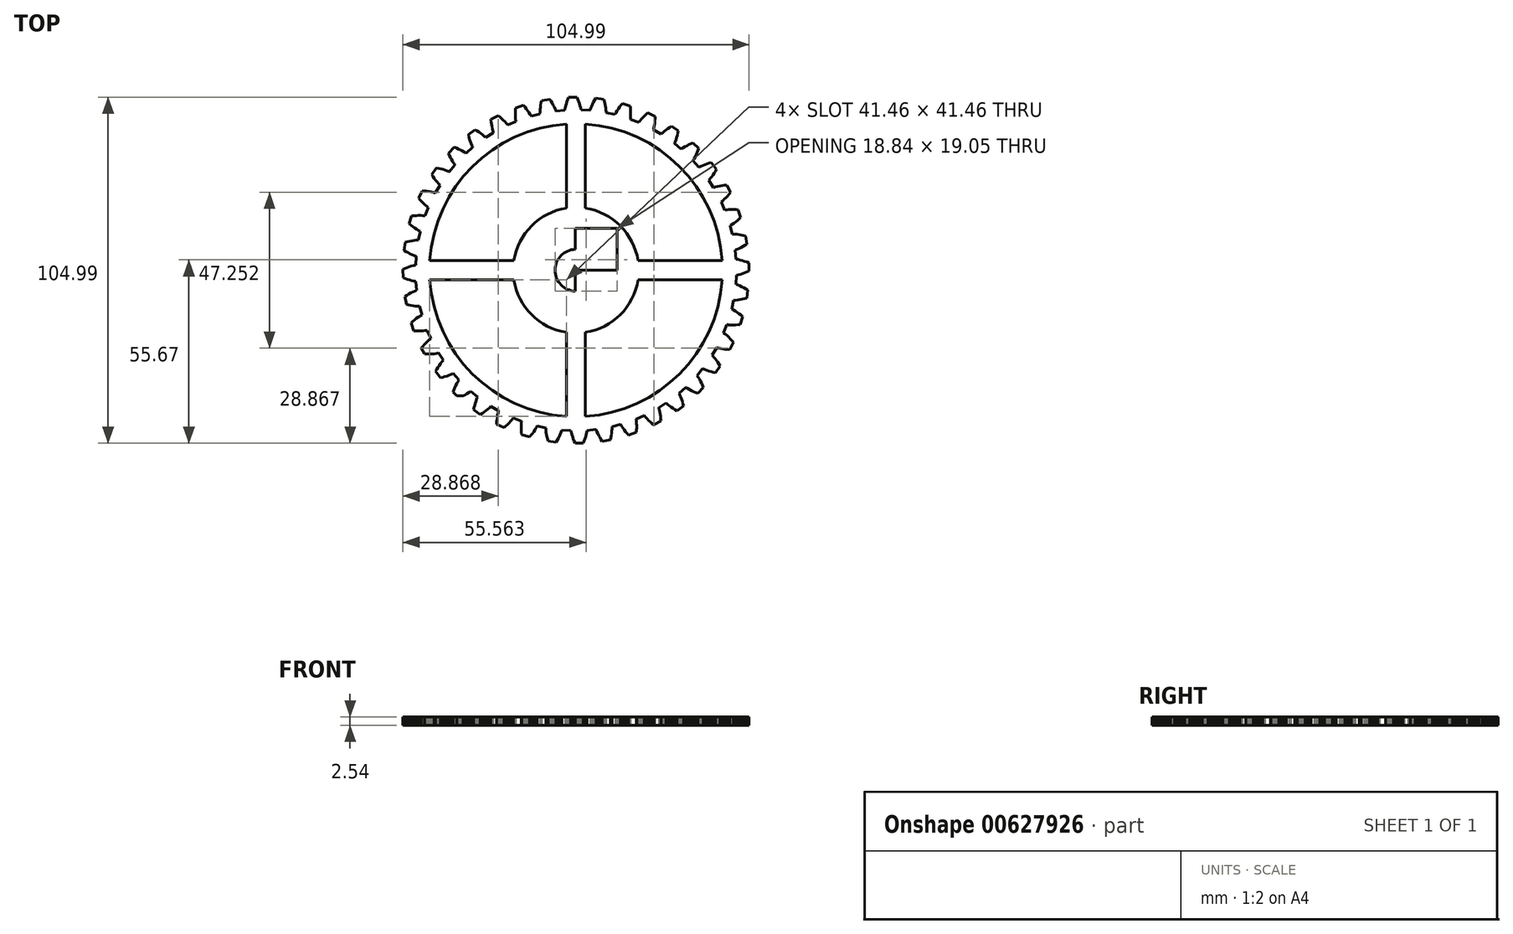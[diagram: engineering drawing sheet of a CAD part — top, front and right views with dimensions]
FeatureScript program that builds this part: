
annotation { "Feature Type Name" : "Feature", "Feature Type Description" : "" }
export const myFeature = defineFeature(function(context is Context, id is Id, definition is map)
    precondition{}
    {
        {
            var Q0;
            Q0=qCreatedBy(makeId("Top.planeOp"),FACE);
            var sketch = newSketch(context, id + "F0", { "sketchPlane" : qUnion([Q0])});
            skLineSegment(sketch, "E0", {"start": v(-71.15, -49.53) * mm, "end": v(-71.15, 55.46) * mm});
            skLineSegment(sketch, "E1", {"start": v(-58.45, -49.53) * mm, "end": v(-58.45, 55.46) * mm});
            skLineSegment(sketch, "E2", {"start": v(-45.75, -49.53) * mm, "end": v(-45.75, 55.46) * mm});
            skLineSegment(sketch, "E3", {"start": v(-33.05, -49.53) * mm, "end": v(-33.05, 55.46) * mm});
            skLineSegment(sketch, "E4", {"start": v(-20.35, -49.53) * mm, "end": v(-20.35, 55.46) * mm});
            skLineSegment(sketch, "E5", {"start": v(-7.65, -49.53) * mm, "end": v(-7.65, 55.46) * mm});
            skLineSegment(sketch, "E6", {"start": v(5.05, -49.53) * mm, "end": v(5.05, 55.46) * mm});
            skLineSegment(sketch, "E7", {"start": v(17.75, -49.53) * mm, "end": v(17.75, 55.46) * mm});
            skLineSegment(sketch, "E8", {"start": v(30.45, -49.53) * mm, "end": v(30.45, 55.46) * mm});
            skLineSegment(sketch, "E9", {"start": v(43.15, -49.53) * mm, "end": v(43.15, 55.46) * mm});
            skLineSegment(sketch, "E10", {"start": v(55.85, -49.53) * mm, "end": v(55.85, 55.46) * mm});
            skLineSegment(sketch, "E11", {"start": v(-72.63, -47.84) * mm, "end": v(62.71, -47.84) * mm});
            skLineSegment(sketch, "E12", {"start": v(-72.63, -35.14) * mm, "end": v(62.71, -35.14) * mm});
            skLineSegment(sketch, "E13", {"start": v(-72.63, -22.44) * mm, "end": v(62.71, -22.44) * mm});
            skLineSegment(sketch, "E14", {"start": v(-72.63, -9.74) * mm, "end": v(62.71, -9.74) * mm});
            skLineSegment(sketch, "E15", {"start": v(-72.63, 2.96) * mm, "end": v(62.71, 2.96) * mm});
            skLineSegment(sketch, "E16", {"start": v(-72.63, 15.66) * mm, "end": v(62.71, 15.66) * mm});
            skLineSegment(sketch, "E17", {"start": v(-72.63, 28.36) * mm, "end": v(62.71, 28.36) * mm});
            skLineSegment(sketch, "E18", {"start": v(-72.63, 41.06) * mm, "end": v(62.71, 41.06) * mm});
            skLineSegment(sketch, "E19", {"start": v(-72.63, 53.76) * mm, "end": v(62.71, 53.76) * mm});
            skLineSegment(sketch, "E20", {"start": v(28.36, -1.3) * mm, "end": v(28.51, -1.34) * mm});
            skLineSegment(sketch, "E21", {"start": v(28.51, -1.34) * mm, "end": v(28.67, -1.4) * mm});
            skLineSegment(sketch, "E22", {"start": v(28.67, -1.4) * mm, "end": v(28.98, -1.5) * mm});
            skLineSegment(sketch, "E23", {"start": v(28.98, -1.5) * mm, "end": v(29.6, -1.76) * mm});
            skLineSegment(sketch, "E24", {"start": v(29.6, -1.76) * mm, "end": v(30.2, -2.03) * mm});
            skLineSegment(sketch, "E25", {"start": v(30.2, -2.03) * mm, "end": v(30.81, -2.34) * mm});
            skLineSegment(sketch, "E26", {"start": v(30.81, -2.34) * mm, "end": v(31.42, -2.67) * mm});
            skLineSegment(sketch, "E27", {"start": v(31.42, -2.67) * mm, "end": v(32.02, -3.03) * mm});
            skLineSegment(sketch, "E28", {"start": v(32.02, -3.03) * mm, "end": v(31.67, -5.5) * mm});
            skLineSegment(sketch, "E29", {"start": v(31.67, -5.5) * mm, "end": v(31, -5.69) * mm});
            skLineSegment(sketch, "E30", {"start": v(31, -5.69) * mm, "end": v(30.33, -5.84) * mm});
            skLineSegment(sketch, "E31", {"start": v(30.33, -5.84) * mm, "end": v(29.66, -5.97) * mm});
            skLineSegment(sketch, "E32", {"start": v(29.66, -5.97) * mm, "end": v(29, -6.07) * mm});
            skLineSegment(sketch, "E33", {"start": v(29, -6.07) * mm, "end": v(28.33, -6.14) * mm});
            skLineSegment(sketch, "E34", {"start": v(28.33, -6.14) * mm, "end": v(28, -6.16) * mm});
            skLineSegment(sketch, "E35", {"start": v(28, -6.16) * mm, "end": v(27.84, -6.17) * mm});
            skLineSegment(sketch, "E36", {"start": v(27.84, -6.17) * mm, "end": v(27.68, -6.18) * mm});
            skLineSegment(sketch, "E37", {"start": v(27.68, -6.18) * mm, "end": v(27.1, -8.83) * mm});
            skLineSegment(sketch, "E38", {"start": v(27.1, -8.83) * mm, "end": v(27.24, -8.9) * mm});
            skLineSegment(sketch, "E39", {"start": v(27.24, -8.9) * mm, "end": v(27.39, -8.98) * mm});
            skLineSegment(sketch, "E40", {"start": v(27.39, -8.98) * mm, "end": v(27.67, -9.14) * mm});
            skLineSegment(sketch, "E41", {"start": v(27.67, -9.14) * mm, "end": v(28.24, -9.48) * mm});
            skLineSegment(sketch, "E42", {"start": v(28.24, -9.48) * mm, "end": v(28.8, -9.85) * mm});
            skLineSegment(sketch, "E43", {"start": v(28.8, -9.85) * mm, "end": v(29.36, -10.25) * mm});
            skLineSegment(sketch, "E44", {"start": v(29.36, -10.25) * mm, "end": v(29.9, -10.67) * mm});
            skLineSegment(sketch, "E45", {"start": v(29.9, -10.67) * mm, "end": v(30.44, -11.11) * mm});
            skLineSegment(sketch, "E46", {"start": v(30.44, -11.11) * mm, "end": v(29.7, -13.5) * mm});
            skLineSegment(sketch, "E47", {"start": v(29.7, -13.5) * mm, "end": v(29.01, -13.58) * mm});
            skLineSegment(sketch, "E48", {"start": v(29.01, -13.58) * mm, "end": v(28.33, -13.63) * mm});
            skLineSegment(sketch, "E49", {"start": v(28.33, -13.63) * mm, "end": v(27.65, -13.65) * mm});
            skLineSegment(sketch, "E50", {"start": v(27.65, -13.65) * mm, "end": v(26.98, -13.64) * mm});
            skLineSegment(sketch, "E51", {"start": v(26.98, -13.64) * mm, "end": v(26.31, -13.61) * mm});
            skLineSegment(sketch, "E52", {"start": v(26.31, -13.61) * mm, "end": v(25.99, -13.58) * mm});
            skLineSegment(sketch, "E53", {"start": v(25.99, -13.58) * mm, "end": v(25.82, -13.57) * mm});
            skLineSegment(sketch, "E54", {"start": v(25.82, -13.57) * mm, "end": v(25.66, -13.55) * mm});
            skLineSegment(sketch, "E55", {"start": v(25.66, -13.55) * mm, "end": v(24.67, -16.07) * mm});
            skLineSegment(sketch, "E56", {"start": v(24.67, -16.07) * mm, "end": v(24.8, -16.17) * mm});
            skLineSegment(sketch, "E57", {"start": v(24.8, -16.17) * mm, "end": v(24.93, -16.26) * mm});
            skLineSegment(sketch, "E58", {"start": v(24.93, -16.26) * mm, "end": v(25.2, -16.47) * mm});
            skLineSegment(sketch, "E59", {"start": v(25.2, -16.47) * mm, "end": v(25.7, -16.9) * mm});
            skLineSegment(sketch, "E60", {"start": v(25.7, -16.9) * mm, "end": v(26.2, -17.35) * mm});
            skLineSegment(sketch, "E61", {"start": v(26.2, -17.35) * mm, "end": v(26.68, -17.83) * mm});
            skLineSegment(sketch, "E62", {"start": v(26.68, -17.83) * mm, "end": v(27.15, -18.33) * mm});
            skLineSegment(sketch, "E63", {"start": v(27.15, -18.33) * mm, "end": v(27.61, -18.85) * mm});
            skLineSegment(sketch, "E64", {"start": v(27.61, -18.85) * mm, "end": v(26.52, -21.1) * mm});
            skLineSegment(sketch, "E65", {"start": v(26.52, -21.1) * mm, "end": v(25.82, -21.06) * mm});
            skLineSegment(sketch, "E66", {"start": v(25.82, -21.06) * mm, "end": v(25.14, -21) * mm});
            skLineSegment(sketch, "E67", {"start": v(25.14, -21) * mm, "end": v(24.46, -20.92) * mm});
            skLineSegment(sketch, "E68", {"start": v(24.46, -20.92) * mm, "end": v(23.8, -20.81) * mm});
            skLineSegment(sketch, "E69", {"start": v(23.8, -20.81) * mm, "end": v(23.15, -20.67) * mm});
            skLineSegment(sketch, "E70", {"start": v(23.15, -20.67) * mm, "end": v(22.83, -20.6) * mm});
            skLineSegment(sketch, "E71", {"start": v(22.83, -20.6) * mm, "end": v(22.67, -20.55) * mm});
            skLineSegment(sketch, "E72", {"start": v(22.67, -20.55) * mm, "end": v(22.51, -20.5) * mm});
            skLineSegment(sketch, "E73", {"start": v(22.51, -20.5) * mm, "end": v(21.14, -22.85) * mm});
            skLineSegment(sketch, "E74", {"start": v(21.14, -22.85) * mm, "end": v(21.26, -22.96) * mm});
            skLineSegment(sketch, "E75", {"start": v(21.26, -22.96) * mm, "end": v(21.37, -23.08) * mm});
            skLineSegment(sketch, "E76", {"start": v(21.37, -23.08) * mm, "end": v(21.6, -23.32) * mm});
            skLineSegment(sketch, "E77", {"start": v(21.6, -23.32) * mm, "end": v(22.03, -23.82) * mm});
            skLineSegment(sketch, "E78", {"start": v(22.03, -23.82) * mm, "end": v(22.45, -24.34) * mm});
            skLineSegment(sketch, "E79", {"start": v(22.45, -24.34) * mm, "end": v(22.85, -24.9) * mm});
            skLineSegment(sketch, "E80", {"start": v(22.85, -24.9) * mm, "end": v(23.24, -25.46) * mm});
            skLineSegment(sketch, "E81", {"start": v(23.24, -25.46) * mm, "end": v(23.61, -26.05) * mm});
            skLineSegment(sketch, "E82", {"start": v(23.61, -26.05) * mm, "end": v(22.18, -28.1) * mm});
            skLineSegment(sketch, "E83", {"start": v(22.18, -28.1) * mm, "end": v(21.5, -27.96) * mm});
            skLineSegment(sketch, "E84", {"start": v(21.5, -27.96) * mm, "end": v(20.83, -27.8) * mm});
            skLineSegment(sketch, "E85", {"start": v(20.83, -27.8) * mm, "end": v(20.18, -27.6) * mm});
            skLineSegment(sketch, "E86", {"start": v(20.18, -27.6) * mm, "end": v(19.54, -27.4) * mm});
            skLineSegment(sketch, "E87", {"start": v(19.54, -27.4) * mm, "end": v(18.92, -27.15) * mm});
            skLineSegment(sketch, "E88", {"start": v(18.92, -27.15) * mm, "end": v(18.61, -27.03) * mm});
            skLineSegment(sketch, "E89", {"start": v(18.61, -27.03) * mm, "end": v(18.47, -26.96) * mm});
            skLineSegment(sketch, "E90", {"start": v(18.47, -26.96) * mm, "end": v(18.32, -26.9) * mm});
            skLineSegment(sketch, "E91", {"start": v(18.32, -26.9) * mm, "end": v(16.6, -28.99) * mm});
            skLineSegment(sketch, "E92", {"start": v(16.6, -28.99) * mm, "end": v(16.7, -29.12) * mm});
            skLineSegment(sketch, "E93", {"start": v(16.7, -29.12) * mm, "end": v(16.79, -29.25) * mm});
            skLineSegment(sketch, "E94", {"start": v(16.79, -29.25) * mm, "end": v(16.97, -29.52) * mm});
            skLineSegment(sketch, "E95", {"start": v(16.97, -29.52) * mm, "end": v(17.32, -30.09) * mm});
            skLineSegment(sketch, "E96", {"start": v(17.32, -30.09) * mm, "end": v(17.65, -30.67) * mm});
            skLineSegment(sketch, "E97", {"start": v(17.65, -30.67) * mm, "end": v(17.96, -31.28) * mm});
            skLineSegment(sketch, "E98", {"start": v(17.96, -31.28) * mm, "end": v(18.26, -31.9) * mm});
            skLineSegment(sketch, "E99", {"start": v(18.26, -31.9) * mm, "end": v(18.53, -32.54) * mm});
            skLineSegment(sketch, "E100", {"start": v(18.53, -32.54) * mm, "end": v(16.8, -34.34) * mm});
            skLineSegment(sketch, "E101", {"start": v(16.8, -34.34) * mm, "end": v(16.15, -34.09) * mm});
            skLineSegment(sketch, "E102", {"start": v(16.15, -34.09) * mm, "end": v(15.51, -33.82) * mm});
            skLineSegment(sketch, "E103", {"start": v(15.51, -33.82) * mm, "end": v(14.9, -33.53) * mm});
            skLineSegment(sketch, "E104", {"start": v(14.9, -33.53) * mm, "end": v(14.3, -33.22) * mm});
            skLineSegment(sketch, "E105", {"start": v(14.3, -33.22) * mm, "end": v(13.73, -32.9) * mm});
            skLineSegment(sketch, "E106", {"start": v(13.73, -32.9) * mm, "end": v(13.45, -32.72) * mm});
            skLineSegment(sketch, "E107", {"start": v(13.45, -32.72) * mm, "end": v(13.3, -32.63) * mm});
            skLineSegment(sketch, "E108", {"start": v(13.3, -32.63) * mm, "end": v(13.17, -32.54) * mm});
            skLineSegment(sketch, "E109", {"start": v(13.17, -32.54) * mm, "end": v(11.15, -34.34) * mm});
            skLineSegment(sketch, "E110", {"start": v(11.15, -34.34) * mm, "end": v(11.22, -34.48) * mm});
            skLineSegment(sketch, "E111", {"start": v(11.22, -34.48) * mm, "end": v(11.3, -34.63) * mm});
            skLineSegment(sketch, "E112", {"start": v(11.3, -34.63) * mm, "end": v(11.43, -34.93) * mm});
            skLineSegment(sketch, "E113", {"start": v(11.43, -34.93) * mm, "end": v(11.7, -35.54) * mm});
            skLineSegment(sketch, "E114", {"start": v(11.7, -35.54) * mm, "end": v(11.93, -36.17) * mm});
            skLineSegment(sketch, "E115", {"start": v(11.93, -36.17) * mm, "end": v(12.14, -36.81) * mm});
            skLineSegment(sketch, "E116", {"start": v(12.14, -36.81) * mm, "end": v(12.33, -37.48) * mm});
            skLineSegment(sketch, "E117", {"start": v(12.33, -37.48) * mm, "end": v(12.5, -38.15) * mm});
            skLineSegment(sketch, "E118", {"start": v(12.5, -38.15) * mm, "end": v(10.5, -39.66) * mm});
            skLineSegment(sketch, "E119", {"start": v(10.5, -39.66) * mm, "end": v(9.9, -39.3) * mm});
            skLineSegment(sketch, "E120", {"start": v(9.9, -39.3) * mm, "end": v(9.32, -38.94) * mm});
            skLineSegment(sketch, "E121", {"start": v(9.32, -38.94) * mm, "end": v(8.76, -38.56) * mm});
            skLineSegment(sketch, "E122", {"start": v(8.76, -38.56) * mm, "end": v(8.22, -38.16) * mm});
            skLineSegment(sketch, "E123", {"start": v(8.22, -38.16) * mm, "end": v(7.7, -37.75) * mm});
            skLineSegment(sketch, "E124", {"start": v(7.7, -37.75) * mm, "end": v(7.45, -37.53) * mm});
            skLineSegment(sketch, "E125", {"start": v(7.45, -37.53) * mm, "end": v(7.33, -37.42) * mm});
            skLineSegment(sketch, "E126", {"start": v(7.33, -37.42) * mm, "end": v(7.21, -37.31) * mm});
            skLineSegment(sketch, "E127", {"start": v(7.21, -37.31) * mm, "end": v(4.93, -38.77) * mm});
            skLineSegment(sketch, "E128", {"start": v(4.93, -38.77) * mm, "end": v(4.98, -38.93) * mm});
            skLineSegment(sketch, "E129", {"start": v(4.98, -38.93) * mm, "end": v(5.02, -39.08) * mm});
            skLineSegment(sketch, "E130", {"start": v(5.02, -39.08) * mm, "end": v(5.12, -39.4) * mm});
            skLineSegment(sketch, "E131", {"start": v(5.12, -39.4) * mm, "end": v(5.28, -40.04) * mm});
            skLineSegment(sketch, "E132", {"start": v(5.28, -40.04) * mm, "end": v(5.41, -40.7) * mm});
            skLineSegment(sketch, "E133", {"start": v(5.41, -40.7) * mm, "end": v(5.52, -41.37) * mm});
            skLineSegment(sketch, "E134", {"start": v(5.52, -41.37) * mm, "end": v(5.6, -42.06) * mm});
            skLineSegment(sketch, "E135", {"start": v(5.6, -42.06) * mm, "end": v(5.67, -42.75) * mm});
            skLineSegment(sketch, "E136", {"start": v(5.67, -42.75) * mm, "end": v(3.46, -43.93) * mm});
            skLineSegment(sketch, "E137", {"start": v(3.46, -43.93) * mm, "end": v(2.92, -43.49) * mm});
            skLineSegment(sketch, "E138", {"start": v(2.92, -43.49) * mm, "end": v(2.4, -43.04) * mm});
            skLineSegment(sketch, "E139", {"start": v(2.4, -43.04) * mm, "end": v(1.9, -42.57) * mm});
            skLineSegment(sketch, "E140", {"start": v(1.9, -42.57) * mm, "end": v(1.43, -42.1) * mm});
            skLineSegment(sketch, "E141", {"start": v(1.43, -42.1) * mm, "end": v(0.99, -41.6) * mm});
            skLineSegment(sketch, "E142", {"start": v(0.99, -41.6) * mm, "end": v(0.78, -41.35) * mm});
            skLineSegment(sketch, "E143", {"start": v(0.78, -41.35) * mm, "end": v(0.67, -41.22) * mm});
            skLineSegment(sketch, "E144", {"start": v(0.67, -41.22) * mm, "end": v(0.57, -41.1) * mm});
            skLineSegment(sketch, "E145", {"start": v(0.57, -41.1) * mm, "end": v(-1.91, -42.18) * mm});
            skLineSegment(sketch, "E146", {"start": v(-1.91, -42.18) * mm, "end": v(-1.89, -42.34) * mm});
            skLineSegment(sketch, "E147", {"start": v(-1.89, -42.34) * mm, "end": v(-1.86, -42.5) * mm});
            skLineSegment(sketch, "E148", {"start": v(-1.86, -42.5) * mm, "end": v(-1.82, -42.83) * mm});
            skLineSegment(sketch, "E149", {"start": v(-1.82, -42.83) * mm, "end": v(-1.76, -43.49) * mm});
            skLineSegment(sketch, "E150", {"start": v(-1.76, -43.49) * mm, "end": v(-1.74, -44.16) * mm});
            skLineSegment(sketch, "E151", {"start": v(-1.74, -44.16) * mm, "end": v(-1.73, -44.84) * mm});
            skLineSegment(sketch, "E152", {"start": v(-1.73, -44.84) * mm, "end": v(-1.75, -45.53) * mm});
            skLineSegment(sketch, "E153", {"start": v(-1.75, -45.53) * mm, "end": v(-1.8, -46.23) * mm});
            skLineSegment(sketch, "E154", {"start": v(-1.8, -46.23) * mm, "end": v(-4.16, -47.04) * mm});
            skLineSegment(sketch, "E155", {"start": v(-4.16, -47.04) * mm, "end": v(-4.63, -46.52) * mm});
            skLineSegment(sketch, "E156", {"start": v(-4.63, -46.52) * mm, "end": v(-5.07, -46) * mm});
            skLineSegment(sketch, "E157", {"start": v(-5.07, -46) * mm, "end": v(-5.49, -45.46) * mm});
            skLineSegment(sketch, "E158", {"start": v(-5.49, -45.46) * mm, "end": v(-5.88, -44.91) * mm});
            skLineSegment(sketch, "E159", {"start": v(-5.88, -44.91) * mm, "end": v(-6.24, -44.36) * mm});
            skLineSegment(sketch, "E160", {"start": v(-6.24, -44.36) * mm, "end": v(-6.41, -44.08) * mm});
            skLineSegment(sketch, "E161", {"start": v(-6.41, -44.08) * mm, "end": v(-6.5, -43.93) * mm});
            skLineSegment(sketch, "E162", {"start": v(-6.5, -43.93) * mm, "end": v(-6.57, -43.8) * mm});
            skLineSegment(sketch, "E163", {"start": v(-6.57, -43.8) * mm, "end": v(-9.2, -44.47) * mm});
            skLineSegment(sketch, "E164", {"start": v(-9.2, -44.47) * mm, "end": v(-9.2, -44.64) * mm});
            skLineSegment(sketch, "E165", {"start": v(-9.2, -44.64) * mm, "end": v(-9.2, -44.8) * mm});
            skLineSegment(sketch, "E166", {"start": v(-9.2, -44.8) * mm, "end": v(-9.21, -45.13) * mm});
            skLineSegment(sketch, "E167", {"start": v(-9.21, -45.13) * mm, "end": v(-9.26, -45.8) * mm});
            skLineSegment(sketch, "E168", {"start": v(-9.26, -45.8) * mm, "end": v(-9.33, -46.46) * mm});
            skLineSegment(sketch, "E169", {"start": v(-9.33, -46.46) * mm, "end": v(-9.44, -47.13) * mm});
            skLineSegment(sketch, "E170", {"start": v(-9.44, -47.13) * mm, "end": v(-9.57, -47.8) * mm});
            skLineSegment(sketch, "E171", {"start": v(-9.57, -47.8) * mm, "end": v(-9.72, -48.49) * mm});
            skLineSegment(sketch, "E172", {"start": v(-9.72, -48.49) * mm, "end": v(-12.18, -48.93) * mm});
            skLineSegment(sketch, "E173", {"start": v(-12.18, -48.93) * mm, "end": v(-12.56, -48.34) * mm});
            skLineSegment(sketch, "E174", {"start": v(-12.56, -48.34) * mm, "end": v(-12.92, -47.75) * mm});
            skLineSegment(sketch, "E175", {"start": v(-12.92, -47.75) * mm, "end": v(-13.24, -47.15) * mm});
            skLineSegment(sketch, "E176", {"start": v(-13.24, -47.15) * mm, "end": v(-13.55, -46.55) * mm});
            skLineSegment(sketch, "E177", {"start": v(-13.55, -46.55) * mm, "end": v(-13.82, -45.95) * mm});
            skLineSegment(sketch, "E178", {"start": v(-13.82, -45.95) * mm, "end": v(-13.94, -45.64) * mm});
            skLineSegment(sketch, "E179", {"start": v(-13.94, -45.64) * mm, "end": v(-14, -45.5) * mm});
            skLineSegment(sketch, "E180", {"start": v(-14, -45.5) * mm, "end": v(-14.06, -45.34) * mm});
            skLineSegment(sketch, "E181", {"start": v(-14.06, -45.34) * mm, "end": v(-16.75, -45.6) * mm});
            skLineSegment(sketch, "E182", {"start": v(-16.75, -45.6) * mm, "end": v(-16.78, -45.76) * mm});
            skLineSegment(sketch, "E183", {"start": v(-16.78, -45.76) * mm, "end": v(-16.8, -45.92) * mm});
            skLineSegment(sketch, "E184", {"start": v(-16.8, -45.92) * mm, "end": v(-16.87, -46.25) * mm});
            skLineSegment(sketch, "E185", {"start": v(-16.87, -46.25) * mm, "end": v(-17.02, -46.9) * mm});
            skLineSegment(sketch, "E186", {"start": v(-17.02, -46.9) * mm, "end": v(-17.2, -47.54) * mm});
            skLineSegment(sketch, "E187", {"start": v(-17.2, -47.54) * mm, "end": v(-17.4, -48.19) * mm});
            skLineSegment(sketch, "E188", {"start": v(-17.4, -48.19) * mm, "end": v(-17.64, -48.84) * mm});
            skLineSegment(sketch, "E189", {"start": v(-17.64, -48.84) * mm, "end": v(-17.9, -49.48) * mm});
            skLineSegment(sketch, "E190", {"start": v(-17.9, -49.48) * mm, "end": v(-20.4, -49.53) * mm});
            skLineSegment(sketch, "E191", {"start": v(-20.4, -49.53) * mm, "end": v(-20.68, -48.9) * mm});
            skLineSegment(sketch, "E192", {"start": v(-20.68, -48.9) * mm, "end": v(-20.94, -48.25) * mm});
            skLineSegment(sketch, "E193", {"start": v(-20.94, -48.25) * mm, "end": v(-21.17, -47.62) * mm});
            skLineSegment(sketch, "E194", {"start": v(-21.17, -47.62) * mm, "end": v(-21.37, -46.97) * mm});
            skLineSegment(sketch, "E195", {"start": v(-21.37, -46.97) * mm, "end": v(-21.55, -46.33) * mm});
            skLineSegment(sketch, "E196", {"start": v(-21.55, -46.33) * mm, "end": v(-21.62, -46.01) * mm});
            skLineSegment(sketch, "E197", {"start": v(-21.62, -46.01) * mm, "end": v(-21.65, -45.85) * mm});
            skLineSegment(sketch, "E198", {"start": v(-21.65, -45.85) * mm, "end": v(-21.69, -45.7) * mm});
            skLineSegment(sketch, "E199", {"start": v(-21.69, -45.7) * mm, "end": v(-24.4, -45.53) * mm});
            skLineSegment(sketch, "E200", {"start": v(-24.4, -45.53) * mm, "end": v(-24.44, -45.69) * mm});
            skLineSegment(sketch, "E201", {"start": v(-24.44, -45.69) * mm, "end": v(-24.5, -45.84) * mm});
            skLineSegment(sketch, "E202", {"start": v(-24.5, -45.84) * mm, "end": v(-24.6, -46.15) * mm});
            skLineSegment(sketch, "E203", {"start": v(-24.6, -46.15) * mm, "end": v(-24.86, -46.77) * mm});
            skLineSegment(sketch, "E204", {"start": v(-24.86, -46.77) * mm, "end": v(-25.13, -47.38) * mm});
            skLineSegment(sketch, "E205", {"start": v(-25.13, -47.38) * mm, "end": v(-25.44, -47.99) * mm});
            skLineSegment(sketch, "E206", {"start": v(-25.44, -47.99) * mm, "end": v(-25.77, -48.59) * mm});
            skLineSegment(sketch, "E207", {"start": v(-25.77, -48.59) * mm, "end": v(-26.13, -49.19) * mm});
            skLineSegment(sketch, "E208", {"start": v(-26.13, -49.19) * mm, "end": v(-28.6, -48.84) * mm});
            skLineSegment(sketch, "E209", {"start": v(-28.6, -48.84) * mm, "end": v(-28.79, -48.17) * mm});
            skLineSegment(sketch, "E210", {"start": v(-28.79, -48.17) * mm, "end": v(-28.94, -47.5) * mm});
            skLineSegment(sketch, "E211", {"start": v(-28.94, -47.5) * mm, "end": v(-29.07, -46.83) * mm});
            skLineSegment(sketch, "E212", {"start": v(-29.07, -46.83) * mm, "end": v(-29.17, -46.17) * mm});
            skLineSegment(sketch, "E213", {"start": v(-29.17, -46.17) * mm, "end": v(-29.24, -45.5) * mm});
            skLineSegment(sketch, "E214", {"start": v(-29.24, -45.5) * mm, "end": v(-29.26, -45.18) * mm});
            skLineSegment(sketch, "E215", {"start": v(-29.26, -45.18) * mm, "end": v(-29.27, -45.02) * mm});
            skLineSegment(sketch, "E216", {"start": v(-29.27, -45.02) * mm, "end": v(-29.28, -44.85) * mm});
            skLineSegment(sketch, "E217", {"start": v(-29.28, -44.85) * mm, "end": v(-31.93, -44.27) * mm});
            skLineSegment(sketch, "E218", {"start": v(-31.93, -44.27) * mm, "end": v(-32, -44.42) * mm});
            skLineSegment(sketch, "E219", {"start": v(-32, -44.42) * mm, "end": v(-32.08, -44.56) * mm});
            skLineSegment(sketch, "E220", {"start": v(-32.08, -44.56) * mm, "end": v(-32.24, -44.85) * mm});
            skLineSegment(sketch, "E221", {"start": v(-32.24, -44.85) * mm, "end": v(-32.58, -45.42) * mm});
            skLineSegment(sketch, "E222", {"start": v(-32.58, -45.42) * mm, "end": v(-32.95, -45.98) * mm});
            skLineSegment(sketch, "E223", {"start": v(-32.95, -45.98) * mm, "end": v(-33.35, -46.53) * mm});
            skLineSegment(sketch, "E224", {"start": v(-33.35, -46.53) * mm, "end": v(-33.77, -47.07) * mm});
            skLineSegment(sketch, "E225", {"start": v(-33.77, -47.07) * mm, "end": v(-34.21, -47.6) * mm});
            skLineSegment(sketch, "E226", {"start": v(-34.21, -47.6) * mm, "end": v(-36.6, -46.88) * mm});
            skLineSegment(sketch, "E227", {"start": v(-36.6, -46.88) * mm, "end": v(-36.68, -46.19) * mm});
            skLineSegment(sketch, "E228", {"start": v(-36.68, -46.19) * mm, "end": v(-36.73, -45.5) * mm});
            skLineSegment(sketch, "E229", {"start": v(-36.73, -45.5) * mm, "end": v(-36.75, -44.82) * mm});
            skLineSegment(sketch, "E230", {"start": v(-36.75, -44.82) * mm, "end": v(-36.74, -44.15) * mm});
            skLineSegment(sketch, "E231", {"start": v(-36.74, -44.15) * mm, "end": v(-36.71, -43.49) * mm});
            skLineSegment(sketch, "E232", {"start": v(-36.71, -43.49) * mm, "end": v(-36.68, -43.16) * mm});
            skLineSegment(sketch, "E233", {"start": v(-36.68, -43.16) * mm, "end": v(-36.67, -43) * mm});
            skLineSegment(sketch, "E234", {"start": v(-36.67, -43) * mm, "end": v(-36.65, -42.83) * mm});
            skLineSegment(sketch, "E235", {"start": v(-36.65, -42.83) * mm, "end": v(-39.17, -41.84) * mm});
            skLineSegment(sketch, "E236", {"start": v(-39.17, -41.84) * mm, "end": v(-39.27, -41.98) * mm});
            skLineSegment(sketch, "E237", {"start": v(-39.27, -41.98) * mm, "end": v(-39.36, -42.1) * mm});
            skLineSegment(sketch, "E238", {"start": v(-39.36, -42.1) * mm, "end": v(-39.57, -42.37) * mm});
            skLineSegment(sketch, "E239", {"start": v(-39.57, -42.37) * mm, "end": v(-40, -42.87) * mm});
            skLineSegment(sketch, "E240", {"start": v(-40, -42.87) * mm, "end": v(-40.45, -43.37) * mm});
            skLineSegment(sketch, "E241", {"start": v(-40.45, -43.37) * mm, "end": v(-40.93, -43.85) * mm});
            skLineSegment(sketch, "E242", {"start": v(-40.93, -43.85) * mm, "end": v(-41.43, -44.32) * mm});
            skLineSegment(sketch, "E243", {"start": v(-41.43, -44.32) * mm, "end": v(-41.95, -44.78) * mm});
            skLineSegment(sketch, "E244", {"start": v(-41.95, -44.78) * mm, "end": v(-44.2, -43.7) * mm});
            skLineSegment(sketch, "E245", {"start": v(-44.2, -43.7) * mm, "end": v(-44.16, -43) * mm});
            skLineSegment(sketch, "E246", {"start": v(-44.16, -43) * mm, "end": v(-44.1, -42.3) * mm});
            skLineSegment(sketch, "E247", {"start": v(-44.1, -42.3) * mm, "end": v(-44.02, -41.63) * mm});
            skLineSegment(sketch, "E248", {"start": v(-44.02, -41.63) * mm, "end": v(-43.91, -40.97) * mm});
            skLineSegment(sketch, "E249", {"start": v(-43.91, -40.97) * mm, "end": v(-43.77, -40.32) * mm});
            skLineSegment(sketch, "E250", {"start": v(-43.77, -40.32) * mm, "end": v(-43.7, -40) * mm});
            skLineSegment(sketch, "E251", {"start": v(-43.7, -40) * mm, "end": v(-43.65, -39.84) * mm});
            skLineSegment(sketch, "E252", {"start": v(-43.65, -39.84) * mm, "end": v(-43.6, -39.69) * mm});
            skLineSegment(sketch, "E253", {"start": v(-43.6, -39.69) * mm, "end": v(-45.95, -38.31) * mm});
            skLineSegment(sketch, "E254", {"start": v(-45.95, -38.31) * mm, "end": v(-46.06, -38.43) * mm});
            skLineSegment(sketch, "E255", {"start": v(-46.06, -38.43) * mm, "end": v(-46.18, -38.54) * mm});
            skLineSegment(sketch, "E256", {"start": v(-46.18, -38.54) * mm, "end": v(-46.42, -38.77) * mm});
            skLineSegment(sketch, "E257", {"start": v(-46.42, -38.77) * mm, "end": v(-46.92, -39.2) * mm});
            skLineSegment(sketch, "E258", {"start": v(-46.92, -39.2) * mm, "end": v(-47.44, -39.62) * mm});
            skLineSegment(sketch, "E259", {"start": v(-47.44, -39.62) * mm, "end": v(-48, -40.02) * mm});
            skLineSegment(sketch, "E260", {"start": v(-48, -40.02) * mm, "end": v(-48.56, -40.41) * mm});
            skLineSegment(sketch, "E261", {"start": v(-48.56, -40.41) * mm, "end": v(-49.15, -40.78) * mm});
            skLineSegment(sketch, "E262", {"start": v(-49.15, -40.78) * mm, "end": v(-51.2, -39.35) * mm});
            skLineSegment(sketch, "E263", {"start": v(-51.2, -39.35) * mm, "end": v(-51.06, -38.67) * mm});
            skLineSegment(sketch, "E264", {"start": v(-51.06, -38.67) * mm, "end": v(-50.9, -38) * mm});
            skLineSegment(sketch, "E265", {"start": v(-50.9, -38) * mm, "end": v(-50.7, -37.35) * mm});
            skLineSegment(sketch, "E266", {"start": v(-50.7, -37.35) * mm, "end": v(-50.5, -36.71) * mm});
            skLineSegment(sketch, "E267", {"start": v(-50.5, -36.71) * mm, "end": v(-50.25, -36.1) * mm});
            skLineSegment(sketch, "E268", {"start": v(-50.25, -36.1) * mm, "end": v(-50.13, -35.79) * mm});
            skLineSegment(sketch, "E269", {"start": v(-50.13, -35.79) * mm, "end": v(-50.06, -35.64) * mm});
            skLineSegment(sketch, "E270", {"start": v(-50.06, -35.64) * mm, "end": v(-50, -35.5) * mm});
            skLineSegment(sketch, "E271", {"start": v(-50, -35.5) * mm, "end": v(-52.09, -33.77) * mm});
            skLineSegment(sketch, "E272", {"start": v(-52.09, -33.77) * mm, "end": v(-52.22, -33.87) * mm});
            skLineSegment(sketch, "E273", {"start": v(-52.22, -33.87) * mm, "end": v(-52.35, -33.96) * mm});
            skLineSegment(sketch, "E274", {"start": v(-52.35, -33.96) * mm, "end": v(-52.62, -34.14) * mm});
            skLineSegment(sketch, "E275", {"start": v(-52.62, -34.14) * mm, "end": v(-53.19, -34.5) * mm});
            skLineSegment(sketch, "E276", {"start": v(-53.19, -34.5) * mm, "end": v(-53.77, -34.83) * mm});
            skLineSegment(sketch, "E277", {"start": v(-53.77, -34.83) * mm, "end": v(-54.38, -35.14) * mm});
            skLineSegment(sketch, "E278", {"start": v(-54.38, -35.14) * mm, "end": v(-55, -35.43) * mm});
            skLineSegment(sketch, "E279", {"start": v(-55, -35.43) * mm, "end": v(-55.64, -35.7) * mm});
            skLineSegment(sketch, "E280", {"start": v(-55.64, -35.7) * mm, "end": v(-57.44, -33.97) * mm});
            skLineSegment(sketch, "E281", {"start": v(-57.44, -33.97) * mm, "end": v(-57.19, -33.32) * mm});
            skLineSegment(sketch, "E282", {"start": v(-57.19, -33.32) * mm, "end": v(-56.92, -32.69) * mm});
            skLineSegment(sketch, "E283", {"start": v(-56.92, -32.69) * mm, "end": v(-56.63, -32.07) * mm});
            skLineSegment(sketch, "E284", {"start": v(-56.63, -32.07) * mm, "end": v(-56.32, -31.47) * mm});
            skLineSegment(sketch, "E285", {"start": v(-56.32, -31.47) * mm, "end": v(-56, -30.9) * mm});
            skLineSegment(sketch, "E286", {"start": v(-56, -30.9) * mm, "end": v(-55.82, -30.62) * mm});
            skLineSegment(sketch, "E287", {"start": v(-55.82, -30.62) * mm, "end": v(-55.73, -30.48) * mm});
            skLineSegment(sketch, "E288", {"start": v(-55.73, -30.48) * mm, "end": v(-55.64, -30.35) * mm});
            skLineSegment(sketch, "E289", {"start": v(-55.64, -30.35) * mm, "end": v(-57.44, -28.32) * mm});
            skLineSegment(sketch, "E290", {"start": v(-57.44, -28.32) * mm, "end": v(-57.58, -28.4) * mm});
            skLineSegment(sketch, "E291", {"start": v(-57.58, -28.4) * mm, "end": v(-57.73, -28.47) * mm});
            skLineSegment(sketch, "E292", {"start": v(-57.73, -28.47) * mm, "end": v(-58.03, -28.6) * mm});
            skLineSegment(sketch, "E293", {"start": v(-58.03, -28.6) * mm, "end": v(-58.64, -28.86) * mm});
            skLineSegment(sketch, "E294", {"start": v(-58.64, -28.86) * mm, "end": v(-59.27, -29.1) * mm});
            skLineSegment(sketch, "E295", {"start": v(-59.27, -29.1) * mm, "end": v(-59.91, -29.31) * mm});
            skLineSegment(sketch, "E296", {"start": v(-59.91, -29.31) * mm, "end": v(-60.58, -29.5) * mm});
            skLineSegment(sketch, "E297", {"start": v(-60.58, -29.5) * mm, "end": v(-61.25, -29.68) * mm});
            skLineSegment(sketch, "E298", {"start": v(-61.25, -29.68) * mm, "end": v(-62.76, -27.68) * mm});
            skLineSegment(sketch, "E299", {"start": v(-62.76, -27.68) * mm, "end": v(-62.4, -27.08) * mm});
            skLineSegment(sketch, "E300", {"start": v(-62.4, -27.08) * mm, "end": v(-62.04, -26.5) * mm});
            skLineSegment(sketch, "E301", {"start": v(-62.04, -26.5) * mm, "end": v(-61.66, -25.93) * mm});
            skLineSegment(sketch, "E302", {"start": v(-61.66, -25.93) * mm, "end": v(-61.26, -25.39) * mm});
            skLineSegment(sketch, "E303", {"start": v(-61.26, -25.39) * mm, "end": v(-60.85, -24.87) * mm});
            skLineSegment(sketch, "E304", {"start": v(-60.85, -24.87) * mm, "end": v(-60.63, -24.62) * mm});
            skLineSegment(sketch, "E305", {"start": v(-60.63, -24.62) * mm, "end": v(-60.52, -24.5) * mm});
            skLineSegment(sketch, "E306", {"start": v(-60.52, -24.5) * mm, "end": v(-60.41, -24.38) * mm});
            skLineSegment(sketch, "E307", {"start": v(-60.41, -24.38) * mm, "end": v(-61.87, -22.1) * mm});
            skLineSegment(sketch, "E308", {"start": v(-61.87, -22.1) * mm, "end": v(-62.03, -22.15) * mm});
            skLineSegment(sketch, "E309", {"start": v(-62.03, -22.15) * mm, "end": v(-62.18, -22.2) * mm});
            skLineSegment(sketch, "E310", {"start": v(-62.18, -22.2) * mm, "end": v(-62.5, -22.29) * mm});
            skLineSegment(sketch, "E311", {"start": v(-62.5, -22.29) * mm, "end": v(-63.14, -22.45) * mm});
            skLineSegment(sketch, "E312", {"start": v(-63.14, -22.45) * mm, "end": v(-63.8, -22.58) * mm});
            skLineSegment(sketch, "E313", {"start": v(-63.8, -22.58) * mm, "end": v(-64.47, -22.7) * mm});
            skLineSegment(sketch, "E314", {"start": v(-64.47, -22.7) * mm, "end": v(-65.16, -22.78) * mm});
            skLineSegment(sketch, "E315", {"start": v(-65.16, -22.78) * mm, "end": v(-65.85, -22.84) * mm});
            skLineSegment(sketch, "E316", {"start": v(-65.85, -22.84) * mm, "end": v(-67.03, -20.64) * mm});
            skLineSegment(sketch, "E317", {"start": v(-67.03, -20.64) * mm, "end": v(-66.59, -20.1) * mm});
            skLineSegment(sketch, "E318", {"start": v(-66.59, -20.1) * mm, "end": v(-66.14, -19.58) * mm});
            skLineSegment(sketch, "E319", {"start": v(-66.14, -19.58) * mm, "end": v(-65.67, -19.08) * mm});
            skLineSegment(sketch, "E320", {"start": v(-65.67, -19.08) * mm, "end": v(-65.2, -18.6) * mm});
            skLineSegment(sketch, "E321", {"start": v(-65.2, -18.6) * mm, "end": v(-64.7, -18.16) * mm});
            skLineSegment(sketch, "E322", {"start": v(-64.7, -18.16) * mm, "end": v(-64.45, -17.95) * mm});
            skLineSegment(sketch, "E323", {"start": v(-64.45, -17.95) * mm, "end": v(-64.32, -17.85) * mm});
            skLineSegment(sketch, "E324", {"start": v(-64.32, -17.85) * mm, "end": v(-64.2, -17.75) * mm});
            skLineSegment(sketch, "E325", {"start": v(-64.2, -17.75) * mm, "end": v(-65.28, -15.26) * mm});
            skLineSegment(sketch, "E326", {"start": v(-65.28, -15.26) * mm, "end": v(-65.44, -15.29) * mm});
            skLineSegment(sketch, "E327", {"start": v(-65.44, -15.29) * mm, "end": v(-65.6, -15.31) * mm});
            skLineSegment(sketch, "E328", {"start": v(-65.6, -15.31) * mm, "end": v(-65.93, -15.35) * mm});
            skLineSegment(sketch, "E329", {"start": v(-65.93, -15.35) * mm, "end": v(-66.59, -15.4) * mm});
            skLineSegment(sketch, "E330", {"start": v(-66.59, -15.4) * mm, "end": v(-67.26, -15.44) * mm});
            skLineSegment(sketch, "E331", {"start": v(-67.26, -15.44) * mm, "end": v(-67.94, -15.44) * mm});
            skLineSegment(sketch, "E332", {"start": v(-67.94, -15.44) * mm, "end": v(-68.63, -15.42) * mm});
            skLineSegment(sketch, "E333", {"start": v(-68.63, -15.42) * mm, "end": v(-69.33, -15.37) * mm});
            skLineSegment(sketch, "E334", {"start": v(-69.33, -15.37) * mm, "end": v(-70.14, -13.01) * mm});
            skLineSegment(sketch, "E335", {"start": v(-70.14, -13.01) * mm, "end": v(-69.62, -12.54) * mm});
            skLineSegment(sketch, "E336", {"start": v(-69.62, -12.54) * mm, "end": v(-69.1, -12.1) * mm});
            skLineSegment(sketch, "E337", {"start": v(-69.1, -12.1) * mm, "end": v(-68.56, -11.68) * mm});
            skLineSegment(sketch, "E338", {"start": v(-68.56, -11.68) * mm, "end": v(-68.01, -11.3) * mm});
            skLineSegment(sketch, "E339", {"start": v(-68.01, -11.3) * mm, "end": v(-67.46, -10.93) * mm});
            skLineSegment(sketch, "E340", {"start": v(-67.46, -10.93) * mm, "end": v(-67.18, -10.76) * mm});
            skLineSegment(sketch, "E341", {"start": v(-67.18, -10.76) * mm, "end": v(-67.03, -10.68) * mm});
            skLineSegment(sketch, "E342", {"start": v(-67.03, -10.68) * mm, "end": v(-66.9, -10.6) * mm});
            skLineSegment(sketch, "E343", {"start": v(-66.9, -10.6) * mm, "end": v(-67.57, -7.97) * mm});
            skLineSegment(sketch, "E344", {"start": v(-67.57, -7.97) * mm, "end": v(-67.74, -7.98) * mm});
            skLineSegment(sketch, "E345", {"start": v(-67.74, -7.98) * mm, "end": v(-67.9, -7.97) * mm});
            skLineSegment(sketch, "E346", {"start": v(-67.9, -7.97) * mm, "end": v(-68.23, -7.96) * mm});
            skLineSegment(sketch, "E347", {"start": v(-68.23, -7.96) * mm, "end": v(-68.9, -7.92) * mm});
            skLineSegment(sketch, "E348", {"start": v(-68.9, -7.92) * mm, "end": v(-69.56, -7.84) * mm});
            skLineSegment(sketch, "E349", {"start": v(-69.56, -7.84) * mm, "end": v(-70.23, -7.74) * mm});
            skLineSegment(sketch, "E350", {"start": v(-70.23, -7.74) * mm, "end": v(-70.9, -7.6) * mm});
            skLineSegment(sketch, "E351", {"start": v(-70.9, -7.6) * mm, "end": v(-71.59, -7.45) * mm});
            skLineSegment(sketch, "E352", {"start": v(-71.59, -7.45) * mm, "end": v(-72.03, -5) * mm});
            skLineSegment(sketch, "E353", {"start": v(-72.03, -5) * mm, "end": v(-71.44, -4.61) * mm});
            skLineSegment(sketch, "E354", {"start": v(-71.44, -4.61) * mm, "end": v(-70.85, -4.26) * mm});
            skLineSegment(sketch, "E355", {"start": v(-70.85, -4.26) * mm, "end": v(-70.25, -3.93) * mm});
            skLineSegment(sketch, "E356", {"start": v(-70.25, -3.93) * mm, "end": v(-69.65, -3.63) * mm});
            skLineSegment(sketch, "E357", {"start": v(-69.65, -3.63) * mm, "end": v(-69.05, -3.36) * mm});
            skLineSegment(sketch, "E358", {"start": v(-69.05, -3.36) * mm, "end": v(-68.74, -3.23) * mm});
            skLineSegment(sketch, "E359", {"start": v(-68.74, -3.23) * mm, "end": v(-68.6, -3.17) * mm});
            skLineSegment(sketch, "E360", {"start": v(-68.6, -3.17) * mm, "end": v(-68.44, -3.12) * mm});
            skLineSegment(sketch, "E361", {"start": v(-68.44, -3.12) * mm, "end": v(-68.7, -0.42) * mm});
            skLineSegment(sketch, "E362", {"start": v(-68.7, -0.42) * mm, "end": v(-68.86, -0.4) * mm});
            skLineSegment(sketch, "E363", {"start": v(-68.86, -0.4) * mm, "end": v(-69.02, -0.37) * mm});
            skLineSegment(sketch, "E364", {"start": v(-69.02, -0.37) * mm, "end": v(-69.35, -0.3) * mm});
            skLineSegment(sketch, "E365", {"start": v(-69.35, -0.3) * mm, "end": v(-70, -0.16) * mm});
            skLineSegment(sketch, "E366", {"start": v(-70, -0.16) * mm, "end": v(-70.64, 0.02) * mm});
            skLineSegment(sketch, "E367", {"start": v(-70.64, 0.02) * mm, "end": v(-71.29, 0.23) * mm});
            skLineSegment(sketch, "E368", {"start": v(-71.29, 0.23) * mm, "end": v(-71.94, 0.47) * mm});
            skLineSegment(sketch, "E369", {"start": v(-71.94, 0.47) * mm, "end": v(-72.58, 0.72) * mm});
            skLineSegment(sketch, "E370", {"start": v(-72.58, 0.72) * mm, "end": v(-72.63, 3.22) * mm});
            skLineSegment(sketch, "E371", {"start": v(-72.63, 3.22) * mm, "end": v(-72, 3.5) * mm});
            skLineSegment(sketch, "E372", {"start": v(-72, 3.5) * mm, "end": v(-71.35, 3.76) * mm});
            skLineSegment(sketch, "E373", {"start": v(-71.35, 3.76) * mm, "end": v(-70.71, 4) * mm});
            skLineSegment(sketch, "E374", {"start": v(-70.71, 4) * mm, "end": v(-70.07, 4.2) * mm});
            skLineSegment(sketch, "E375", {"start": v(-70.07, 4.2) * mm, "end": v(-69.43, 4.37) * mm});
            skLineSegment(sketch, "E376", {"start": v(-69.43, 4.37) * mm, "end": v(-69.11, 4.45) * mm});
            skLineSegment(sketch, "E377", {"start": v(-69.11, 4.45) * mm, "end": v(-68.95, 4.48) * mm});
            skLineSegment(sketch, "E378", {"start": v(-68.95, 4.48) * mm, "end": v(-68.8, 4.51) * mm});
            skLineSegment(sketch, "E379", {"start": v(-68.8, 4.51) * mm, "end": v(-68.63, 7.22) * mm});
            skLineSegment(sketch, "E380", {"start": v(-68.63, 7.22) * mm, "end": v(-68.79, 7.27) * mm});
            skLineSegment(sketch, "E381", {"start": v(-68.79, 7.27) * mm, "end": v(-68.94, 7.32) * mm});
            skLineSegment(sketch, "E382", {"start": v(-68.94, 7.32) * mm, "end": v(-69.25, 7.43) * mm});
            skLineSegment(sketch, "E383", {"start": v(-69.25, 7.43) * mm, "end": v(-69.87, 7.68) * mm});
            skLineSegment(sketch, "E384", {"start": v(-69.87, 7.68) * mm, "end": v(-70.48, 7.96) * mm});
            skLineSegment(sketch, "E385", {"start": v(-70.48, 7.96) * mm, "end": v(-71.09, 8.27) * mm});
            skLineSegment(sketch, "E386", {"start": v(-71.09, 8.27) * mm, "end": v(-71.69, 8.6) * mm});
            skLineSegment(sketch, "E387", {"start": v(-71.69, 8.6) * mm, "end": v(-72.29, 8.96) * mm});
            skLineSegment(sketch, "E388", {"start": v(-72.29, 8.96) * mm, "end": v(-71.94, 11.43) * mm});
            skLineSegment(sketch, "E389", {"start": v(-71.94, 11.43) * mm, "end": v(-71.27, 11.61) * mm});
            skLineSegment(sketch, "E390", {"start": v(-71.27, 11.61) * mm, "end": v(-70.6, 11.77) * mm});
            skLineSegment(sketch, "E391", {"start": v(-70.6, 11.77) * mm, "end": v(-69.93, 11.9) * mm});
            skLineSegment(sketch, "E392", {"start": v(-69.93, 11.9) * mm, "end": v(-69.27, 12) * mm});
            skLineSegment(sketch, "E393", {"start": v(-69.27, 12) * mm, "end": v(-68.6, 12.07) * mm});
            skLineSegment(sketch, "E394", {"start": v(-68.6, 12.07) * mm, "end": v(-68.28, 12.1) * mm});
            skLineSegment(sketch, "E395", {"start": v(-68.28, 12.1) * mm, "end": v(-68.12, 12.1) * mm});
            skLineSegment(sketch, "E396", {"start": v(-68.12, 12.1) * mm, "end": v(-67.95, 12.1) * mm});
            skLineSegment(sketch, "E397", {"start": v(-67.95, 12.1) * mm, "end": v(-67.37, 14.75) * mm});
            skLineSegment(sketch, "E398", {"start": v(-67.37, 14.75) * mm, "end": v(-67.52, 14.83) * mm});
            skLineSegment(sketch, "E399", {"start": v(-67.52, 14.83) * mm, "end": v(-67.66, 14.9) * mm});
            skLineSegment(sketch, "E400", {"start": v(-67.66, 14.9) * mm, "end": v(-67.95, 15.06) * mm});
            skLineSegment(sketch, "E401", {"start": v(-67.95, 15.06) * mm, "end": v(-68.52, 15.4) * mm});
            skLineSegment(sketch, "E402", {"start": v(-68.52, 15.4) * mm, "end": v(-69.08, 15.78) * mm});
            skLineSegment(sketch, "E403", {"start": v(-69.08, 15.78) * mm, "end": v(-69.63, 16.17) * mm});
            skLineSegment(sketch, "E404", {"start": v(-69.63, 16.17) * mm, "end": v(-70.17, 16.6) * mm});
            skLineSegment(sketch, "E405", {"start": v(-70.17, 16.6) * mm, "end": v(-70.7, 17.04) * mm});
            skLineSegment(sketch, "E406", {"start": v(-70.7, 17.04) * mm, "end": v(-69.98, 19.43) * mm});
            skLineSegment(sketch, "E407", {"start": v(-69.98, 19.43) * mm, "end": v(-69.29, 19.5) * mm});
            skLineSegment(sketch, "E408", {"start": v(-69.29, 19.5) * mm, "end": v(-68.6, 19.55) * mm});
            skLineSegment(sketch, "E409", {"start": v(-68.6, 19.55) * mm, "end": v(-67.92, 19.58) * mm});
            skLineSegment(sketch, "E410", {"start": v(-67.92, 19.58) * mm, "end": v(-67.25, 19.57) * mm});
            skLineSegment(sketch, "E411", {"start": v(-67.25, 19.57) * mm, "end": v(-66.59, 19.54) * mm});
            skLineSegment(sketch, "E412", {"start": v(-66.59, 19.54) * mm, "end": v(-66.26, 19.51) * mm});
            skLineSegment(sketch, "E413", {"start": v(-66.26, 19.51) * mm, "end": v(-66.1, 19.5) * mm});
            skLineSegment(sketch, "E414", {"start": v(-66.1, 19.5) * mm, "end": v(-65.93, 19.47) * mm});
            skLineSegment(sketch, "E415", {"start": v(-65.93, 19.47) * mm, "end": v(-64.94, 22) * mm});
            skLineSegment(sketch, "E416", {"start": v(-64.94, 22) * mm, "end": v(-65.08, 22.1) * mm});
            skLineSegment(sketch, "E417", {"start": v(-65.08, 22.1) * mm, "end": v(-65.2, 22.2) * mm});
            skLineSegment(sketch, "E418", {"start": v(-65.2, 22.2) * mm, "end": v(-65.47, 22.4) * mm});
            skLineSegment(sketch, "E419", {"start": v(-65.47, 22.4) * mm, "end": v(-65.97, 22.82) * mm});
            skLineSegment(sketch, "E420", {"start": v(-65.97, 22.82) * mm, "end": v(-66.47, 23.27) * mm});
            skLineSegment(sketch, "E421", {"start": v(-66.47, 23.27) * mm, "end": v(-66.95, 23.75) * mm});
            skLineSegment(sketch, "E422", {"start": v(-66.95, 23.75) * mm, "end": v(-67.42, 24.25) * mm});
            skLineSegment(sketch, "E423", {"start": v(-67.42, 24.25) * mm, "end": v(-67.88, 24.78) * mm});
            skLineSegment(sketch, "E424", {"start": v(-67.88, 24.78) * mm, "end": v(-66.8, 27.03) * mm});
            skLineSegment(sketch, "E425", {"start": v(-66.8, 27.03) * mm, "end": v(-66.1, 27) * mm});
            skLineSegment(sketch, "E426", {"start": v(-66.1, 27) * mm, "end": v(-65.4, 26.93) * mm});
            skLineSegment(sketch, "E427", {"start": v(-65.4, 26.93) * mm, "end": v(-64.73, 26.85) * mm});
            skLineSegment(sketch, "E428", {"start": v(-64.73, 26.85) * mm, "end": v(-64.07, 26.74) * mm});
            skLineSegment(sketch, "E429", {"start": v(-64.07, 26.74) * mm, "end": v(-63.42, 26.6) * mm});
            skLineSegment(sketch, "E430", {"start": v(-63.42, 26.6) * mm, "end": v(-63.1, 26.52) * mm});
            skLineSegment(sketch, "E431", {"start": v(-63.1, 26.52) * mm, "end": v(-62.94, 26.48) * mm});
            skLineSegment(sketch, "E432", {"start": v(-62.94, 26.48) * mm, "end": v(-62.79, 26.43) * mm});
            skLineSegment(sketch, "E433", {"start": v(-62.79, 26.43) * mm, "end": v(-61.41, 28.77) * mm});
            skLineSegment(sketch, "E434", {"start": v(-61.41, 28.77) * mm, "end": v(-61.53, 28.89) * mm});
            skLineSegment(sketch, "E435", {"start": v(-61.53, 28.89) * mm, "end": v(-61.64, 29) * mm});
            skLineSegment(sketch, "E436", {"start": v(-61.64, 29) * mm, "end": v(-61.87, 29.24) * mm});
            skLineSegment(sketch, "E437", {"start": v(-61.87, 29.24) * mm, "end": v(-62.3, 29.75) * mm});
            skLineSegment(sketch, "E438", {"start": v(-62.3, 29.75) * mm, "end": v(-62.72, 30.27) * mm});
            skLineSegment(sketch, "E439", {"start": v(-62.72, 30.27) * mm, "end": v(-63.12, 30.82) * mm});
            skLineSegment(sketch, "E440", {"start": v(-63.12, 30.82) * mm, "end": v(-63.51, 31.4) * mm});
            skLineSegment(sketch, "E441", {"start": v(-63.51, 31.4) * mm, "end": v(-63.88, 31.98) * mm});
            skLineSegment(sketch, "E442", {"start": v(-63.88, 31.98) * mm, "end": v(-62.45, 34.03) * mm});
            skLineSegment(sketch, "E443", {"start": v(-62.45, 34.03) * mm, "end": v(-61.77, 33.88) * mm});
            skLineSegment(sketch, "E444", {"start": v(-61.77, 33.88) * mm, "end": v(-61.1, 33.72) * mm});
            skLineSegment(sketch, "E445", {"start": v(-61.1, 33.72) * mm, "end": v(-60.45, 33.53) * mm});
            skLineSegment(sketch, "E446", {"start": v(-60.45, 33.53) * mm, "end": v(-59.81, 33.32) * mm});
            skLineSegment(sketch, "E447", {"start": v(-59.81, 33.32) * mm, "end": v(-59.2, 33.08) * mm});
            skLineSegment(sketch, "E448", {"start": v(-59.2, 33.08) * mm, "end": v(-58.89, 32.95) * mm});
            skLineSegment(sketch, "E449", {"start": v(-58.89, 32.95) * mm, "end": v(-58.74, 32.89) * mm});
            skLineSegment(sketch, "E450", {"start": v(-58.74, 32.89) * mm, "end": v(-58.6, 32.82) * mm});
            skLineSegment(sketch, "E451", {"start": v(-58.6, 32.82) * mm, "end": v(-56.87, 34.91) * mm});
            skLineSegment(sketch, "E452", {"start": v(-56.87, 34.91) * mm, "end": v(-56.96, 35.04) * mm});
            skLineSegment(sketch, "E453", {"start": v(-56.96, 35.04) * mm, "end": v(-57.06, 35.18) * mm});
            skLineSegment(sketch, "E454", {"start": v(-57.06, 35.18) * mm, "end": v(-57.24, 35.45) * mm});
            skLineSegment(sketch, "E455", {"start": v(-57.24, 35.45) * mm, "end": v(-57.6, 36.01) * mm});
            skLineSegment(sketch, "E456", {"start": v(-57.6, 36.01) * mm, "end": v(-57.93, 36.6) * mm});
            skLineSegment(sketch, "E457", {"start": v(-57.93, 36.6) * mm, "end": v(-58.24, 37.2) * mm});
            skLineSegment(sketch, "E458", {"start": v(-58.24, 37.2) * mm, "end": v(-58.53, 37.83) * mm});
            skLineSegment(sketch, "E459", {"start": v(-58.53, 37.83) * mm, "end": v(-58.8, 38.47) * mm});
            skLineSegment(sketch, "E460", {"start": v(-58.8, 38.47) * mm, "end": v(-57.07, 40.27) * mm});
            skLineSegment(sketch, "E461", {"start": v(-57.07, 40.27) * mm, "end": v(-56.42, 40.02) * mm});
            skLineSegment(sketch, "E462", {"start": v(-56.42, 40.02) * mm, "end": v(-55.79, 39.75) * mm});
            skLineSegment(sketch, "E463", {"start": v(-55.79, 39.75) * mm, "end": v(-55.17, 39.46) * mm});
            skLineSegment(sketch, "E464", {"start": v(-55.17, 39.46) * mm, "end": v(-54.57, 39.15) * mm});
            skLineSegment(sketch, "E465", {"start": v(-54.57, 39.15) * mm, "end": v(-54, 38.82) * mm});
            skLineSegment(sketch, "E466", {"start": v(-54, 38.82) * mm, "end": v(-53.72, 38.65) * mm});
            skLineSegment(sketch, "E467", {"start": v(-53.72, 38.65) * mm, "end": v(-53.58, 38.56) * mm});
            skLineSegment(sketch, "E468", {"start": v(-53.58, 38.56) * mm, "end": v(-53.45, 38.47) * mm});
            skLineSegment(sketch, "E469", {"start": v(-53.45, 38.47) * mm, "end": v(-51.42, 40.27) * mm});
            skLineSegment(sketch, "E470", {"start": v(-51.42, 40.27) * mm, "end": v(-51.5, 40.41) * mm});
            skLineSegment(sketch, "E471", {"start": v(-51.5, 40.41) * mm, "end": v(-51.57, 40.56) * mm});
            skLineSegment(sketch, "E472", {"start": v(-51.57, 40.56) * mm, "end": v(-51.7, 40.85) * mm});
            skLineSegment(sketch, "E473", {"start": v(-51.7, 40.85) * mm, "end": v(-51.96, 41.47) * mm});
            skLineSegment(sketch, "E474", {"start": v(-51.96, 41.47) * mm, "end": v(-52.2, 42.1) * mm});
            skLineSegment(sketch, "E475", {"start": v(-52.2, 42.1) * mm, "end": v(-52.41, 42.74) * mm});
            skLineSegment(sketch, "E476", {"start": v(-52.41, 42.74) * mm, "end": v(-52.6, 43.4) * mm});
            skLineSegment(sketch, "E477", {"start": v(-52.6, 43.4) * mm, "end": v(-52.78, 44.08) * mm});
            skLineSegment(sketch, "E478", {"start": v(-52.78, 44.08) * mm, "end": v(-50.78, 45.59) * mm});
            skLineSegment(sketch, "E479", {"start": v(-50.78, 45.59) * mm, "end": v(-50.18, 45.24) * mm});
            skLineSegment(sketch, "E480", {"start": v(-50.18, 45.24) * mm, "end": v(-49.6, 44.87) * mm});
            skLineSegment(sketch, "E481", {"start": v(-49.6, 44.87) * mm, "end": v(-49.03, 44.49) * mm});
            skLineSegment(sketch, "E482", {"start": v(-49.03, 44.49) * mm, "end": v(-48.49, 44.1) * mm});
            skLineSegment(sketch, "E483", {"start": v(-48.49, 44.1) * mm, "end": v(-47.97, 43.68) * mm});
            skLineSegment(sketch, "E484", {"start": v(-47.97, 43.68) * mm, "end": v(-47.72, 43.46) * mm});
            skLineSegment(sketch, "E485", {"start": v(-47.72, 43.46) * mm, "end": v(-47.6, 43.35) * mm});
            skLineSegment(sketch, "E486", {"start": v(-47.6, 43.35) * mm, "end": v(-47.48, 43.24) * mm});
            skLineSegment(sketch, "E487", {"start": v(-47.48, 43.24) * mm, "end": v(-45.2, 44.7) * mm});
            skLineSegment(sketch, "E488", {"start": v(-45.2, 44.7) * mm, "end": v(-45.25, 44.85) * mm});
            skLineSegment(sketch, "E489", {"start": v(-45.25, 44.85) * mm, "end": v(-45.3, 45.01) * mm});
            skLineSegment(sketch, "E490", {"start": v(-45.3, 45.01) * mm, "end": v(-45.39, 45.33) * mm});
            skLineSegment(sketch, "E491", {"start": v(-45.39, 45.33) * mm, "end": v(-45.55, 45.97) * mm});
            skLineSegment(sketch, "E492", {"start": v(-45.55, 45.97) * mm, "end": v(-45.68, 46.63) * mm});
            skLineSegment(sketch, "E493", {"start": v(-45.68, 46.63) * mm, "end": v(-45.8, 47.3) * mm});
            skLineSegment(sketch, "E494", {"start": v(-45.8, 47.3) * mm, "end": v(-45.88, 47.98) * mm});
            skLineSegment(sketch, "E495", {"start": v(-45.88, 47.98) * mm, "end": v(-45.94, 48.68) * mm});
            skLineSegment(sketch, "E496", {"start": v(-45.94, 48.68) * mm, "end": v(-43.74, 49.86) * mm});
            skLineSegment(sketch, "E497", {"start": v(-43.74, 49.86) * mm, "end": v(-43.2, 49.42) * mm});
            skLineSegment(sketch, "E498", {"start": v(-43.2, 49.42) * mm, "end": v(-42.68, 48.96) * mm});
            skLineSegment(sketch, "E499", {"start": v(-42.68, 48.96) * mm, "end": v(-42.18, 48.5) * mm});
            skLineSegment(sketch, "E500", {"start": v(-42.18, 48.5) * mm, "end": v(-41.7, 48.02) * mm});
            skLineSegment(sketch, "E501", {"start": v(-41.7, 48.02) * mm, "end": v(-41.26, 47.53) * mm});
            skLineSegment(sketch, "E502", {"start": v(-41.26, 47.53) * mm, "end": v(-41.05, 47.28) * mm});
            skLineSegment(sketch, "E503", {"start": v(-41.05, 47.28) * mm, "end": v(-40.95, 47.15) * mm});
            skLineSegment(sketch, "E504", {"start": v(-40.95, 47.15) * mm, "end": v(-40.85, 47.02) * mm});
            skLineSegment(sketch, "E505", {"start": v(-40.85, 47.02) * mm, "end": v(-38.36, 48.1) * mm});
            skLineSegment(sketch, "E506", {"start": v(-38.36, 48.1) * mm, "end": v(-38.39, 48.27) * mm});
            skLineSegment(sketch, "E507", {"start": v(-38.39, 48.27) * mm, "end": v(-38.41, 48.43) * mm});
            skLineSegment(sketch, "E508", {"start": v(-38.41, 48.43) * mm, "end": v(-38.45, 48.75) * mm});
            skLineSegment(sketch, "E509", {"start": v(-38.45, 48.75) * mm, "end": v(-38.5, 49.42) * mm});
            skLineSegment(sketch, "E510", {"start": v(-38.5, 49.42) * mm, "end": v(-38.54, 50.09) * mm});
            skLineSegment(sketch, "E511", {"start": v(-38.54, 50.09) * mm, "end": v(-38.54, 50.77) * mm});
            skLineSegment(sketch, "E512", {"start": v(-38.54, 50.77) * mm, "end": v(-38.52, 51.46) * mm});
            skLineSegment(sketch, "E513", {"start": v(-38.52, 51.46) * mm, "end": v(-38.47, 52.15) * mm});
            skLineSegment(sketch, "E514", {"start": v(-38.47, 52.15) * mm, "end": v(-36.11, 52.97) * mm});
            skLineSegment(sketch, "E515", {"start": v(-36.11, 52.97) * mm, "end": v(-35.64, 52.45) * mm});
            skLineSegment(sketch, "E516", {"start": v(-35.64, 52.45) * mm, "end": v(-35.2, 51.92) * mm});
            skLineSegment(sketch, "E517", {"start": v(-35.2, 51.92) * mm, "end": v(-34.78, 51.39) * mm});
            skLineSegment(sketch, "E518", {"start": v(-34.78, 51.39) * mm, "end": v(-34.4, 50.84) * mm});
            skLineSegment(sketch, "E519", {"start": v(-34.4, 50.84) * mm, "end": v(-34.03, 50.28) * mm});
            skLineSegment(sketch, "E520", {"start": v(-34.03, 50.28) * mm, "end": v(-33.86, 50) * mm});
            skLineSegment(sketch, "E521", {"start": v(-33.86, 50) * mm, "end": v(-33.78, 49.86) * mm});
            skLineSegment(sketch, "E522", {"start": v(-33.78, 49.86) * mm, "end": v(-33.7, 49.72) * mm});
            skLineSegment(sketch, "E523", {"start": v(-33.7, 49.72) * mm, "end": v(-31.07, 50.4) * mm});
            skLineSegment(sketch, "E524", {"start": v(-31.07, 50.4) * mm, "end": v(-31.07, 50.56) * mm});
            skLineSegment(sketch, "E525", {"start": v(-31.07, 50.56) * mm, "end": v(-31.07, 50.73) * mm});
            skLineSegment(sketch, "E526", {"start": v(-31.07, 50.73) * mm, "end": v(-31.06, 51.06) * mm});
            skLineSegment(sketch, "E527", {"start": v(-31.06, 51.06) * mm, "end": v(-31.02, 51.72) * mm});
            skLineSegment(sketch, "E528", {"start": v(-31.02, 51.72) * mm, "end": v(-30.94, 52.39) * mm});
            skLineSegment(sketch, "E529", {"start": v(-30.94, 52.39) * mm, "end": v(-30.84, 53.06) * mm});
            skLineSegment(sketch, "E530", {"start": v(-30.84, 53.06) * mm, "end": v(-30.7, 53.73) * mm});
            skLineSegment(sketch, "E531", {"start": v(-30.7, 53.73) * mm, "end": v(-30.55, 54.42) * mm});
            skLineSegment(sketch, "E532", {"start": v(-30.55, 54.42) * mm, "end": v(-28.1, 54.85) * mm});
            skLineSegment(sketch, "E533", {"start": v(-28.1, 54.85) * mm, "end": v(-27.71, 54.27) * mm});
            skLineSegment(sketch, "E534", {"start": v(-27.71, 54.27) * mm, "end": v(-27.36, 53.68) * mm});
            skLineSegment(sketch, "E535", {"start": v(-27.36, 53.68) * mm, "end": v(-27.03, 53.08) * mm});
            skLineSegment(sketch, "E536", {"start": v(-27.03, 53.08) * mm, "end": v(-26.73, 52.48) * mm});
            skLineSegment(sketch, "E537", {"start": v(-26.73, 52.48) * mm, "end": v(-26.45, 51.88) * mm});
            skLineSegment(sketch, "E538", {"start": v(-26.45, 51.88) * mm, "end": v(-26.33, 51.57) * mm});
            skLineSegment(sketch, "E539", {"start": v(-26.33, 51.57) * mm, "end": v(-26.27, 51.42) * mm});
            skLineSegment(sketch, "E540", {"start": v(-26.27, 51.42) * mm, "end": v(-26.22, 51.26) * mm});
            skLineSegment(sketch, "E541", {"start": v(-26.22, 51.26) * mm, "end": v(-23.52, 51.53) * mm});
            skLineSegment(sketch, "E542", {"start": v(-23.52, 51.53) * mm, "end": v(-23.5, 51.69) * mm});
            skLineSegment(sketch, "E543", {"start": v(-23.5, 51.69) * mm, "end": v(-23.47, 51.85) * mm});
            skLineSegment(sketch, "E544", {"start": v(-23.47, 51.85) * mm, "end": v(-23.4, 52.17) * mm});
            skLineSegment(sketch, "E545", {"start": v(-23.4, 52.17) * mm, "end": v(-23.25, 52.82) * mm});
            skLineSegment(sketch, "E546", {"start": v(-23.25, 52.82) * mm, "end": v(-23.07, 53.47) * mm});
            skLineSegment(sketch, "E547", {"start": v(-23.07, 53.47) * mm, "end": v(-22.87, 54.12) * mm});
            skLineSegment(sketch, "E548", {"start": v(-22.87, 54.12) * mm, "end": v(-22.63, 54.76) * mm});
            skLineSegment(sketch, "E549", {"start": v(-22.63, 54.76) * mm, "end": v(-22.38, 55.41) * mm});
            skLineSegment(sketch, "E550", {"start": v(-22.38, 55.41) * mm, "end": v(-19.88, 55.46) * mm});
            skLineSegment(sketch, "E551", {"start": v(-19.88, 55.46) * mm, "end": v(-19.6, 54.82) * mm});
            skLineSegment(sketch, "E552", {"start": v(-19.6, 54.82) * mm, "end": v(-19.34, 54.18) * mm});
            skLineSegment(sketch, "E553", {"start": v(-19.34, 54.18) * mm, "end": v(-19.1, 53.54) * mm});
            skLineSegment(sketch, "E554", {"start": v(-19.1, 53.54) * mm, "end": v(-18.9, 52.9) * mm});
            skLineSegment(sketch, "E555", {"start": v(-18.9, 52.9) * mm, "end": v(-18.73, 52.26) * mm});
            skLineSegment(sketch, "E556", {"start": v(-18.73, 52.26) * mm, "end": v(-18.65, 51.94) * mm});
            skLineSegment(sketch, "E557", {"start": v(-18.65, 51.94) * mm, "end": v(-18.62, 51.78) * mm});
            skLineSegment(sketch, "E558", {"start": v(-18.62, 51.78) * mm, "end": v(-18.59, 51.62) * mm});
            skLineSegment(sketch, "E559", {"start": v(-18.59, 51.62) * mm, "end": v(-15.88, 51.46) * mm});
            skLineSegment(sketch, "E560", {"start": v(-15.88, 51.46) * mm, "end": v(-15.83, 51.61) * mm});
            skLineSegment(sketch, "E561", {"start": v(-15.83, 51.61) * mm, "end": v(-15.78, 51.77) * mm});
            skLineSegment(sketch, "E562", {"start": v(-15.78, 51.77) * mm, "end": v(-15.67, 52.08) * mm});
            skLineSegment(sketch, "E563", {"start": v(-15.67, 52.08) * mm, "end": v(-15.42, 52.7) * mm});
            skLineSegment(sketch, "E564", {"start": v(-15.42, 52.7) * mm, "end": v(-15.14, 53.3) * mm});
            skLineSegment(sketch, "E565", {"start": v(-15.14, 53.3) * mm, "end": v(-14.83, 53.91) * mm});
            skLineSegment(sketch, "E566", {"start": v(-14.83, 53.91) * mm, "end": v(-14.5, 54.52) * mm});
            skLineSegment(sketch, "E567", {"start": v(-14.5, 54.52) * mm, "end": v(-14.14, 55.12) * mm});
            skLineSegment(sketch, "E568", {"start": v(-14.14, 55.12) * mm, "end": v(-11.67, 54.77) * mm});
            skLineSegment(sketch, "E569", {"start": v(-11.67, 54.77) * mm, "end": v(-11.49, 54.1) * mm});
            skLineSegment(sketch, "E570", {"start": v(-11.49, 54.1) * mm, "end": v(-11.33, 53.43) * mm});
            skLineSegment(sketch, "E571", {"start": v(-11.33, 53.43) * mm, "end": v(-11.2, 52.76) * mm});
            skLineSegment(sketch, "E572", {"start": v(-11.2, 52.76) * mm, "end": v(-11.1, 52.1) * mm});
            skLineSegment(sketch, "E573", {"start": v(-11.1, 52.1) * mm, "end": v(-11.03, 51.43) * mm});
            skLineSegment(sketch, "E574", {"start": v(-11.03, 51.43) * mm, "end": v(-11, 51.1) * mm});
            skLineSegment(sketch, "E575", {"start": v(-11, 51.1) * mm, "end": v(-11, 50.94) * mm});
            skLineSegment(sketch, "E576", {"start": v(-11, 50.94) * mm, "end": v(-11, 50.78) * mm});
            skLineSegment(sketch, "E577", {"start": v(-11, 50.78) * mm, "end": v(-8.35, 50.2) * mm});
            skLineSegment(sketch, "E578", {"start": v(-8.35, 50.2) * mm, "end": v(-8.27, 50.34) * mm});
            skLineSegment(sketch, "E579", {"start": v(-8.27, 50.34) * mm, "end": v(-8.2, 50.49) * mm});
            skLineSegment(sketch, "E580", {"start": v(-8.2, 50.49) * mm, "end": v(-8.04, 50.77) * mm});
            skLineSegment(sketch, "E581", {"start": v(-8.04, 50.77) * mm, "end": v(-7.7, 51.34) * mm});
            skLineSegment(sketch, "E582", {"start": v(-7.7, 51.34) * mm, "end": v(-7.32, 51.9) * mm});
            skLineSegment(sketch, "E583", {"start": v(-7.32, 51.9) * mm, "end": v(-6.93, 52.46) * mm});
            skLineSegment(sketch, "E584", {"start": v(-6.93, 52.46) * mm, "end": v(-6.5, 53) * mm});
            skLineSegment(sketch, "E585", {"start": v(-6.5, 53) * mm, "end": v(-6.06, 53.54) * mm});
            skLineSegment(sketch, "E586", {"start": v(-6.06, 53.54) * mm, "end": v(-3.67, 52.8) * mm});
            skLineSegment(sketch, "E587", {"start": v(-3.67, 52.8) * mm, "end": v(-3.6, 52.11) * mm});
            skLineSegment(sketch, "E588", {"start": v(-3.6, 52.11) * mm, "end": v(-3.55, 51.43) * mm});
            skLineSegment(sketch, "E589", {"start": v(-3.55, 51.43) * mm, "end": v(-3.52, 50.75) * mm});
            skLineSegment(sketch, "E590", {"start": v(-3.52, 50.75) * mm, "end": v(-3.53, 50.08) * mm});
            skLineSegment(sketch, "E591", {"start": v(-3.53, 50.08) * mm, "end": v(-3.56, 49.41) * mm});
            skLineSegment(sketch, "E592", {"start": v(-3.56, 49.41) * mm, "end": v(-3.59, 49.09) * mm});
            skLineSegment(sketch, "E593", {"start": v(-3.59, 49.09) * mm, "end": v(-3.6, 48.92) * mm});
            skLineSegment(sketch, "E594", {"start": v(-3.6, 48.92) * mm, "end": v(-3.63, 48.76) * mm});
            skLineSegment(sketch, "E595", {"start": v(-3.63, 48.76) * mm, "end": v(-1.1, 47.77) * mm});
            skLineSegment(sketch, "E596", {"start": v(-1.1, 47.77) * mm, "end": v(-1, 47.9) * mm});
            skLineSegment(sketch, "E597", {"start": v(-1, 47.9) * mm, "end": v(-0.9, 48.03) * mm});
            skLineSegment(sketch, "E598", {"start": v(-0.9, 48.03) * mm, "end": v(-0.7, 48.3) * mm});
            skLineSegment(sketch, "E599", {"start": v(-0.7, 48.3) * mm, "end": v(-0.28, 48.8) * mm});
            skLineSegment(sketch, "E600", {"start": v(-0.28, 48.8) * mm, "end": v(0.17, 49.3) * mm});
            skLineSegment(sketch, "E601", {"start": v(0.17, 49.3) * mm, "end": v(0.65, 49.78) * mm});
            skLineSegment(sketch, "E602", {"start": v(0.65, 49.78) * mm, "end": v(1.16, 50.25) * mm});
            skLineSegment(sketch, "E603", {"start": v(1.16, 50.25) * mm, "end": v(1.68, 50.71) * mm});
            skLineSegment(sketch, "E604", {"start": v(1.68, 50.71) * mm, "end": v(3.93, 49.62) * mm});
            skLineSegment(sketch, "E605", {"start": v(3.93, 49.62) * mm, "end": v(3.9, 48.92) * mm});
            skLineSegment(sketch, "E606", {"start": v(3.9, 48.92) * mm, "end": v(3.83, 48.24) * mm});
            skLineSegment(sketch, "E607", {"start": v(3.83, 48.24) * mm, "end": v(3.75, 47.56) * mm});
            skLineSegment(sketch, "E608", {"start": v(3.75, 47.56) * mm, "end": v(3.64, 46.9) * mm});
            skLineSegment(sketch, "E609", {"start": v(3.64, 46.9) * mm, "end": v(3.5, 46.25) * mm});
            skLineSegment(sketch, "E610", {"start": v(3.5, 46.25) * mm, "end": v(3.42, 45.93) * mm});
            skLineSegment(sketch, "E611", {"start": v(3.42, 45.93) * mm, "end": v(3.38, 45.77) * mm});
            skLineSegment(sketch, "E612", {"start": v(3.38, 45.77) * mm, "end": v(3.33, 45.61) * mm});
            skLineSegment(sketch, "E613", {"start": v(3.33, 45.61) * mm, "end": v(5.67, 44.24) * mm});
            skLineSegment(sketch, "E614", {"start": v(5.67, 44.24) * mm, "end": v(5.79, 44.36) * mm});
            skLineSegment(sketch, "E615", {"start": v(5.79, 44.36) * mm, "end": v(5.9, 44.47) * mm});
            skLineSegment(sketch, "E616", {"start": v(5.9, 44.47) * mm, "end": v(6.14, 44.7) * mm});
            skLineSegment(sketch, "E617", {"start": v(6.14, 44.7) * mm, "end": v(6.65, 45.13) * mm});
            skLineSegment(sketch, "E618", {"start": v(6.65, 45.13) * mm, "end": v(7.17, 45.55) * mm});
            skLineSegment(sketch, "E619", {"start": v(7.17, 45.55) * mm, "end": v(7.72, 45.95) * mm});
            skLineSegment(sketch, "E620", {"start": v(7.72, 45.95) * mm, "end": v(8.3, 46.34) * mm});
            skLineSegment(sketch, "E621", {"start": v(8.3, 46.34) * mm, "end": v(8.88, 46.71) * mm});
            skLineSegment(sketch, "E622", {"start": v(8.88, 46.71) * mm, "end": v(10.93, 45.28) * mm});
            skLineSegment(sketch, "E623", {"start": v(10.93, 45.28) * mm, "end": v(10.78, 44.6) * mm});
            skLineSegment(sketch, "E624", {"start": v(10.78, 44.6) * mm, "end": v(10.62, 43.93) * mm});
            skLineSegment(sketch, "E625", {"start": v(10.62, 43.93) * mm, "end": v(10.43, 43.28) * mm});
            skLineSegment(sketch, "E626", {"start": v(10.43, 43.28) * mm, "end": v(10.22, 42.64) * mm});
            skLineSegment(sketch, "E627", {"start": v(10.22, 42.64) * mm, "end": v(9.98, 42.02) * mm});
            skLineSegment(sketch, "E628", {"start": v(9.98, 42.02) * mm, "end": v(9.85, 41.71) * mm});
            skLineSegment(sketch, "E629", {"start": v(9.85, 41.71) * mm, "end": v(9.79, 41.57) * mm});
            skLineSegment(sketch, "E630", {"start": v(9.79, 41.57) * mm, "end": v(9.72, 41.42) * mm});
            skLineSegment(sketch, "E631", {"start": v(9.72, 41.42) * mm, "end": v(11.81, 39.7) * mm});
            skLineSegment(sketch, "E632", {"start": v(11.81, 39.7) * mm, "end": v(11.94, 39.8) * mm});
            skLineSegment(sketch, "E633", {"start": v(11.94, 39.8) * mm, "end": v(12.08, 39.89) * mm});
            skLineSegment(sketch, "E634", {"start": v(12.08, 39.89) * mm, "end": v(12.35, 40.07) * mm});
            skLineSegment(sketch, "E635", {"start": v(12.35, 40.07) * mm, "end": v(12.91, 40.42) * mm});
            skLineSegment(sketch, "E636", {"start": v(12.91, 40.42) * mm, "end": v(13.5, 40.75) * mm});
            skLineSegment(sketch, "E637", {"start": v(13.5, 40.75) * mm, "end": v(14.1, 41.06) * mm});
            skLineSegment(sketch, "E638", {"start": v(14.1, 41.06) * mm, "end": v(14.73, 41.36) * mm});
            skLineSegment(sketch, "E639", {"start": v(14.73, 41.36) * mm, "end": v(15.37, 41.63) * mm});
            skLineSegment(sketch, "E640", {"start": v(15.37, 41.63) * mm, "end": v(17.17, 39.9) * mm});
            skLineSegment(sketch, "E641", {"start": v(17.17, 39.9) * mm, "end": v(16.92, 39.25) * mm});
            skLineSegment(sketch, "E642", {"start": v(16.92, 39.25) * mm, "end": v(16.65, 38.61) * mm});
            skLineSegment(sketch, "E643", {"start": v(16.65, 38.61) * mm, "end": v(16.36, 38) * mm});
            skLineSegment(sketch, "E644", {"start": v(16.36, 38) * mm, "end": v(16.05, 37.4) * mm});
            skLineSegment(sketch, "E645", {"start": v(16.05, 37.4) * mm, "end": v(15.72, 36.82) * mm});
            skLineSegment(sketch, "E646", {"start": v(15.72, 36.82) * mm, "end": v(15.55, 36.55) * mm});
            skLineSegment(sketch, "E647", {"start": v(15.55, 36.55) * mm, "end": v(15.46, 36.4) * mm});
            skLineSegment(sketch, "E648", {"start": v(15.46, 36.4) * mm, "end": v(15.37, 36.27) * mm});
            skLineSegment(sketch, "E649", {"start": v(15.37, 36.27) * mm, "end": v(17.17, 34.25) * mm});
            skLineSegment(sketch, "E650", {"start": v(17.17, 34.25) * mm, "end": v(17.31, 34.32) * mm});
            skLineSegment(sketch, "E651", {"start": v(17.31, 34.32) * mm, "end": v(17.46, 34.4) * mm});
            skLineSegment(sketch, "E652", {"start": v(17.46, 34.4) * mm, "end": v(17.75, 34.53) * mm});
            skLineSegment(sketch, "E653", {"start": v(17.75, 34.53) * mm, "end": v(18.37, 34.8) * mm});
            skLineSegment(sketch, "E654", {"start": v(18.37, 34.8) * mm, "end": v(19, 35.03) * mm});
            skLineSegment(sketch, "E655", {"start": v(19, 35.03) * mm, "end": v(19.64, 35.24) * mm});
            skLineSegment(sketch, "E656", {"start": v(19.64, 35.24) * mm, "end": v(20.3, 35.43) * mm});
            skLineSegment(sketch, "E657", {"start": v(20.3, 35.43) * mm, "end": v(20.98, 35.6) * mm});
            skLineSegment(sketch, "E658", {"start": v(20.98, 35.6) * mm, "end": v(22.49, 33.6) * mm});
            skLineSegment(sketch, "E659", {"start": v(22.49, 33.6) * mm, "end": v(22.14, 33) * mm});
            skLineSegment(sketch, "E660", {"start": v(22.14, 33) * mm, "end": v(21.77, 32.42) * mm});
            skLineSegment(sketch, "E661", {"start": v(21.77, 32.42) * mm, "end": v(21.39, 31.86) * mm});
            skLineSegment(sketch, "E662", {"start": v(21.39, 31.86) * mm, "end": v(21, 31.32) * mm});
            skLineSegment(sketch, "E663", {"start": v(21, 31.32) * mm, "end": v(20.58, 30.8) * mm});
            skLineSegment(sketch, "E664", {"start": v(20.58, 30.8) * mm, "end": v(20.36, 30.55) * mm});
            skLineSegment(sketch, "E665", {"start": v(20.36, 30.55) * mm, "end": v(20.25, 30.43) * mm});
            skLineSegment(sketch, "E666", {"start": v(20.25, 30.43) * mm, "end": v(20.14, 30.3) * mm});
            skLineSegment(sketch, "E667", {"start": v(20.14, 30.3) * mm, "end": v(21.6, 28.03) * mm});
            skLineSegment(sketch, "E668", {"start": v(21.6, 28.03) * mm, "end": v(21.75, 28.08) * mm});
            skLineSegment(sketch, "E669", {"start": v(21.75, 28.08) * mm, "end": v(21.91, 28.12) * mm});
            skLineSegment(sketch, "E670", {"start": v(21.91, 28.12) * mm, "end": v(22.23, 28.22) * mm});
            skLineSegment(sketch, "E671", {"start": v(22.23, 28.22) * mm, "end": v(22.87, 28.38) * mm});
            skLineSegment(sketch, "E672", {"start": v(22.87, 28.38) * mm, "end": v(23.53, 28.5) * mm});
            skLineSegment(sketch, "E673", {"start": v(23.53, 28.5) * mm, "end": v(24.2, 28.62) * mm});
            skLineSegment(sketch, "E674", {"start": v(24.2, 28.62) * mm, "end": v(24.88, 28.7) * mm});
            skLineSegment(sketch, "E675", {"start": v(24.88, 28.7) * mm, "end": v(25.58, 28.77) * mm});
            skLineSegment(sketch, "E676", {"start": v(25.58, 28.77) * mm, "end": v(26.76, 26.56) * mm});
            skLineSegment(sketch, "E677", {"start": v(26.76, 26.56) * mm, "end": v(26.32, 26.02) * mm});
            skLineSegment(sketch, "E678", {"start": v(26.32, 26.02) * mm, "end": v(25.86, 25.5) * mm});
            skLineSegment(sketch, "E679", {"start": v(25.86, 25.5) * mm, "end": v(25.4, 25) * mm});
            skLineSegment(sketch, "E680", {"start": v(25.4, 25) * mm, "end": v(24.92, 24.53) * mm});
            skLineSegment(sketch, "E681", {"start": v(24.92, 24.53) * mm, "end": v(24.43, 24.09) * mm});
            skLineSegment(sketch, "E682", {"start": v(24.43, 24.09) * mm, "end": v(24.18, 23.88) * mm});
            skLineSegment(sketch, "E683", {"start": v(24.18, 23.88) * mm, "end": v(24.05, 23.77) * mm});
            skLineSegment(sketch, "E684", {"start": v(24.05, 23.77) * mm, "end": v(23.92, 23.67) * mm});
            skLineSegment(sketch, "E685", {"start": v(23.92, 23.67) * mm, "end": v(25, 21.19) * mm});
            skLineSegment(sketch, "E686", {"start": v(25, 21.19) * mm, "end": v(25.17, 21.21) * mm});
            skLineSegment(sketch, "E687", {"start": v(25.17, 21.21) * mm, "end": v(25.33, 21.24) * mm});
            skLineSegment(sketch, "E688", {"start": v(25.33, 21.24) * mm, "end": v(25.66, 21.28) * mm});
            skLineSegment(sketch, "E689", {"start": v(25.66, 21.28) * mm, "end": v(26.32, 21.34) * mm});
            skLineSegment(sketch, "E690", {"start": v(26.32, 21.34) * mm, "end": v(26.99, 21.36) * mm});
            skLineSegment(sketch, "E691", {"start": v(26.99, 21.36) * mm, "end": v(27.67, 21.37) * mm});
            skLineSegment(sketch, "E692", {"start": v(27.67, 21.37) * mm, "end": v(28.36, 21.35) * mm});
            skLineSegment(sketch, "E693", {"start": v(28.36, 21.35) * mm, "end": v(29.05, 21.3) * mm});
            skLineSegment(sketch, "E694", {"start": v(29.05, 21.3) * mm, "end": v(29.87, 18.94) * mm});
            skLineSegment(sketch, "E695", {"start": v(29.87, 18.94) * mm, "end": v(29.35, 18.47) * mm});
            skLineSegment(sketch, "E696", {"start": v(29.35, 18.47) * mm, "end": v(28.82, 18.03) * mm});
            skLineSegment(sketch, "E697", {"start": v(28.82, 18.03) * mm, "end": v(28.29, 17.61) * mm});
            skLineSegment(sketch, "E698", {"start": v(28.29, 17.61) * mm, "end": v(27.74, 17.22) * mm});
            skLineSegment(sketch, "E699", {"start": v(27.74, 17.22) * mm, "end": v(27.18, 16.86) * mm});
            skLineSegment(sketch, "E700", {"start": v(27.18, 16.86) * mm, "end": v(26.9, 16.69) * mm});
            skLineSegment(sketch, "E701", {"start": v(26.9, 16.69) * mm, "end": v(26.76, 16.6) * mm});
            skLineSegment(sketch, "E702", {"start": v(26.76, 16.6) * mm, "end": v(26.62, 16.53) * mm});
            skLineSegment(sketch, "E703", {"start": v(26.62, 16.53) * mm, "end": v(27.3, 13.9) * mm});
            skLineSegment(sketch, "E704", {"start": v(27.3, 13.9) * mm, "end": v(27.46, 13.9) * mm});
            skLineSegment(sketch, "E705", {"start": v(27.46, 13.9) * mm, "end": v(27.63, 13.9) * mm});
            skLineSegment(sketch, "E706", {"start": v(27.63, 13.9) * mm, "end": v(27.96, 13.89) * mm});
            skLineSegment(sketch, "E707", {"start": v(27.96, 13.89) * mm, "end": v(28.62, 13.84) * mm});
            skLineSegment(sketch, "E708", {"start": v(28.62, 13.84) * mm, "end": v(29.29, 13.77) * mm});
            skLineSegment(sketch, "E709", {"start": v(29.29, 13.77) * mm, "end": v(29.96, 13.66) * mm});
            skLineSegment(sketch, "E710", {"start": v(29.96, 13.66) * mm, "end": v(30.64, 13.53) * mm});
            skLineSegment(sketch, "E711", {"start": v(30.64, 13.53) * mm, "end": v(31.32, 13.38) * mm});
            skLineSegment(sketch, "E712", {"start": v(31.32, 13.38) * mm, "end": v(31.75, 10.92) * mm});
            skLineSegment(sketch, "E713", {"start": v(31.75, 10.92) * mm, "end": v(31.17, 10.54) * mm});
            skLineSegment(sketch, "E714", {"start": v(31.17, 10.54) * mm, "end": v(30.58, 10.18) * mm});
            skLineSegment(sketch, "E715", {"start": v(30.58, 10.18) * mm, "end": v(29.98, 9.86) * mm});
            skLineSegment(sketch, "E716", {"start": v(29.98, 9.86) * mm, "end": v(29.38, 9.55) * mm});
            skLineSegment(sketch, "E717", {"start": v(29.38, 9.55) * mm, "end": v(28.78, 9.28) * mm});
            skLineSegment(sketch, "E718", {"start": v(28.78, 9.28) * mm, "end": v(28.47, 9.16) * mm});
            skLineSegment(sketch, "E719", {"start": v(28.47, 9.16) * mm, "end": v(28.32, 9.1) * mm});
            skLineSegment(sketch, "E720", {"start": v(28.32, 9.1) * mm, "end": v(28.16, 9.04) * mm});
            skLineSegment(sketch, "E721", {"start": v(28.16, 9.04) * mm, "end": v(28.43, 6.35) * mm});
            skLineSegment(sketch, "E722", {"start": v(28.43, 6.35) * mm, "end": v(28.59, 6.32) * mm});
            skLineSegment(sketch, "E723", {"start": v(28.59, 6.32) * mm, "end": v(28.75, 6.3) * mm});
            skLineSegment(sketch, "E724", {"start": v(28.75, 6.3) * mm, "end": v(29.07, 6.23) * mm});
            skLineSegment(sketch, "E725", {"start": v(29.07, 6.23) * mm, "end": v(29.72, 6.08) * mm});
            skLineSegment(sketch, "E726", {"start": v(29.72, 6.08) * mm, "end": v(30.37, 5.9) * mm});
            skLineSegment(sketch, "E727", {"start": v(30.37, 5.9) * mm, "end": v(31.02, 5.7) * mm});
            skLineSegment(sketch, "E728", {"start": v(31.02, 5.7) * mm, "end": v(31.66, 5.46) * mm});
            skLineSegment(sketch, "E729", {"start": v(31.66, 5.46) * mm, "end": v(32.31, 5.2) * mm});
            skLineSegment(sketch, "E730", {"start": v(32.31, 5.2) * mm, "end": v(32.36, 2.7) * mm});
            skLineSegment(sketch, "E731", {"start": v(32.36, 2.7) * mm, "end": v(31.72, 2.42) * mm});
            skLineSegment(sketch, "E732", {"start": v(31.72, 2.42) * mm, "end": v(31.08, 2.16) * mm});
            skLineSegment(sketch, "E733", {"start": v(31.08, 2.16) * mm, "end": v(30.44, 1.93) * mm});
            skLineSegment(sketch, "E734", {"start": v(30.44, 1.93) * mm, "end": v(29.8, 1.73) * mm});
            skLineSegment(sketch, "E735", {"start": v(29.8, 1.73) * mm, "end": v(29.16, 1.55) * mm});
            skLineSegment(sketch, "E736", {"start": v(29.16, 1.55) * mm, "end": v(28.84, 1.48) * mm});
            skLineSegment(sketch, "E737", {"start": v(28.84, 1.48) * mm, "end": v(28.68, 1.44) * mm});
            skLineSegment(sketch, "E738", {"start": v(28.68, 1.44) * mm, "end": v(28.52, 1.41) * mm});
            skLineSegment(sketch, "E739", {"start": v(28.52, 1.41) * mm, "end": v(28.36, -1.3) * mm});
            skCircle(sketch, "E740", {"center": v(-20.14, 2.96) * mm, "radius": 6.35 * mm});
            skLineSegment(sketch, "E741", {"start": v(33.31, -1.98) * mm, "end": v(33.19, -1.83) * mm});
            skLineSegment(sketch, "E742", {"start": v(33.19, -1.83) * mm, "end": v(33.1, -1.8) * mm});
            skLineSegment(sketch, "E743", {"start": v(33.1, -1.8) * mm, "end": v(33.03, -1.77) * mm});
            skLineSegment(sketch, "E744", {"start": v(33.03, -1.77) * mm, "end": v(32.95, -1.75) * mm});
            skLineSegment(sketch, "E745", {"start": v(32.95, -1.75) * mm, "end": v(32.88, -1.75) * mm});
            skLineSegment(sketch, "E746", {"start": v(32.88, -1.75) * mm, "end": v(32.75, -1.74) * mm});
            skLineSegment(sketch, "E747", {"start": v(32.75, -1.74) * mm, "end": v(32.62, -1.76) * mm});
            skLineSegment(sketch, "E748", {"start": v(32.62, -1.76) * mm, "end": v(32.49, -1.78) * mm});
            skLineSegment(sketch, "E749", {"start": v(32.49, -1.78) * mm, "end": v(32.37, -1.8) * mm});
            skLineSegment(sketch, "E750", {"start": v(32.37, -1.8) * mm, "end": v(32.12, -1.88) * mm});
            skLineSegment(sketch, "E751", {"start": v(32.12, -1.88) * mm, "end": v(31.87, -1.92) * mm});
            skLineSegment(sketch, "E752", {"start": v(31.87, -1.92) * mm, "end": v(31.6, -1.95) * mm});
            skLineSegment(sketch, "E753", {"start": v(31.6, -1.95) * mm, "end": v(31.34, -1.95) * mm});
            skLineSegment(sketch, "E754", {"start": v(31.34, -1.95) * mm, "end": v(31.07, -1.94) * mm});
            skLineSegment(sketch, "E755", {"start": v(31.07, -1.94) * mm, "end": v(30.8, -1.92) * mm});
            skLineSegment(sketch, "E756", {"start": v(30.8, -1.92) * mm, "end": v(30.51, -1.89) * mm});
            skLineSegment(sketch, "E757", {"start": v(30.51, -1.89) * mm, "end": v(30.23, -1.84) * mm});
            skLineSegment(sketch, "E758", {"start": v(30.23, -1.84) * mm, "end": v(29.95, -1.78) * mm});
            skLineSegment(sketch, "E759", {"start": v(29.95, -1.78) * mm, "end": v(29.66, -1.71) * mm});
            skLineSegment(sketch, "E760", {"start": v(29.66, -1.71) * mm, "end": v(29.37, -1.63) * mm});
            skLineSegment(sketch, "E761", {"start": v(29.37, -1.63) * mm, "end": v(29.16, -1.57) * mm});
            skLineSegment(sketch, "E762", {"start": v(29.16, -1.57) * mm, "end": v(28.69, 0.76) * mm});
            skLineSegment(sketch, "E763", {"start": v(28.69, 0.76) * mm, "end": v(28.86, 0.9) * mm});
            skLineSegment(sketch, "E764", {"start": v(28.86, 0.9) * mm, "end": v(29.1, 1.09) * mm});
            skLineSegment(sketch, "E765", {"start": v(29.1, 1.09) * mm, "end": v(29.33, 1.26) * mm});
            skLineSegment(sketch, "E766", {"start": v(29.33, 1.26) * mm, "end": v(29.57, 1.43) * mm});
            skLineSegment(sketch, "E767", {"start": v(29.57, 1.43) * mm, "end": v(29.81, 1.58) * mm});
            skLineSegment(sketch, "E768", {"start": v(29.81, 1.58) * mm, "end": v(30.06, 1.72) * mm});
            skLineSegment(sketch, "E769", {"start": v(30.06, 1.72) * mm, "end": v(30.3, 1.84) * mm});
            skLineSegment(sketch, "E770", {"start": v(30.3, 1.84) * mm, "end": v(30.55, 1.96) * mm});
            skLineSegment(sketch, "E771", {"start": v(30.55, 1.96) * mm, "end": v(30.8, 2.06) * mm});
            skLineSegment(sketch, "E772", {"start": v(30.8, 2.06) * mm, "end": v(31.05, 2.14) * mm});
            skLineSegment(sketch, "E773", {"start": v(31.05, 2.14) * mm, "end": v(31.3, 2.2) * mm});
            skLineSegment(sketch, "E774", {"start": v(31.3, 2.2) * mm, "end": v(31.55, 2.22) * mm});
            skLineSegment(sketch, "E775", {"start": v(31.55, 2.22) * mm, "end": v(31.68, 2.24) * mm});
            skLineSegment(sketch, "E776", {"start": v(31.68, 2.24) * mm, "end": v(31.8, 2.27) * mm});
            skLineSegment(sketch, "E777", {"start": v(31.8, 2.27) * mm, "end": v(31.93, 2.31) * mm});
            skLineSegment(sketch, "E778", {"start": v(31.93, 2.31) * mm, "end": v(32.05, 2.37) * mm});
            skLineSegment(sketch, "E779", {"start": v(32.05, 2.37) * mm, "end": v(32.12, 2.4) * mm});
            skLineSegment(sketch, "E780", {"start": v(32.12, 2.4) * mm, "end": v(32.18, 2.44) * mm});
            skLineSegment(sketch, "E781", {"start": v(32.18, 2.44) * mm, "end": v(32.24, 2.5) * mm});
            skLineSegment(sketch, "E782", {"start": v(32.24, 2.5) * mm, "end": v(32.3, 2.56) * mm});
            skLineSegment(sketch, "E783", {"start": v(32.3, 2.56) * mm, "end": v(32.36, 2.74) * mm});
            skLineSegment(sketch, "E784", {"start": v(32.36, 2.74) * mm, "end": v(32.39, 3.8) * mm});
            skLineSegment(sketch, "E785", {"start": v(32.39, 3.8) * mm, "end": v(32.5, 4.84) * mm});
            skLineSegment(sketch, "E786", {"start": v(32.5, 4.84) * mm, "end": v(32.46, 5.03) * mm});
            skLineSegment(sketch, "E787", {"start": v(32.46, 5.03) * mm, "end": v(32.4, 5.1) * mm});
            skLineSegment(sketch, "E788", {"start": v(32.4, 5.1) * mm, "end": v(32.35, 5.17) * mm});
            skLineSegment(sketch, "E789", {"start": v(32.35, 5.17) * mm, "end": v(32.3, 5.22) * mm});
            skLineSegment(sketch, "E790", {"start": v(32.3, 5.22) * mm, "end": v(32.24, 5.26) * mm});
            skLineSegment(sketch, "E791", {"start": v(32.24, 5.26) * mm, "end": v(32.12, 5.33) * mm});
            skLineSegment(sketch, "E792", {"start": v(32.12, 5.33) * mm, "end": v(32, 5.38) * mm});
            skLineSegment(sketch, "E793", {"start": v(32, 5.38) * mm, "end": v(31.88, 5.43) * mm});
            skLineSegment(sketch, "E794", {"start": v(31.88, 5.43) * mm, "end": v(31.76, 5.46) * mm});
            skLineSegment(sketch, "E795", {"start": v(31.76, 5.46) * mm, "end": v(31.5, 5.52) * mm});
            skLineSegment(sketch, "E796", {"start": v(31.5, 5.52) * mm, "end": v(31.27, 5.61) * mm});
            skLineSegment(sketch, "E797", {"start": v(31.27, 5.61) * mm, "end": v(31.03, 5.72) * mm});
            skLineSegment(sketch, "E798", {"start": v(31.03, 5.72) * mm, "end": v(30.8, 5.85) * mm});
            skLineSegment(sketch, "E799", {"start": v(30.8, 5.85) * mm, "end": v(30.56, 6) * mm});
            skLineSegment(sketch, "E800", {"start": v(30.56, 6) * mm, "end": v(30.34, 6.15) * mm});
            skLineSegment(sketch, "E801", {"start": v(30.34, 6.15) * mm, "end": v(30.11, 6.32) * mm});
            skLineSegment(sketch, "E802", {"start": v(30.11, 6.32) * mm, "end": v(29.9, 6.5) * mm});
            skLineSegment(sketch, "E803", {"start": v(29.9, 6.5) * mm, "end": v(29.68, 6.7) * mm});
            skLineSegment(sketch, "E804", {"start": v(29.68, 6.7) * mm, "end": v(29.46, 6.9) * mm});
            skLineSegment(sketch, "E805", {"start": v(29.46, 6.9) * mm, "end": v(29.25, 7.11) * mm});
            skLineSegment(sketch, "E806", {"start": v(29.25, 7.11) * mm, "end": v(29.1, 7.28) * mm});
            skLineSegment(sketch, "E807", {"start": v(29.1, 7.28) * mm, "end": v(29.86, 9.52) * mm});
            skLineSegment(sketch, "E808", {"start": v(29.86, 9.52) * mm, "end": v(30.08, 9.56) * mm});
            skLineSegment(sketch, "E809", {"start": v(30.08, 9.56) * mm, "end": v(30.37, 9.6) * mm});
            skLineSegment(sketch, "E810", {"start": v(30.37, 9.6) * mm, "end": v(30.67, 9.64) * mm});
            skLineSegment(sketch, "E811", {"start": v(30.67, 9.64) * mm, "end": v(30.96, 9.66) * mm});
            skLineSegment(sketch, "E812", {"start": v(30.96, 9.66) * mm, "end": v(31.24, 9.67) * mm});
            skLineSegment(sketch, "E813", {"start": v(31.24, 9.67) * mm, "end": v(31.52, 9.67) * mm});
            skLineSegment(sketch, "E814", {"start": v(31.52, 9.67) * mm, "end": v(31.8, 9.66) * mm});
            skLineSegment(sketch, "E815", {"start": v(31.8, 9.66) * mm, "end": v(32.07, 9.63) * mm});
            skLineSegment(sketch, "E816", {"start": v(32.07, 9.63) * mm, "end": v(32.33, 9.6) * mm});
            skLineSegment(sketch, "E817", {"start": v(32.33, 9.6) * mm, "end": v(32.59, 9.54) * mm});
            skLineSegment(sketch, "E818", {"start": v(32.59, 9.54) * mm, "end": v(32.83, 9.46) * mm});
            skLineSegment(sketch, "E819", {"start": v(32.83, 9.46) * mm, "end": v(33.07, 9.36) * mm});
            skLineSegment(sketch, "E820", {"start": v(33.07, 9.36) * mm, "end": v(33.19, 9.31) * mm});
            skLineSegment(sketch, "E821", {"start": v(33.19, 9.31) * mm, "end": v(33.31, 9.28) * mm});
            skLineSegment(sketch, "E822", {"start": v(33.31, 9.28) * mm, "end": v(33.44, 9.25) * mm});
            skLineSegment(sketch, "E823", {"start": v(33.44, 9.25) * mm, "end": v(33.57, 9.23) * mm});
            skLineSegment(sketch, "E824", {"start": v(33.57, 9.23) * mm, "end": v(33.64, 9.23) * mm});
            skLineSegment(sketch, "E825", {"start": v(33.64, 9.23) * mm, "end": v(33.72, 9.24) * mm});
            skLineSegment(sketch, "E826", {"start": v(33.72, 9.24) * mm, "end": v(33.8, 9.25) * mm});
            skLineSegment(sketch, "E827", {"start": v(33.8, 9.25) * mm, "end": v(33.89, 9.28) * mm});
            skLineSegment(sketch, "E828", {"start": v(33.89, 9.28) * mm, "end": v(34.03, 9.4) * mm});
            skLineSegment(sketch, "E829", {"start": v(34.03, 9.4) * mm, "end": v(34.58, 10.3) * mm});
            skLineSegment(sketch, "E830", {"start": v(34.58, 10.3) * mm, "end": v(35.2, 11.16) * mm});
            skLineSegment(sketch, "E831", {"start": v(35.2, 11.16) * mm, "end": v(35.26, 11.34) * mm});
            skLineSegment(sketch, "E832", {"start": v(35.26, 11.34) * mm, "end": v(35.25, 11.43) * mm});
            skLineSegment(sketch, "E833", {"start": v(35.25, 11.43) * mm, "end": v(35.23, 11.51) * mm});
            skLineSegment(sketch, "E834", {"start": v(35.23, 11.51) * mm, "end": v(35.2, 11.58) * mm});
            skLineSegment(sketch, "E835", {"start": v(35.2, 11.58) * mm, "end": v(35.18, 11.65) * mm});
            skLineSegment(sketch, "E836", {"start": v(35.18, 11.65) * mm, "end": v(35.11, 11.77) * mm});
            skLineSegment(sketch, "E837", {"start": v(35.11, 11.77) * mm, "end": v(35.04, 11.87) * mm});
            skLineSegment(sketch, "E838", {"start": v(35.04, 11.87) * mm, "end": v(34.95, 11.97) * mm});
            skLineSegment(sketch, "E839", {"start": v(34.95, 11.97) * mm, "end": v(34.86, 12.06) * mm});
            skLineSegment(sketch, "E840", {"start": v(34.86, 12.06) * mm, "end": v(34.68, 12.24) * mm});
            skLineSegment(sketch, "E841", {"start": v(34.68, 12.24) * mm, "end": v(34.51, 12.44) * mm});
            skLineSegment(sketch, "E842", {"start": v(34.51, 12.44) * mm, "end": v(34.36, 12.65) * mm});
            skLineSegment(sketch, "E843", {"start": v(34.36, 12.65) * mm, "end": v(34.23, 12.88) * mm});
            skLineSegment(sketch, "E844", {"start": v(34.23, 12.88) * mm, "end": v(34.1, 13.12) * mm});
            skLineSegment(sketch, "E845", {"start": v(34.1, 13.12) * mm, "end": v(33.98, 13.37) * mm});
            skLineSegment(sketch, "E846", {"start": v(33.98, 13.37) * mm, "end": v(33.87, 13.63) * mm});
            skLineSegment(sketch, "E847", {"start": v(33.87, 13.63) * mm, "end": v(33.77, 13.9) * mm});
            skLineSegment(sketch, "E848", {"start": v(33.77, 13.9) * mm, "end": v(33.68, 14.17) * mm});
            skLineSegment(sketch, "E849", {"start": v(33.68, 14.17) * mm, "end": v(33.6, 14.45) * mm});
            skLineSegment(sketch, "E850", {"start": v(33.6, 14.45) * mm, "end": v(33.52, 14.74) * mm});
            skLineSegment(sketch, "E851", {"start": v(33.52, 14.74) * mm, "end": v(33.47, 14.96) * mm});
            skLineSegment(sketch, "E852", {"start": v(33.47, 14.96) * mm, "end": v(35.25, 16.53) * mm});
            skLineSegment(sketch, "E853", {"start": v(35.25, 16.53) * mm, "end": v(35.46, 16.45) * mm});
            skLineSegment(sketch, "E854", {"start": v(35.46, 16.45) * mm, "end": v(35.74, 16.34) * mm});
            skLineSegment(sketch, "E855", {"start": v(35.74, 16.34) * mm, "end": v(36, 16.23) * mm});
            skLineSegment(sketch, "E856", {"start": v(36, 16.23) * mm, "end": v(36.27, 16.1) * mm});
            skLineSegment(sketch, "E857", {"start": v(36.27, 16.1) * mm, "end": v(36.52, 15.97) * mm});
            skLineSegment(sketch, "E858", {"start": v(36.52, 15.97) * mm, "end": v(36.76, 15.83) * mm});
            skLineSegment(sketch, "E859", {"start": v(36.76, 15.83) * mm, "end": v(37, 15.68) * mm});
            skLineSegment(sketch, "E860", {"start": v(37, 15.68) * mm, "end": v(37.22, 15.52) * mm});
            skLineSegment(sketch, "E861", {"start": v(37.22, 15.52) * mm, "end": v(37.43, 15.35) * mm});
            skLineSegment(sketch, "E862", {"start": v(37.43, 15.35) * mm, "end": v(37.62, 15.18) * mm});
            skLineSegment(sketch, "E863", {"start": v(37.62, 15.18) * mm, "end": v(37.8, 14.99) * mm});
            skLineSegment(sketch, "E864", {"start": v(37.8, 14.99) * mm, "end": v(37.95, 14.78) * mm});
            skLineSegment(sketch, "E865", {"start": v(37.95, 14.78) * mm, "end": v(38.03, 14.68) * mm});
            skLineSegment(sketch, "E866", {"start": v(38.03, 14.68) * mm, "end": v(38.12, 14.6) * mm});
            skLineSegment(sketch, "E867", {"start": v(38.12, 14.6) * mm, "end": v(38.22, 14.5) * mm});
            skLineSegment(sketch, "E868", {"start": v(38.22, 14.5) * mm, "end": v(38.32, 14.42) * mm});
            skLineSegment(sketch, "E869", {"start": v(38.32, 14.42) * mm, "end": v(38.38, 14.38) * mm});
            skLineSegment(sketch, "E870", {"start": v(38.38, 14.38) * mm, "end": v(38.45, 14.35) * mm});
            skLineSegment(sketch, "E871", {"start": v(38.45, 14.35) * mm, "end": v(38.53, 14.32) * mm});
            skLineSegment(sketch, "E872", {"start": v(38.53, 14.32) * mm, "end": v(38.62, 14.3) * mm});
            skLineSegment(sketch, "E873", {"start": v(38.62, 14.3) * mm, "end": v(38.8, 14.34) * mm});
            skLineSegment(sketch, "E874", {"start": v(38.8, 14.34) * mm, "end": v(39.73, 14.85) * mm});
            skLineSegment(sketch, "E875", {"start": v(39.73, 14.85) * mm, "end": v(40.7, 15.28) * mm});
            skLineSegment(sketch, "E876", {"start": v(40.7, 15.28) * mm, "end": v(40.83, 15.4) * mm});
            skLineSegment(sketch, "E877", {"start": v(40.83, 15.4) * mm, "end": v(40.88, 15.49) * mm});
            skLineSegment(sketch, "E878", {"start": v(40.88, 15.49) * mm, "end": v(40.9, 15.57) * mm});
            skLineSegment(sketch, "E879", {"start": v(40.9, 15.57) * mm, "end": v(40.91, 15.64) * mm});
            skLineSegment(sketch, "E880", {"start": v(40.91, 15.64) * mm, "end": v(40.92, 15.7) * mm});
            skLineSegment(sketch, "E881", {"start": v(40.92, 15.7) * mm, "end": v(40.92, 15.85) * mm});
            skLineSegment(sketch, "E882", {"start": v(40.92, 15.85) * mm, "end": v(40.9, 15.98) * mm});
            skLineSegment(sketch, "E883", {"start": v(40.9, 15.98) * mm, "end": v(40.89, 16.1) * mm});
            skLineSegment(sketch, "E884", {"start": v(40.89, 16.1) * mm, "end": v(40.86, 16.23) * mm});
            skLineSegment(sketch, "E885", {"start": v(40.86, 16.23) * mm, "end": v(40.79, 16.47) * mm});
            skLineSegment(sketch, "E886", {"start": v(40.79, 16.47) * mm, "end": v(40.74, 16.73) * mm});
            skLineSegment(sketch, "E887", {"start": v(40.74, 16.73) * mm, "end": v(40.72, 16.99) * mm});
            skLineSegment(sketch, "E888", {"start": v(40.72, 16.99) * mm, "end": v(40.71, 17.25) * mm});
            skLineSegment(sketch, "E889", {"start": v(40.71, 17.25) * mm, "end": v(40.72, 17.53) * mm});
            skLineSegment(sketch, "E890", {"start": v(40.72, 17.53) * mm, "end": v(40.74, 17.8) * mm});
            skLineSegment(sketch, "E891", {"start": v(40.74, 17.8) * mm, "end": v(40.78, 18.08) * mm});
            skLineSegment(sketch, "E892", {"start": v(40.78, 18.08) * mm, "end": v(40.82, 18.36) * mm});
            skLineSegment(sketch, "E893", {"start": v(40.82, 18.36) * mm, "end": v(40.88, 18.64) * mm});
            skLineSegment(sketch, "E894", {"start": v(40.88, 18.64) * mm, "end": v(40.95, 18.93) * mm});
            skLineSegment(sketch, "E895", {"start": v(40.95, 18.93) * mm, "end": v(41.03, 19.22) * mm});
            skLineSegment(sketch, "E896", {"start": v(41.03, 19.22) * mm, "end": v(41.1, 19.44) * mm});
            skLineSegment(sketch, "E897", {"start": v(41.1, 19.44) * mm, "end": v(43.42, 19.9) * mm});
            skLineSegment(sketch, "E898", {"start": v(43.42, 19.9) * mm, "end": v(43.57, 19.73) * mm});
            skLineSegment(sketch, "E899", {"start": v(43.57, 19.73) * mm, "end": v(43.75, 19.5) * mm});
            skLineSegment(sketch, "E900", {"start": v(43.75, 19.5) * mm, "end": v(43.93, 19.26) * mm});
            skLineSegment(sketch, "E901", {"start": v(43.93, 19.26) * mm, "end": v(44.1, 19.02) * mm});
            skLineSegment(sketch, "E902", {"start": v(44.1, 19.02) * mm, "end": v(44.24, 18.78) * mm});
            skLineSegment(sketch, "E903", {"start": v(44.24, 18.78) * mm, "end": v(44.38, 18.54) * mm});
            skLineSegment(sketch, "E904", {"start": v(44.38, 18.54) * mm, "end": v(44.51, 18.29) * mm});
            skLineSegment(sketch, "E905", {"start": v(44.51, 18.29) * mm, "end": v(44.62, 18.04) * mm});
            skLineSegment(sketch, "E906", {"start": v(44.62, 18.04) * mm, "end": v(44.72, 17.8) * mm});
            skLineSegment(sketch, "E907", {"start": v(44.72, 17.8) * mm, "end": v(44.8, 17.54) * mm});
            skLineSegment(sketch, "E908", {"start": v(44.8, 17.54) * mm, "end": v(44.86, 17.3) * mm});
            skLineSegment(sketch, "E909", {"start": v(44.86, 17.3) * mm, "end": v(44.89, 17.04) * mm});
            skLineSegment(sketch, "E910", {"start": v(44.89, 17.04) * mm, "end": v(44.9, 16.91) * mm});
            skLineSegment(sketch, "E911", {"start": v(44.9, 16.91) * mm, "end": v(44.94, 16.79) * mm});
            skLineSegment(sketch, "E912", {"start": v(44.94, 16.79) * mm, "end": v(44.98, 16.66) * mm});
            skLineSegment(sketch, "E913", {"start": v(44.98, 16.66) * mm, "end": v(45.03, 16.54) * mm});
            skLineSegment(sketch, "E914", {"start": v(45.03, 16.54) * mm, "end": v(45.07, 16.48) * mm});
            skLineSegment(sketch, "E915", {"start": v(45.07, 16.48) * mm, "end": v(45.1, 16.41) * mm});
            skLineSegment(sketch, "E916", {"start": v(45.1, 16.41) * mm, "end": v(45.16, 16.35) * mm});
            skLineSegment(sketch, "E917", {"start": v(45.16, 16.35) * mm, "end": v(45.23, 16.3) * mm});
            skLineSegment(sketch, "E918", {"start": v(45.23, 16.3) * mm, "end": v(45.4, 16.23) * mm});
            skLineSegment(sketch, "E919", {"start": v(45.4, 16.23) * mm, "end": v(46.46, 16.2) * mm});
            skLineSegment(sketch, "E920", {"start": v(46.46, 16.2) * mm, "end": v(47.51, 16.1) * mm});
            skLineSegment(sketch, "E921", {"start": v(47.51, 16.1) * mm, "end": v(47.7, 16.14) * mm});
            skLineSegment(sketch, "E922", {"start": v(47.7, 16.14) * mm, "end": v(47.78, 16.19) * mm});
            skLineSegment(sketch, "E923", {"start": v(47.78, 16.19) * mm, "end": v(47.83, 16.24) * mm});
            skLineSegment(sketch, "E924", {"start": v(47.83, 16.24) * mm, "end": v(47.88, 16.3) * mm});
            skLineSegment(sketch, "E925", {"start": v(47.88, 16.3) * mm, "end": v(47.92, 16.36) * mm});
            skLineSegment(sketch, "E926", {"start": v(47.92, 16.36) * mm, "end": v(48, 16.47) * mm});
            skLineSegment(sketch, "E927", {"start": v(48, 16.47) * mm, "end": v(48.05, 16.6) * mm});
            skLineSegment(sketch, "E928", {"start": v(48.05, 16.6) * mm, "end": v(48.1, 16.71) * mm});
            skLineSegment(sketch, "E929", {"start": v(48.1, 16.71) * mm, "end": v(48.13, 16.84) * mm});
            skLineSegment(sketch, "E930", {"start": v(48.13, 16.84) * mm, "end": v(48.19, 17.08) * mm});
            skLineSegment(sketch, "E931", {"start": v(48.19, 17.08) * mm, "end": v(48.28, 17.33) * mm});
            skLineSegment(sketch, "E932", {"start": v(48.28, 17.33) * mm, "end": v(48.39, 17.56) * mm});
            skLineSegment(sketch, "E933", {"start": v(48.39, 17.56) * mm, "end": v(48.52, 17.8) * mm});
            skLineSegment(sketch, "E934", {"start": v(48.52, 17.8) * mm, "end": v(48.66, 18.03) * mm});
            skLineSegment(sketch, "E935", {"start": v(48.66, 18.03) * mm, "end": v(48.82, 18.26) * mm});
            skLineSegment(sketch, "E936", {"start": v(48.82, 18.26) * mm, "end": v(48.99, 18.48) * mm});
            skLineSegment(sketch, "E937", {"start": v(48.99, 18.48) * mm, "end": v(49.17, 18.7) * mm});
            skLineSegment(sketch, "E938", {"start": v(49.17, 18.7) * mm, "end": v(49.36, 18.92) * mm});
            skLineSegment(sketch, "E939", {"start": v(49.36, 18.92) * mm, "end": v(49.56, 19.13) * mm});
            skLineSegment(sketch, "E940", {"start": v(49.56, 19.13) * mm, "end": v(49.78, 19.34) * mm});
            skLineSegment(sketch, "E941", {"start": v(49.78, 19.34) * mm, "end": v(49.94, 19.5) * mm});
            skLineSegment(sketch, "E942", {"start": v(49.94, 19.5) * mm, "end": v(52.19, 18.74) * mm});
            skLineSegment(sketch, "E943", {"start": v(52.19, 18.74) * mm, "end": v(52.23, 18.51) * mm});
            skLineSegment(sketch, "E944", {"start": v(52.23, 18.51) * mm, "end": v(52.27, 18.22) * mm});
            skLineSegment(sketch, "E945", {"start": v(52.27, 18.22) * mm, "end": v(52.3, 17.93) * mm});
            skLineSegment(sketch, "E946", {"start": v(52.3, 17.93) * mm, "end": v(52.33, 17.64) * mm});
            skLineSegment(sketch, "E947", {"start": v(52.33, 17.64) * mm, "end": v(52.34, 17.35) * mm});
            skLineSegment(sketch, "E948", {"start": v(52.34, 17.35) * mm, "end": v(52.34, 17.07) * mm});
            skLineSegment(sketch, "E949", {"start": v(52.34, 17.07) * mm, "end": v(52.32, 16.8) * mm});
            skLineSegment(sketch, "E950", {"start": v(52.32, 16.8) * mm, "end": v(52.3, 16.53) * mm});
            skLineSegment(sketch, "E951", {"start": v(52.3, 16.53) * mm, "end": v(52.26, 16.26) * mm});
            skLineSegment(sketch, "E952", {"start": v(52.26, 16.26) * mm, "end": v(52.2, 16) * mm});
            skLineSegment(sketch, "E953", {"start": v(52.2, 16) * mm, "end": v(52.13, 15.76) * mm});
            skLineSegment(sketch, "E954", {"start": v(52.13, 15.76) * mm, "end": v(52.03, 15.52) * mm});
            skLineSegment(sketch, "E955", {"start": v(52.03, 15.52) * mm, "end": v(51.98, 15.4) * mm});
            skLineSegment(sketch, "E956", {"start": v(51.98, 15.4) * mm, "end": v(51.94, 15.28) * mm});
            skLineSegment(sketch, "E957", {"start": v(51.94, 15.28) * mm, "end": v(51.91, 15.15) * mm});
            skLineSegment(sketch, "E958", {"start": v(51.91, 15.15) * mm, "end": v(51.9, 15.02) * mm});
            skLineSegment(sketch, "E959", {"start": v(51.9, 15.02) * mm, "end": v(51.9, 14.95) * mm});
            skLineSegment(sketch, "E960", {"start": v(51.9, 14.95) * mm, "end": v(51.9, 14.87) * mm});
            skLineSegment(sketch, "E961", {"start": v(51.9, 14.87) * mm, "end": v(51.92, 14.8) * mm});
            skLineSegment(sketch, "E962", {"start": v(51.92, 14.8) * mm, "end": v(51.95, 14.7) * mm});
            skLineSegment(sketch, "E963", {"start": v(51.95, 14.7) * mm, "end": v(52.07, 14.56) * mm});
            skLineSegment(sketch, "E964", {"start": v(52.07, 14.56) * mm, "end": v(52.97, 14.02) * mm});
            skLineSegment(sketch, "E965", {"start": v(52.97, 14.02) * mm, "end": v(53.83, 13.4) * mm});
            skLineSegment(sketch, "E966", {"start": v(53.83, 13.4) * mm, "end": v(54, 13.34) * mm});
            skLineSegment(sketch, "E967", {"start": v(54, 13.34) * mm, "end": v(54.1, 13.34) * mm});
            skLineSegment(sketch, "E968", {"start": v(54.1, 13.34) * mm, "end": v(54.18, 13.36) * mm});
            skLineSegment(sketch, "E969", {"start": v(54.18, 13.36) * mm, "end": v(54.25, 13.39) * mm});
            skLineSegment(sketch, "E970", {"start": v(54.25, 13.39) * mm, "end": v(54.31, 13.41) * mm});
            skLineSegment(sketch, "E971", {"start": v(54.31, 13.41) * mm, "end": v(54.43, 13.48) * mm});
            skLineSegment(sketch, "E972", {"start": v(54.43, 13.48) * mm, "end": v(54.54, 13.56) * mm});
            skLineSegment(sketch, "E973", {"start": v(54.54, 13.56) * mm, "end": v(54.64, 13.64) * mm});
            skLineSegment(sketch, "E974", {"start": v(54.64, 13.64) * mm, "end": v(54.73, 13.73) * mm});
            skLineSegment(sketch, "E975", {"start": v(54.73, 13.73) * mm, "end": v(54.9, 13.91) * mm});
            skLineSegment(sketch, "E976", {"start": v(54.9, 13.91) * mm, "end": v(55.1, 14.08) * mm});
            skLineSegment(sketch, "E977", {"start": v(55.1, 14.08) * mm, "end": v(55.32, 14.23) * mm});
            skLineSegment(sketch, "E978", {"start": v(55.32, 14.23) * mm, "end": v(55.55, 14.37) * mm});
            skLineSegment(sketch, "E979", {"start": v(55.55, 14.37) * mm, "end": v(55.79, 14.5) * mm});
            skLineSegment(sketch, "E980", {"start": v(55.79, 14.5) * mm, "end": v(56.04, 14.61) * mm});
            skLineSegment(sketch, "E981", {"start": v(56.04, 14.61) * mm, "end": v(56.3, 14.72) * mm});
            skLineSegment(sketch, "E982", {"start": v(56.3, 14.72) * mm, "end": v(56.56, 14.82) * mm});
            skLineSegment(sketch, "E983", {"start": v(56.56, 14.82) * mm, "end": v(56.84, 14.91) * mm});
            skLineSegment(sketch, "E984", {"start": v(56.84, 14.91) * mm, "end": v(57.12, 15) * mm});
            skLineSegment(sketch, "E985", {"start": v(57.12, 15) * mm, "end": v(57.4, 15.07) * mm});
            skLineSegment(sketch, "E986", {"start": v(57.4, 15.07) * mm, "end": v(57.63, 15.12) * mm});
            skLineSegment(sketch, "E987", {"start": v(57.63, 15.12) * mm, "end": v(59.2, 13.35) * mm});
            skLineSegment(sketch, "E988", {"start": v(59.2, 13.35) * mm, "end": v(59.12, 13.13) * mm});
            skLineSegment(sketch, "E989", {"start": v(59.12, 13.13) * mm, "end": v(59, 12.85) * mm});
            skLineSegment(sketch, "E990", {"start": v(59, 12.85) * mm, "end": v(58.9, 12.58) * mm});
            skLineSegment(sketch, "E991", {"start": v(58.9, 12.58) * mm, "end": v(58.77, 12.32) * mm});
            skLineSegment(sketch, "E992", {"start": v(58.77, 12.32) * mm, "end": v(58.63, 12.07) * mm});
            skLineSegment(sketch, "E993", {"start": v(58.63, 12.07) * mm, "end": v(58.5, 11.83) * mm});
            skLineSegment(sketch, "E994", {"start": v(58.5, 11.83) * mm, "end": v(58.34, 11.6) * mm});
            skLineSegment(sketch, "E995", {"start": v(58.34, 11.6) * mm, "end": v(58.19, 11.37) * mm});
            skLineSegment(sketch, "E996", {"start": v(58.19, 11.37) * mm, "end": v(58.02, 11.16) * mm});
            skLineSegment(sketch, "E997", {"start": v(58.02, 11.16) * mm, "end": v(57.84, 10.97) * mm});
            skLineSegment(sketch, "E998", {"start": v(57.84, 10.97) * mm, "end": v(57.66, 10.8) * mm});
            skLineSegment(sketch, "E999", {"start": v(57.66, 10.8) * mm, "end": v(57.45, 10.64) * mm});
            skLineSegment(sketch, "E1000", {"start": v(57.45, 10.64) * mm, "end": v(57.35, 10.56) * mm});
            skLineSegment(sketch, "E1001", {"start": v(57.35, 10.56) * mm, "end": v(57.26, 10.47) * mm});
            skLineSegment(sketch, "E1002", {"start": v(57.26, 10.47) * mm, "end": v(57.17, 10.38) * mm});
            skLineSegment(sketch, "E1003", {"start": v(57.17, 10.38) * mm, "end": v(57.09, 10.27) * mm});
            skLineSegment(sketch, "E1004", {"start": v(57.09, 10.27) * mm, "end": v(57.05, 10.2) * mm});
            skLineSegment(sketch, "E1005", {"start": v(57.05, 10.2) * mm, "end": v(57.02, 10.14) * mm});
            skLineSegment(sketch, "E1006", {"start": v(57.02, 10.14) * mm, "end": v(56.99, 10.07) * mm});
            skLineSegment(sketch, "E1007", {"start": v(56.99, 10.07) * mm, "end": v(56.97, 9.97) * mm});
            skLineSegment(sketch, "E1008", {"start": v(56.97, 9.97) * mm, "end": v(57.01, 9.79) * mm});
            skLineSegment(sketch, "E1009", {"start": v(57.01, 9.79) * mm, "end": v(57.52, 8.86) * mm});
            skLineSegment(sketch, "E1010", {"start": v(57.52, 8.86) * mm, "end": v(57.95, 7.9) * mm});
            skLineSegment(sketch, "E1011", {"start": v(57.95, 7.9) * mm, "end": v(58.07, 7.76) * mm});
            skLineSegment(sketch, "E1012", {"start": v(58.07, 7.76) * mm, "end": v(58.15, 7.72) * mm});
            skLineSegment(sketch, "E1013", {"start": v(58.15, 7.72) * mm, "end": v(58.23, 7.7) * mm});
            skLineSegment(sketch, "E1014", {"start": v(58.23, 7.7) * mm, "end": v(58.3, 7.68) * mm});
            skLineSegment(sketch, "E1015", {"start": v(58.3, 7.68) * mm, "end": v(58.38, 7.67) * mm});
            skLineSegment(sketch, "E1016", {"start": v(58.38, 7.67) * mm, "end": v(58.51, 7.67) * mm});
            skLineSegment(sketch, "E1017", {"start": v(58.51, 7.67) * mm, "end": v(58.64, 7.68) * mm});
            skLineSegment(sketch, "E1018", {"start": v(58.64, 7.68) * mm, "end": v(58.77, 7.7) * mm});
            skLineSegment(sketch, "E1019", {"start": v(58.77, 7.7) * mm, "end": v(58.9, 7.74) * mm});
            skLineSegment(sketch, "E1020", {"start": v(58.9, 7.74) * mm, "end": v(59.14, 7.8) * mm});
            skLineSegment(sketch, "E1021", {"start": v(59.14, 7.8) * mm, "end": v(59.4, 7.85) * mm});
            skLineSegment(sketch, "E1022", {"start": v(59.4, 7.85) * mm, "end": v(59.65, 7.87) * mm});
            skLineSegment(sketch, "E1023", {"start": v(59.65, 7.87) * mm, "end": v(59.92, 7.88) * mm});
            skLineSegment(sketch, "E1024", {"start": v(59.92, 7.88) * mm, "end": v(60.2, 7.87) * mm});
            skLineSegment(sketch, "E1025", {"start": v(60.2, 7.87) * mm, "end": v(60.47, 7.85) * mm});
            skLineSegment(sketch, "E1026", {"start": v(60.47, 7.85) * mm, "end": v(60.75, 7.81) * mm});
            skLineSegment(sketch, "E1027", {"start": v(60.75, 7.81) * mm, "end": v(61.03, 7.77) * mm});
            skLineSegment(sketch, "E1028", {"start": v(61.03, 7.77) * mm, "end": v(61.31, 7.71) * mm});
            skLineSegment(sketch, "E1029", {"start": v(61.31, 7.71) * mm, "end": v(61.6, 7.64) * mm});
            skLineSegment(sketch, "E1030", {"start": v(61.6, 7.64) * mm, "end": v(61.88, 7.56) * mm});
            skLineSegment(sketch, "E1031", {"start": v(61.88, 7.56) * mm, "end": v(62.1, 7.5) * mm});
            skLineSegment(sketch, "E1032", {"start": v(62.1, 7.5) * mm, "end": v(62.57, 5.17) * mm});
            skLineSegment(sketch, "E1033", {"start": v(62.57, 5.17) * mm, "end": v(62.4, 5.03) * mm});
            skLineSegment(sketch, "E1034", {"start": v(62.4, 5.03) * mm, "end": v(62.16, 4.84) * mm});
            skLineSegment(sketch, "E1035", {"start": v(62.16, 4.84) * mm, "end": v(61.93, 4.66) * mm});
            skLineSegment(sketch, "E1036", {"start": v(61.93, 4.66) * mm, "end": v(61.69, 4.5) * mm});
            skLineSegment(sketch, "E1037", {"start": v(61.69, 4.5) * mm, "end": v(61.44, 4.35) * mm});
            skLineSegment(sketch, "E1038", {"start": v(61.44, 4.35) * mm, "end": v(61.2, 4.2) * mm});
            skLineSegment(sketch, "E1039", {"start": v(61.2, 4.2) * mm, "end": v(60.96, 4.08) * mm});
            skLineSegment(sketch, "E1040", {"start": v(60.96, 4.08) * mm, "end": v(60.7, 3.97) * mm});
            skLineSegment(sketch, "E1041", {"start": v(60.7, 3.97) * mm, "end": v(60.46, 3.87) * mm});
            skLineSegment(sketch, "E1042", {"start": v(60.46, 3.87) * mm, "end": v(60.21, 3.8) * mm});
            skLineSegment(sketch, "E1043", {"start": v(60.21, 3.8) * mm, "end": v(59.96, 3.73) * mm});
            skLineSegment(sketch, "E1044", {"start": v(59.96, 3.73) * mm, "end": v(59.7, 3.7) * mm});
            skLineSegment(sketch, "E1045", {"start": v(59.7, 3.7) * mm, "end": v(59.58, 3.68) * mm});
            skLineSegment(sketch, "E1046", {"start": v(59.58, 3.68) * mm, "end": v(59.45, 3.65) * mm});
            skLineSegment(sketch, "E1047", {"start": v(59.45, 3.65) * mm, "end": v(59.33, 3.62) * mm});
            skLineSegment(sketch, "E1048", {"start": v(59.33, 3.62) * mm, "end": v(59.2, 3.56) * mm});
            skLineSegment(sketch, "E1049", {"start": v(59.2, 3.56) * mm, "end": v(59.14, 3.53) * mm});
            skLineSegment(sketch, "E1050", {"start": v(59.14, 3.53) * mm, "end": v(59.08, 3.49) * mm});
            skLineSegment(sketch, "E1051", {"start": v(59.08, 3.49) * mm, "end": v(59.02, 3.43) * mm});
            skLineSegment(sketch, "E1052", {"start": v(59.02, 3.43) * mm, "end": v(58.96, 3.36) * mm});
            skLineSegment(sketch, "E1053", {"start": v(58.96, 3.36) * mm, "end": v(58.9, 3.18) * mm});
            skLineSegment(sketch, "E1054", {"start": v(58.9, 3.18) * mm, "end": v(58.87, 2.13) * mm});
            skLineSegment(sketch, "E1055", {"start": v(58.87, 2.13) * mm, "end": v(58.77, 1.08) * mm});
            skLineSegment(sketch, "E1056", {"start": v(58.77, 1.08) * mm, "end": v(58.8, 0.9) * mm});
            skLineSegment(sketch, "E1057", {"start": v(58.8, 0.9) * mm, "end": v(58.85, 0.82) * mm});
            skLineSegment(sketch, "E1058", {"start": v(58.85, 0.82) * mm, "end": v(58.9, 0.76) * mm});
            skLineSegment(sketch, "E1059", {"start": v(58.9, 0.76) * mm, "end": v(58.96, 0.71) * mm});
            skLineSegment(sketch, "E1060", {"start": v(58.96, 0.71) * mm, "end": v(59.02, 0.67) * mm});
            skLineSegment(sketch, "E1061", {"start": v(59.02, 0.67) * mm, "end": v(59.14, 0.6) * mm});
            skLineSegment(sketch, "E1062", {"start": v(59.14, 0.6) * mm, "end": v(59.26, 0.55) * mm});
            skLineSegment(sketch, "E1063", {"start": v(59.26, 0.55) * mm, "end": v(59.38, 0.5) * mm});
            skLineSegment(sketch, "E1064", {"start": v(59.38, 0.5) * mm, "end": v(59.5, 0.46) * mm});
            skLineSegment(sketch, "E1065", {"start": v(59.5, 0.46) * mm, "end": v(59.75, 0.4) * mm});
            skLineSegment(sketch, "E1066", {"start": v(59.75, 0.4) * mm, "end": v(60, 0.32) * mm});
            skLineSegment(sketch, "E1067", {"start": v(60, 0.32) * mm, "end": v(60.23, 0.2) * mm});
            skLineSegment(sketch, "E1068", {"start": v(60.23, 0.2) * mm, "end": v(60.46, 0.08) * mm});
            skLineSegment(sketch, "E1069", {"start": v(60.46, 0.08) * mm, "end": v(60.7, -0.07) * mm});
            skLineSegment(sketch, "E1070", {"start": v(60.7, -0.07) * mm, "end": v(60.92, -0.22) * mm});
            skLineSegment(sketch, "E1071", {"start": v(60.92, -0.22) * mm, "end": v(61.15, -0.4) * mm});
            skLineSegment(sketch, "E1072", {"start": v(61.15, -0.4) * mm, "end": v(61.37, -0.57) * mm});
            skLineSegment(sketch, "E1073", {"start": v(61.37, -0.57) * mm, "end": v(61.58, -0.77) * mm});
            skLineSegment(sketch, "E1074", {"start": v(61.58, -0.77) * mm, "end": v(61.8, -0.97) * mm});
            skLineSegment(sketch, "E1075", {"start": v(61.8, -0.97) * mm, "end": v(62, -1.18) * mm});
            skLineSegment(sketch, "E1076", {"start": v(62, -1.18) * mm, "end": v(62.16, -1.35) * mm});
            skLineSegment(sketch, "E1077", {"start": v(62.16, -1.35) * mm, "end": v(61.4, -3.6) * mm});
            skLineSegment(sketch, "E1078", {"start": v(61.4, -3.6) * mm, "end": v(61.18, -3.63) * mm});
            skLineSegment(sketch, "E1079", {"start": v(61.18, -3.63) * mm, "end": v(60.88, -3.68) * mm});
            skLineSegment(sketch, "E1080", {"start": v(60.88, -3.68) * mm, "end": v(60.6, -3.71) * mm});
            skLineSegment(sketch, "E1081", {"start": v(60.6, -3.71) * mm, "end": v(60.3, -3.73) * mm});
            skLineSegment(sketch, "E1082", {"start": v(60.3, -3.73) * mm, "end": v(60.02, -3.74) * mm});
            skLineSegment(sketch, "E1083", {"start": v(60.02, -3.74) * mm, "end": v(59.74, -3.74) * mm});
            skLineSegment(sketch, "E1084", {"start": v(59.74, -3.74) * mm, "end": v(59.46, -3.73) * mm});
            skLineSegment(sketch, "E1085", {"start": v(59.46, -3.73) * mm, "end": v(59.2, -3.7) * mm});
            skLineSegment(sketch, "E1086", {"start": v(59.2, -3.7) * mm, "end": v(58.93, -3.67) * mm});
            skLineSegment(sketch, "E1087", {"start": v(58.93, -3.67) * mm, "end": v(58.67, -3.61) * mm});
            skLineSegment(sketch, "E1088", {"start": v(58.67, -3.61) * mm, "end": v(58.42, -3.54) * mm});
            skLineSegment(sketch, "E1089", {"start": v(58.42, -3.54) * mm, "end": v(58.2, -3.43) * mm});
            skLineSegment(sketch, "E1090", {"start": v(58.2, -3.43) * mm, "end": v(58.07, -3.39) * mm});
            skLineSegment(sketch, "E1091", {"start": v(58.07, -3.39) * mm, "end": v(57.95, -3.35) * mm});
            skLineSegment(sketch, "E1092", {"start": v(57.95, -3.35) * mm, "end": v(57.82, -3.32) * mm});
            skLineSegment(sketch, "E1093", {"start": v(57.82, -3.32) * mm, "end": v(57.68, -3.3) * mm});
            skLineSegment(sketch, "E1094", {"start": v(57.68, -3.3) * mm, "end": v(57.61, -3.3) * mm});
            skLineSegment(sketch, "E1095", {"start": v(57.61, -3.3) * mm, "end": v(57.54, -3.3) * mm});
            skLineSegment(sketch, "E1096", {"start": v(57.54, -3.3) * mm, "end": v(57.46, -3.32) * mm});
            skLineSegment(sketch, "E1097", {"start": v(57.46, -3.32) * mm, "end": v(57.37, -3.35) * mm});
            skLineSegment(sketch, "E1098", {"start": v(57.37, -3.35) * mm, "end": v(57.23, -3.48) * mm});
            skLineSegment(sketch, "E1099", {"start": v(57.23, -3.48) * mm, "end": v(56.68, -4.38) * mm});
            skLineSegment(sketch, "E1100", {"start": v(56.68, -4.38) * mm, "end": v(56.07, -5.23) * mm});
            skLineSegment(sketch, "E1101", {"start": v(56.07, -5.23) * mm, "end": v(56, -5.41) * mm});
            skLineSegment(sketch, "E1102", {"start": v(56, -5.41) * mm, "end": v(56, -5.5) * mm});
            skLineSegment(sketch, "E1103", {"start": v(56, -5.5) * mm, "end": v(56.03, -5.59) * mm});
            skLineSegment(sketch, "E1104", {"start": v(56.03, -5.59) * mm, "end": v(56.05, -5.66) * mm});
            skLineSegment(sketch, "E1105", {"start": v(56.05, -5.66) * mm, "end": v(56.08, -5.72) * mm});
            skLineSegment(sketch, "E1106", {"start": v(56.08, -5.72) * mm, "end": v(56.15, -5.84) * mm});
            skLineSegment(sketch, "E1107", {"start": v(56.15, -5.84) * mm, "end": v(56.22, -5.95) * mm});
            skLineSegment(sketch, "E1108", {"start": v(56.22, -5.95) * mm, "end": v(56.3, -6.05) * mm});
            skLineSegment(sketch, "E1109", {"start": v(56.3, -6.05) * mm, "end": v(56.4, -6.14) * mm});
            skLineSegment(sketch, "E1110", {"start": v(56.4, -6.14) * mm, "end": v(56.58, -6.31) * mm});
            skLineSegment(sketch, "E1111", {"start": v(56.58, -6.31) * mm, "end": v(56.74, -6.51) * mm});
            skLineSegment(sketch, "E1112", {"start": v(56.74, -6.51) * mm, "end": v(56.9, -6.73) * mm});
            skLineSegment(sketch, "E1113", {"start": v(56.9, -6.73) * mm, "end": v(57.03, -6.95) * mm});
            skLineSegment(sketch, "E1114", {"start": v(57.03, -6.95) * mm, "end": v(57.16, -7.2) * mm});
            skLineSegment(sketch, "E1115", {"start": v(57.16, -7.2) * mm, "end": v(57.28, -7.44) * mm});
            skLineSegment(sketch, "E1116", {"start": v(57.28, -7.44) * mm, "end": v(57.39, -7.7) * mm});
            skLineSegment(sketch, "E1117", {"start": v(57.39, -7.7) * mm, "end": v(57.49, -7.97) * mm});
            skLineSegment(sketch, "E1118", {"start": v(57.49, -7.97) * mm, "end": v(57.58, -8.24) * mm});
            skLineSegment(sketch, "E1119", {"start": v(57.58, -8.24) * mm, "end": v(57.66, -8.53) * mm});
            skLineSegment(sketch, "E1120", {"start": v(57.66, -8.53) * mm, "end": v(57.74, -8.82) * mm});
            skLineSegment(sketch, "E1121", {"start": v(57.74, -8.82) * mm, "end": v(57.79, -9.04) * mm});
            skLineSegment(sketch, "E1122", {"start": v(57.79, -9.04) * mm, "end": v(56.01, -10.6) * mm});
            skLineSegment(sketch, "E1123", {"start": v(56.01, -10.6) * mm, "end": v(55.8, -10.53) * mm});
            skLineSegment(sketch, "E1124", {"start": v(55.8, -10.53) * mm, "end": v(55.52, -10.42) * mm});
            skLineSegment(sketch, "E1125", {"start": v(55.52, -10.42) * mm, "end": v(55.25, -10.3) * mm});
            skLineSegment(sketch, "E1126", {"start": v(55.25, -10.3) * mm, "end": v(54.99, -10.17) * mm});
            skLineSegment(sketch, "E1127", {"start": v(54.99, -10.17) * mm, "end": v(54.74, -10.04) * mm});
            skLineSegment(sketch, "E1128", {"start": v(54.74, -10.04) * mm, "end": v(54.5, -9.9) * mm});
            skLineSegment(sketch, "E1129", {"start": v(54.5, -9.9) * mm, "end": v(54.26, -9.75) * mm});
            skLineSegment(sketch, "E1130", {"start": v(54.26, -9.75) * mm, "end": v(54.04, -9.6) * mm});
            skLineSegment(sketch, "E1131", {"start": v(54.04, -9.6) * mm, "end": v(53.83, -9.43) * mm});
            skLineSegment(sketch, "E1132", {"start": v(53.83, -9.43) * mm, "end": v(53.64, -9.25) * mm});
            skLineSegment(sketch, "E1133", {"start": v(53.64, -9.25) * mm, "end": v(53.46, -9.06) * mm});
            skLineSegment(sketch, "E1134", {"start": v(53.46, -9.06) * mm, "end": v(53.3, -8.86) * mm});
            skLineSegment(sketch, "E1135", {"start": v(53.3, -8.86) * mm, "end": v(53.23, -8.76) * mm});
            skLineSegment(sketch, "E1136", {"start": v(53.23, -8.76) * mm, "end": v(53.14, -8.66) * mm});
            skLineSegment(sketch, "E1137", {"start": v(53.14, -8.66) * mm, "end": v(53.04, -8.58) * mm});
            skLineSegment(sketch, "E1138", {"start": v(53.04, -8.58) * mm, "end": v(52.94, -8.5) * mm});
            skLineSegment(sketch, "E1139", {"start": v(52.94, -8.5) * mm, "end": v(52.87, -8.46) * mm});
            skLineSegment(sketch, "E1140", {"start": v(52.87, -8.46) * mm, "end": v(52.8, -8.42) * mm});
            skLineSegment(sketch, "E1141", {"start": v(52.8, -8.42) * mm, "end": v(52.73, -8.4) * mm});
            skLineSegment(sketch, "E1142", {"start": v(52.73, -8.4) * mm, "end": v(52.64, -8.38) * mm});
            skLineSegment(sketch, "E1143", {"start": v(52.64, -8.38) * mm, "end": v(52.45, -8.42) * mm});
            skLineSegment(sketch, "E1144", {"start": v(52.45, -8.42) * mm, "end": v(51.53, -8.92) * mm});
            skLineSegment(sketch, "E1145", {"start": v(51.53, -8.92) * mm, "end": v(50.57, -9.35) * mm});
            skLineSegment(sketch, "E1146", {"start": v(50.57, -9.35) * mm, "end": v(50.43, -9.48) * mm});
            skLineSegment(sketch, "E1147", {"start": v(50.43, -9.48) * mm, "end": v(50.38, -9.56) * mm});
            skLineSegment(sketch, "E1148", {"start": v(50.38, -9.56) * mm, "end": v(50.36, -9.64) * mm});
            skLineSegment(sketch, "E1149", {"start": v(50.36, -9.64) * mm, "end": v(50.35, -9.71) * mm});
            skLineSegment(sketch, "E1150", {"start": v(50.35, -9.71) * mm, "end": v(50.34, -9.78) * mm});
            skLineSegment(sketch, "E1151", {"start": v(50.34, -9.78) * mm, "end": v(50.34, -9.92) * mm});
            skLineSegment(sketch, "E1152", {"start": v(50.34, -9.92) * mm, "end": v(50.35, -10.05) * mm});
            skLineSegment(sketch, "E1153", {"start": v(50.35, -10.05) * mm, "end": v(50.37, -10.18) * mm});
            skLineSegment(sketch, "E1154", {"start": v(50.37, -10.18) * mm, "end": v(50.4, -10.3) * mm});
            skLineSegment(sketch, "E1155", {"start": v(50.4, -10.3) * mm, "end": v(50.47, -10.54) * mm});
            skLineSegment(sketch, "E1156", {"start": v(50.47, -10.54) * mm, "end": v(50.52, -10.8) * mm});
            skLineSegment(sketch, "E1157", {"start": v(50.52, -10.8) * mm, "end": v(50.54, -11.06) * mm});
            skLineSegment(sketch, "E1158", {"start": v(50.54, -11.06) * mm, "end": v(50.55, -11.33) * mm});
            skLineSegment(sketch, "E1159", {"start": v(50.55, -11.33) * mm, "end": v(50.54, -11.6) * mm});
            skLineSegment(sketch, "E1160", {"start": v(50.54, -11.6) * mm, "end": v(50.52, -11.87) * mm});
            skLineSegment(sketch, "E1161", {"start": v(50.52, -11.87) * mm, "end": v(50.48, -12.15) * mm});
            skLineSegment(sketch, "E1162", {"start": v(50.48, -12.15) * mm, "end": v(50.43, -12.43) * mm});
            skLineSegment(sketch, "E1163", {"start": v(50.43, -12.43) * mm, "end": v(50.38, -12.72) * mm});
            skLineSegment(sketch, "E1164", {"start": v(50.38, -12.72) * mm, "end": v(50.3, -13) * mm});
            skLineSegment(sketch, "E1165", {"start": v(50.3, -13) * mm, "end": v(50.23, -13.3) * mm});
            skLineSegment(sketch, "E1166", {"start": v(50.23, -13.3) * mm, "end": v(50.16, -13.5) * mm});
            skLineSegment(sketch, "E1167", {"start": v(50.16, -13.5) * mm, "end": v(47.84, -13.98) * mm});
            skLineSegment(sketch, "E1168", {"start": v(47.84, -13.98) * mm, "end": v(47.7, -13.8) * mm});
            skLineSegment(sketch, "E1169", {"start": v(47.7, -13.8) * mm, "end": v(47.5, -13.57) * mm});
            skLineSegment(sketch, "E1170", {"start": v(47.5, -13.57) * mm, "end": v(47.33, -13.33) * mm});
            skLineSegment(sketch, "E1171", {"start": v(47.33, -13.33) * mm, "end": v(47.17, -13.1) * mm});
            skLineSegment(sketch, "E1172", {"start": v(47.17, -13.1) * mm, "end": v(47.01, -12.85) * mm});
            skLineSegment(sketch, "E1173", {"start": v(47.01, -12.85) * mm, "end": v(46.87, -12.6) * mm});
            skLineSegment(sketch, "E1174", {"start": v(46.87, -12.6) * mm, "end": v(46.75, -12.36) * mm});
            skLineSegment(sketch, "E1175", {"start": v(46.75, -12.36) * mm, "end": v(46.63, -12.12) * mm});
            skLineSegment(sketch, "E1176", {"start": v(46.63, -12.12) * mm, "end": v(46.54, -11.87) * mm});
            skLineSegment(sketch, "E1177", {"start": v(46.54, -11.87) * mm, "end": v(46.46, -11.62) * mm});
            skLineSegment(sketch, "E1178", {"start": v(46.46, -11.62) * mm, "end": v(46.4, -11.37) * mm});
            skLineSegment(sketch, "E1179", {"start": v(46.4, -11.37) * mm, "end": v(46.37, -11.11) * mm});
            skLineSegment(sketch, "E1180", {"start": v(46.37, -11.11) * mm, "end": v(46.35, -10.99) * mm});
            skLineSegment(sketch, "E1181", {"start": v(46.35, -10.99) * mm, "end": v(46.32, -10.86) * mm});
            skLineSegment(sketch, "E1182", {"start": v(46.32, -10.86) * mm, "end": v(46.28, -10.74) * mm});
            skLineSegment(sketch, "E1183", {"start": v(46.28, -10.74) * mm, "end": v(46.23, -10.61) * mm});
            skLineSegment(sketch, "E1184", {"start": v(46.23, -10.61) * mm, "end": v(46.2, -10.55) * mm});
            skLineSegment(sketch, "E1185", {"start": v(46.2, -10.55) * mm, "end": v(46.15, -10.49) * mm});
            skLineSegment(sketch, "E1186", {"start": v(46.15, -10.49) * mm, "end": v(46.1, -10.43) * mm});
            skLineSegment(sketch, "E1187", {"start": v(46.1, -10.43) * mm, "end": v(46.03, -10.36) * mm});
            skLineSegment(sketch, "E1188", {"start": v(46.03, -10.36) * mm, "end": v(45.85, -10.3) * mm});
            skLineSegment(sketch, "E1189", {"start": v(45.85, -10.3) * mm, "end": v(44.8, -10.28) * mm});
            skLineSegment(sketch, "E1190", {"start": v(44.8, -10.28) * mm, "end": v(43.75, -10.17) * mm});
            skLineSegment(sketch, "E1191", {"start": v(43.75, -10.17) * mm, "end": v(43.56, -10.2) * mm});
            skLineSegment(sketch, "E1192", {"start": v(43.56, -10.2) * mm, "end": v(43.48, -10.26) * mm});
            skLineSegment(sketch, "E1193", {"start": v(43.48, -10.26) * mm, "end": v(43.42, -10.32) * mm});
            skLineSegment(sketch, "E1194", {"start": v(43.42, -10.32) * mm, "end": v(43.38, -10.37) * mm});
            skLineSegment(sketch, "E1195", {"start": v(43.38, -10.37) * mm, "end": v(43.33, -10.43) * mm});
            skLineSegment(sketch, "E1196", {"start": v(43.33, -10.43) * mm, "end": v(43.27, -10.55) * mm});
            skLineSegment(sketch, "E1197", {"start": v(43.27, -10.55) * mm, "end": v(43.21, -10.67) * mm});
            skLineSegment(sketch, "E1198", {"start": v(43.21, -10.67) * mm, "end": v(43.17, -10.79) * mm});
            skLineSegment(sketch, "E1199", {"start": v(43.17, -10.79) * mm, "end": v(43.13, -10.9) * mm});
            skLineSegment(sketch, "E1200", {"start": v(43.13, -10.9) * mm, "end": v(43.07, -11.16) * mm});
            skLineSegment(sketch, "E1201", {"start": v(43.07, -11.16) * mm, "end": v(42.98, -11.4) * mm});
            skLineSegment(sketch, "E1202", {"start": v(42.98, -11.4) * mm, "end": v(42.87, -11.64) * mm});
            skLineSegment(sketch, "E1203", {"start": v(42.87, -11.64) * mm, "end": v(42.74, -11.87) * mm});
            skLineSegment(sketch, "E1204", {"start": v(42.74, -11.87) * mm, "end": v(42.6, -12.1) * mm});
            skLineSegment(sketch, "E1205", {"start": v(42.6, -12.1) * mm, "end": v(42.44, -12.33) * mm});
            skLineSegment(sketch, "E1206", {"start": v(42.44, -12.33) * mm, "end": v(42.27, -12.55) * mm});
            skLineSegment(sketch, "E1207", {"start": v(42.27, -12.55) * mm, "end": v(42.1, -12.77) * mm});
            skLineSegment(sketch, "E1208", {"start": v(42.1, -12.77) * mm, "end": v(41.9, -13) * mm});
            skLineSegment(sketch, "E1209", {"start": v(41.9, -13) * mm, "end": v(41.7, -13.2) * mm});
            skLineSegment(sketch, "E1210", {"start": v(41.7, -13.2) * mm, "end": v(41.48, -13.41) * mm});
            skLineSegment(sketch, "E1211", {"start": v(41.48, -13.41) * mm, "end": v(41.32, -13.57) * mm});
            skLineSegment(sketch, "E1212", {"start": v(41.32, -13.57) * mm, "end": v(39.07, -12.81) * mm});
            skLineSegment(sketch, "E1213", {"start": v(39.07, -12.81) * mm, "end": v(39.03, -12.59) * mm});
            skLineSegment(sketch, "E1214", {"start": v(39.03, -12.59) * mm, "end": v(38.99, -12.3) * mm});
            skLineSegment(sketch, "E1215", {"start": v(38.99, -12.3) * mm, "end": v(38.95, -12) * mm});
            skLineSegment(sketch, "E1216", {"start": v(38.95, -12) * mm, "end": v(38.93, -11.71) * mm});
            skLineSegment(sketch, "E1217", {"start": v(38.93, -11.71) * mm, "end": v(38.92, -11.43) * mm});
            skLineSegment(sketch, "E1218", {"start": v(38.92, -11.43) * mm, "end": v(38.92, -11.14) * mm});
            skLineSegment(sketch, "E1219", {"start": v(38.92, -11.14) * mm, "end": v(38.93, -10.87) * mm});
            skLineSegment(sketch, "E1220", {"start": v(38.93, -10.87) * mm, "end": v(38.96, -10.6) * mm});
            skLineSegment(sketch, "E1221", {"start": v(38.96, -10.6) * mm, "end": v(39, -10.33) * mm});
            skLineSegment(sketch, "E1222", {"start": v(39, -10.33) * mm, "end": v(39.05, -10.08) * mm});
            skLineSegment(sketch, "E1223", {"start": v(39.05, -10.08) * mm, "end": v(39.13, -9.83) * mm});
            skLineSegment(sketch, "E1224", {"start": v(39.13, -9.83) * mm, "end": v(39.23, -9.6) * mm});
            skLineSegment(sketch, "E1225", {"start": v(39.23, -9.6) * mm, "end": v(39.28, -9.48) * mm});
            skLineSegment(sketch, "E1226", {"start": v(39.28, -9.48) * mm, "end": v(39.32, -9.35) * mm});
            skLineSegment(sketch, "E1227", {"start": v(39.32, -9.35) * mm, "end": v(39.34, -9.23) * mm});
            skLineSegment(sketch, "E1228", {"start": v(39.34, -9.23) * mm, "end": v(39.36, -9.1) * mm});
            skLineSegment(sketch, "E1229", {"start": v(39.36, -9.1) * mm, "end": v(39.36, -9.02) * mm});
            skLineSegment(sketch, "E1230", {"start": v(39.36, -9.02) * mm, "end": v(39.36, -8.95) * mm});
            skLineSegment(sketch, "E1231", {"start": v(39.36, -8.95) * mm, "end": v(39.34, -8.87) * mm});
            skLineSegment(sketch, "E1232", {"start": v(39.34, -8.87) * mm, "end": v(39.31, -8.78) * mm});
            skLineSegment(sketch, "E1233", {"start": v(39.31, -8.78) * mm, "end": v(39.19, -8.64) * mm});
            skLineSegment(sketch, "E1234", {"start": v(39.19, -8.64) * mm, "end": v(38.29, -8.09) * mm});
            skLineSegment(sketch, "E1235", {"start": v(38.29, -8.09) * mm, "end": v(37.43, -7.47) * mm});
            skLineSegment(sketch, "E1236", {"start": v(37.43, -7.47) * mm, "end": v(37.25, -7.41) * mm});
            skLineSegment(sketch, "E1237", {"start": v(37.25, -7.41) * mm, "end": v(37.16, -7.42) * mm});
            skLineSegment(sketch, "E1238", {"start": v(37.16, -7.42) * mm, "end": v(37.08, -7.43) * mm});
            skLineSegment(sketch, "E1239", {"start": v(37.08, -7.43) * mm, "end": v(37.01, -7.46) * mm});
            skLineSegment(sketch, "E1240", {"start": v(37.01, -7.46) * mm, "end": v(36.95, -7.49) * mm});
            skLineSegment(sketch, "E1241", {"start": v(36.95, -7.49) * mm, "end": v(36.83, -7.55) * mm});
            skLineSegment(sketch, "E1242", {"start": v(36.83, -7.55) * mm, "end": v(36.72, -7.63) * mm});
            skLineSegment(sketch, "E1243", {"start": v(36.72, -7.63) * mm, "end": v(36.62, -7.71) * mm});
            skLineSegment(sketch, "E1244", {"start": v(36.62, -7.71) * mm, "end": v(36.53, -7.8) * mm});
            skLineSegment(sketch, "E1245", {"start": v(36.53, -7.8) * mm, "end": v(36.35, -7.99) * mm});
            skLineSegment(sketch, "E1246", {"start": v(36.35, -7.99) * mm, "end": v(36.16, -8.15) * mm});
            skLineSegment(sketch, "E1247", {"start": v(36.16, -8.15) * mm, "end": v(35.94, -8.3) * mm});
            skLineSegment(sketch, "E1248", {"start": v(35.94, -8.3) * mm, "end": v(35.71, -8.44) * mm});
            skLineSegment(sketch, "E1249", {"start": v(35.71, -8.44) * mm, "end": v(35.47, -8.57) * mm});
            skLineSegment(sketch, "E1250", {"start": v(35.47, -8.57) * mm, "end": v(35.22, -8.69) * mm});
            skLineSegment(sketch, "E1251", {"start": v(35.22, -8.69) * mm, "end": v(34.96, -8.8) * mm});
            skLineSegment(sketch, "E1252", {"start": v(34.96, -8.8) * mm, "end": v(34.7, -8.9) * mm});
            skLineSegment(sketch, "E1253", {"start": v(34.7, -8.9) * mm, "end": v(34.42, -8.99) * mm});
            skLineSegment(sketch, "E1254", {"start": v(34.42, -8.99) * mm, "end": v(34.14, -9.07) * mm});
            skLineSegment(sketch, "E1255", {"start": v(34.14, -9.07) * mm, "end": v(33.85, -9.14) * mm});
            skLineSegment(sketch, "E1256", {"start": v(33.85, -9.14) * mm, "end": v(33.63, -9.2) * mm});
            skLineSegment(sketch, "E1257", {"start": v(33.63, -9.2) * mm, "end": v(32.06, -7.42) * mm});
            skLineSegment(sketch, "E1258", {"start": v(32.06, -7.42) * mm, "end": v(32.14, -7.2) * mm});
            skLineSegment(sketch, "E1259", {"start": v(32.14, -7.2) * mm, "end": v(32.25, -6.93) * mm});
            skLineSegment(sketch, "E1260", {"start": v(32.25, -6.93) * mm, "end": v(32.37, -6.66) * mm});
            skLineSegment(sketch, "E1261", {"start": v(32.37, -6.66) * mm, "end": v(32.5, -6.4) * mm});
            skLineSegment(sketch, "E1262", {"start": v(32.5, -6.4) * mm, "end": v(32.63, -6.14) * mm});
            skLineSegment(sketch, "E1263", {"start": v(32.63, -6.14) * mm, "end": v(32.77, -5.9) * mm});
            skLineSegment(sketch, "E1264", {"start": v(32.77, -5.9) * mm, "end": v(32.92, -5.67) * mm});
            skLineSegment(sketch, "E1265", {"start": v(32.92, -5.67) * mm, "end": v(33.07, -5.45) * mm});
            skLineSegment(sketch, "E1266", {"start": v(33.07, -5.45) * mm, "end": v(33.24, -5.24) * mm});
            skLineSegment(sketch, "E1267", {"start": v(33.24, -5.24) * mm, "end": v(33.42, -5.04) * mm});
            skLineSegment(sketch, "E1268", {"start": v(33.42, -5.04) * mm, "end": v(33.6, -4.87) * mm});
            skLineSegment(sketch, "E1269", {"start": v(33.6, -4.87) * mm, "end": v(33.8, -4.72) * mm});
            skLineSegment(sketch, "E1270", {"start": v(33.8, -4.72) * mm, "end": v(33.9, -4.64) * mm});
            skLineSegment(sketch, "E1271", {"start": v(33.9, -4.64) * mm, "end": v(34, -4.55) * mm});
            skLineSegment(sketch, "E1272", {"start": v(34, -4.55) * mm, "end": v(34.1, -4.45) * mm});
            skLineSegment(sketch, "E1273", {"start": v(34.1, -4.45) * mm, "end": v(34.17, -4.34) * mm});
            skLineSegment(sketch, "E1274", {"start": v(34.17, -4.34) * mm, "end": v(34.2, -4.28) * mm});
            skLineSegment(sketch, "E1275", {"start": v(34.2, -4.28) * mm, "end": v(34.24, -4.21) * mm});
            skLineSegment(sketch, "E1276", {"start": v(34.24, -4.21) * mm, "end": v(34.27, -4.14) * mm});
            skLineSegment(sketch, "E1277", {"start": v(34.27, -4.14) * mm, "end": v(34.29, -4.05) * mm});
            skLineSegment(sketch, "E1278", {"start": v(34.29, -4.05) * mm, "end": v(34.25, -3.86) * mm});
            skLineSegment(sketch, "E1279", {"start": v(34.25, -3.86) * mm, "end": v(33.74, -2.94) * mm});
            skLineSegment(sketch, "E1280", {"start": v(33.74, -2.94) * mm, "end": v(33.31, -1.98) * mm});
            skCircle(sketch, "E1281", {"center": v(45.63, 2.96) * mm, "radius": 10.41 * mm});
            skSolve(sketch);
        }
        {
            var Q0;
            {var subQ17=sQuery(id+"F0.wireOp",EDGE,"E452");Q0=makeQuery(id+"F0.imprint","IMPRINT",FACE,{"disambiguationData":[TD([[makeQuery(id+"F0.imprint","IMPRINT",EDGE,{"derivedFrom":subQ17}),-1.0]])]});}
            var Q1;
            {var subQ7=sQuery(id+"F0.wireOp",EDGE,"E474");Q1=makeQuery(id+"F0.imprint","IMPRINT",FACE,{"disambiguationData":[TD([[makeQuery(id+"F0.imprint","IMPRINT",EDGE,{"derivedFrom":subQ7}),-1.0]])]});}
            var Q2;
            {var subQ15=sQuery(id+"F0.wireOp",EDGE,"E488");Q2=makeQuery(id+"F0.imprint","IMPRINT",FACE,{"disambiguationData":[TD([[makeQuery(id+"F0.imprint","IMPRINT",EDGE,{"derivedFrom":subQ15}),-1.0]])]});}
            var Q3;
            {var subQ7=sQuery(id+"F0.wireOp",EDGE,"E524");Q3=makeQuery(id+"F0.imprint","IMPRINT",FACE,{"disambiguationData":[TD([[makeQuery(id+"F0.imprint","IMPRINT",EDGE,{"derivedFrom":subQ7}),-1.0]])]});}
            var Q4;
            {var subQ12=sQuery(id+"F0.wireOp",EDGE,"E554");Q4=makeQuery(id+"F0.imprint","IMPRINT",FACE,{"disambiguationData":[TD([[makeQuery(id+"F0.imprint","IMPRINT",EDGE,{"derivedFrom":subQ12}),-1.0]])]});}
            var Q5;
            {var subQ0=sQuery(id+"F0.wireOp",EDGE,"E583");Q5=makeQuery(id+"F0.imprint","IMPRINT",FACE,{"disambiguationData":[TD([[makeQuery(id+"F0.imprint","IMPRINT",EDGE,{"derivedFrom":subQ0}),-1.0]])]});}
            var Q6;
            {var subQ7=sQuery(id+"F0.wireOp",EDGE,"E614");Q6=makeQuery(id+"F0.imprint","IMPRINT",FACE,{"disambiguationData":[TD([[makeQuery(id+"F0.imprint","IMPRINT",EDGE,{"derivedFrom":subQ7}),-1.0]])]});}
            var Q7;
            {var subQ15=sQuery(id+"F0.wireOp",EDGE,"E632");Q7=makeQuery(id+"F0.imprint","IMPRINT",FACE,{"disambiguationData":[TD([[makeQuery(id+"F0.imprint","IMPRINT",EDGE,{"derivedFrom":subQ15}),-1.0]])]});}
            var Q8;
            {var subQ0=sQuery(id+"F0.wireOp",EDGE,"E16");var subQ1=sQuery(id+"F0.wireOp",EDGE,"E6");var subQ2=makeQuery(id+"F0.imprint","INTERSECT",VERTEX,{"derivedFrom":[subQ1,subQ0]});Q8=makeQuery(id+"F0.imprint","IMPRINT",FACE,{"disambiguationData":[TD([[makeQuery(id+"F0.imprint","IMPRINT",EDGE,{"disambiguationData":[TD([[subQ2,-1.0]])],"derivedFrom":subQ1}),-1.0]])]});}
            var Q9;
            {var subQ10=sQuery(id+"F0.wireOp",EDGE,"E668");Q9=makeQuery(id+"F0.imprint","IMPRINT",FACE,{"disambiguationData":[TD([[makeQuery(id+"F0.imprint","IMPRINT",EDGE,{"derivedFrom":subQ10}),-1.0]])]});}
            var Q10;
            {var subQ5=sQuery(id+"F0.wireOp",EDGE,"E653");Q10=makeQuery(id+"F0.imprint","IMPRINT",FACE,{"disambiguationData":[TD([[makeQuery(id+"F0.imprint","IMPRINT",EDGE,{"derivedFrom":subQ5}),-1.0]])]});}
            var Q11;
            {var subQ5=sQuery(id+"F0.wireOp",EDGE,"E672");Q11=makeQuery(id+"F0.imprint","IMPRINT",FACE,{"disambiguationData":[TD([[makeQuery(id+"F0.imprint","IMPRINT",EDGE,{"derivedFrom":subQ5}),-1.0]])]});}
            var Q12;
            {var subQ0=sQuery(id+"F0.wireOp",EDGE,"E566");Q12=makeQuery(id+"F0.imprint","IMPRINT",FACE,{"disambiguationData":[TD([[makeQuery(id+"F0.imprint","IMPRINT",EDGE,{"derivedFrom":subQ0}),-1.0]])]});}
            var Q13;
            {var subQ0=sQuery(id+"F0.wireOp",EDGE,"E548");Q13=makeQuery(id+"F0.imprint","IMPRINT",FACE,{"disambiguationData":[TD([[makeQuery(id+"F0.imprint","IMPRINT",EDGE,{"derivedFrom":subQ0}),-1.0]])]});}
            var Q14;
            {var subQ6=sQuery(id+"F0.wireOp",EDGE,"E532");Q14=makeQuery(id+"F0.imprint","IMPRINT",FACE,{"disambiguationData":[TD([[makeQuery(id+"F0.imprint","IMPRINT",EDGE,{"derivedFrom":subQ6}),-1.0]])]});}
            var Q15;
            {var subQ5=sQuery(id+"F0.wireOp",EDGE,"E459");Q15=makeQuery(id+"F0.imprint","IMPRINT",FACE,{"disambiguationData":[TD([[makeQuery(id+"F0.imprint","IMPRINT",EDGE,{"derivedFrom":subQ5}),-1.0]])]});}
            var Q16;
            {var subQ5=sQuery(id+"F0.wireOp",EDGE,"E434");Q16=makeQuery(id+"F0.imprint","IMPRINT",FACE,{"disambiguationData":[TD([[makeQuery(id+"F0.imprint","IMPRINT",EDGE,{"derivedFrom":subQ5}),-1.0]])]});}
            var Q17;
            {var subQ5=sQuery(id+"F0.wireOp",EDGE,"E403");Q17=makeQuery(id+"F0.imprint","IMPRINT",FACE,{"disambiguationData":[TD([[makeQuery(id+"F0.imprint","IMPRINT",EDGE,{"derivedFrom":subQ5}),-1.0]])]});}
            var Q18;
            {var subQ17=sQuery(id+"F0.wireOp",EDGE,"E374");Q18=makeQuery(id+"F0.imprint","IMPRINT",FACE,{"disambiguationData":[TD([[makeQuery(id+"F0.imprint","IMPRINT",EDGE,{"derivedFrom":subQ17}),-1.0]])]});}
            var Q19;
            {var subQ0=sQuery(id+"F0.wireOp",EDGE,"E16");var subQ1=sQuery(id+"F0.wireOp",EDGE,"E1");var subQ2=makeQuery(id+"F0.imprint","INTERSECT",VERTEX,{"derivedFrom":[subQ1,subQ0]});Q19=makeQuery(id+"F0.imprint","IMPRINT",FACE,{"disambiguationData":[TD([[makeQuery(id+"F0.imprint","IMPRINT",EDGE,{"disambiguationData":[TD([[subQ2,-1.0]])],"derivedFrom":subQ1}),-1.0]])]});}
            var Q20;
            {var subQ0=sQuery(id+"F0.wireOp",EDGE,"E15");var subQ1=sQuery(id+"F0.wireOp",EDGE,"E1");var subQ2=makeQuery(id+"F0.imprint","INTERSECT",VERTEX,{"derivedFrom":[subQ1,subQ0]});Q20=makeQuery(id+"F0.imprint","IMPRINT",FACE,{"disambiguationData":[TD([[makeQuery(id+"F0.imprint","IMPRINT",EDGE,{"disambiguationData":[TD([[subQ2,-1.0]])],"derivedFrom":subQ1}),-1.0]])]});}
            var Q21;
            {var subQ0=sQuery(id+"F0.wireOp",EDGE,"E16");var subQ1=sQuery(id+"F0.wireOp",EDGE,"E2");var subQ2=makeQuery(id+"F0.imprint","INTERSECT",VERTEX,{"derivedFrom":[subQ1,subQ0]});Q21=makeQuery(id+"F0.imprint","IMPRINT",FACE,{"disambiguationData":[TD([[makeQuery(id+"F0.imprint","IMPRINT",EDGE,{"disambiguationData":[TD([[subQ2,-1.0]])],"derivedFrom":subQ1}),-1.0]])]});}
            var Q22;
            {var subQ0=sQuery(id+"F0.wireOp",EDGE,"E15");var subQ1=sQuery(id+"F0.wireOp",EDGE,"E2");var subQ2=makeQuery(id+"F0.imprint","INTERSECT",VERTEX,{"derivedFrom":[subQ1,subQ0]});Q22=makeQuery(id+"F0.imprint","IMPRINT",FACE,{"disambiguationData":[TD([[makeQuery(id+"F0.imprint","IMPRINT",EDGE,{"disambiguationData":[TD([[subQ2,-1.0]])],"derivedFrom":subQ1}),-1.0]])]});}
            var Q23;
            {var subQ0=sQuery(id+"F0.wireOp",EDGE,"E16");var subQ1=sQuery(id+"F0.wireOp",EDGE,"E3");var subQ2=makeQuery(id+"F0.imprint","INTERSECT",VERTEX,{"derivedFrom":[subQ1,subQ0]});Q23=makeQuery(id+"F0.imprint","IMPRINT",FACE,{"disambiguationData":[TD([[makeQuery(id+"F0.imprint","IMPRINT",EDGE,{"disambiguationData":[TD([[subQ2,-1.0]])],"derivedFrom":subQ1}),-1.0]])]});}
            var Q24;
            {var subQ0=sQuery(id+"F0.wireOp",EDGE,"E15");var subQ1=sQuery(id+"F0.wireOp",EDGE,"E3");var subQ2=makeQuery(id+"F0.imprint","INTERSECT",VERTEX,{"derivedFrom":[subQ1,subQ0]});Q24=makeQuery(id+"F0.imprint","IMPRINT",FACE,{"disambiguationData":[TD([[makeQuery(id+"F0.imprint","IMPRINT",EDGE,{"disambiguationData":[TD([[subQ2,-1.0]])],"derivedFrom":subQ1}),-1.0]])]});}
            var Q25;
            {var subQ1=sQuery(id+"F0.wireOp",EDGE,"E4");var subQ7=sQuery(id+"F0.wireOp",EDGE,"E740");var subQ9=makeQuery(id+"F0.imprint","INTERSECT",VERTEX,{"disambiguationData":[OD(1.0)],"derivedFrom":[subQ1,subQ7]});Q25=makeQuery(id+"F0.imprint","IMPRINT",FACE,{"disambiguationData":[TD([[makeQuery(id+"F0.imprint","IMPRINT",EDGE,{"disambiguationData":[TD([[subQ9,-1.0]])],"derivedFrom":subQ1}),-1.0]])]});}
            var Q26;
            {var subQ0=sQuery(id+"F0.wireOp",EDGE,"E17");var subQ1=sQuery(id+"F0.wireOp",EDGE,"E2");var subQ2=makeQuery(id+"F0.imprint","INTERSECT",VERTEX,{"derivedFrom":[subQ1,subQ0]});Q26=makeQuery(id+"F0.imprint","IMPRINT",FACE,{"disambiguationData":[TD([[makeQuery(id+"F0.imprint","IMPRINT",EDGE,{"disambiguationData":[TD([[subQ2,-1.0]])],"derivedFrom":subQ1}),-1.0]])]});}
            var Q27;
            {var subQ0=sQuery(id+"F0.wireOp",EDGE,"E17");var subQ1=sQuery(id+"F0.wireOp",EDGE,"E3");var subQ2=makeQuery(id+"F0.imprint","INTERSECT",VERTEX,{"derivedFrom":[subQ1,subQ0]});Q27=makeQuery(id+"F0.imprint","IMPRINT",FACE,{"disambiguationData":[TD([[makeQuery(id+"F0.imprint","IMPRINT",EDGE,{"disambiguationData":[TD([[subQ2,-1.0]])],"derivedFrom":subQ1}),-1.0]])]});}
            var Q28;
            {var subQ0=sQuery(id+"F0.wireOp",EDGE,"E17");var subQ1=sQuery(id+"F0.wireOp",EDGE,"E4");var subQ2=makeQuery(id+"F0.imprint","INTERSECT",VERTEX,{"derivedFrom":[subQ1,subQ0]});Q28=makeQuery(id+"F0.imprint","IMPRINT",FACE,{"disambiguationData":[TD([[makeQuery(id+"F0.imprint","IMPRINT",EDGE,{"disambiguationData":[TD([[subQ2,-1.0]])],"derivedFrom":subQ1}),-1.0]])]});}
            var Q29;
            {var subQ0=sQuery(id+"F0.wireOp",EDGE,"E16");var subQ1=sQuery(id+"F0.wireOp",EDGE,"E5");var subQ2=makeQuery(id+"F0.imprint","INTERSECT",VERTEX,{"derivedFrom":[subQ1,subQ0]});Q29=makeQuery(id+"F0.imprint","IMPRINT",FACE,{"disambiguationData":[TD([[makeQuery(id+"F0.imprint","IMPRINT",EDGE,{"disambiguationData":[TD([[subQ2,-1.0]])],"derivedFrom":subQ1}),-1.0]])]});}
            var Q30;
            {var subQ0=sQuery(id+"F0.wireOp",EDGE,"E17");var subQ1=sQuery(id+"F0.wireOp",EDGE,"E5");var subQ2=makeQuery(id+"F0.imprint","INTERSECT",VERTEX,{"derivedFrom":[subQ1,subQ0]});Q30=makeQuery(id+"F0.imprint","IMPRINT",FACE,{"disambiguationData":[TD([[makeQuery(id+"F0.imprint","IMPRINT",EDGE,{"disambiguationData":[TD([[subQ2,-1.0]])],"derivedFrom":subQ1}),-1.0]])]});}
            var Q31;
            {var subQ0=sQuery(id+"F0.wireOp",EDGE,"E15");var subQ1=sQuery(id+"F0.wireOp",EDGE,"E6");var subQ2=makeQuery(id+"F0.imprint","INTERSECT",VERTEX,{"derivedFrom":[subQ1,subQ0]});Q31=makeQuery(id+"F0.imprint","IMPRINT",FACE,{"disambiguationData":[TD([[makeQuery(id+"F0.imprint","IMPRINT",EDGE,{"disambiguationData":[TD([[subQ2,-1.0]])],"derivedFrom":subQ1}),-1.0]])]});}
            var Q32;
            {var subQ9=sQuery(id+"F0.wireOp",EDGE,"E704");Q32=makeQuery(id+"F0.imprint","IMPRINT",FACE,{"disambiguationData":[TD([[makeQuery(id+"F0.imprint","IMPRINT",EDGE,{"derivedFrom":subQ9}),-1.0]])]});}
            var Q33;
            {var subQ16=sQuery(id+"F0.wireOp",EDGE,"E344");Q33=makeQuery(id+"F0.imprint","IMPRINT",FACE,{"disambiguationData":[TD([[makeQuery(id+"F0.imprint","IMPRINT",EDGE,{"derivedFrom":subQ16}),-1.0]])]});}
            var Q34;
            {var subQ0=sQuery(id+"F0.wireOp",EDGE,"E14");var subQ1=sQuery(id+"F0.wireOp",EDGE,"E1");var subQ2=makeQuery(id+"F0.imprint","INTERSECT",VERTEX,{"derivedFrom":[subQ1,subQ0]});Q34=makeQuery(id+"F0.imprint","IMPRINT",FACE,{"disambiguationData":[TD([[makeQuery(id+"F0.imprint","IMPRINT",EDGE,{"disambiguationData":[TD([[subQ2,-1.0]])],"derivedFrom":subQ1}),-1.0]])]});}
            var Q35;
            {var subQ0=sQuery(id+"F0.wireOp",EDGE,"E14");var subQ1=sQuery(id+"F0.wireOp",EDGE,"E2");var subQ2=makeQuery(id+"F0.imprint","INTERSECT",VERTEX,{"derivedFrom":[subQ1,subQ0]});Q35=makeQuery(id+"F0.imprint","IMPRINT",FACE,{"disambiguationData":[TD([[makeQuery(id+"F0.imprint","IMPRINT",EDGE,{"disambiguationData":[TD([[subQ2,-1.0]])],"derivedFrom":subQ1}),-1.0]])]});}
            var Q36;
            {var subQ1=sQuery(id+"F0.wireOp",EDGE,"E3");var subQ5=sQuery(id+"F0.wireOp",EDGE,"E14");var subQ6=makeQuery(id+"F0.imprint","INTERSECT",VERTEX,{"derivedFrom":[subQ1,subQ5]});Q36=makeQuery(id+"F0.imprint","IMPRINT",FACE,{"disambiguationData":[TD([[makeQuery(id+"F0.imprint","IMPRINT",EDGE,{"disambiguationData":[TD([[subQ6,-1.0]])],"derivedFrom":subQ1}),-1.0]])]});}
            var Q37;
            {var subQ5=sQuery(id+"F0.wireOp",EDGE,"E14");var subQ6=sQuery(id+"F0.wireOp",EDGE,"E4");var subQ7=makeQuery(id+"F0.imprint","INTERSECT",VERTEX,{"derivedFrom":[subQ6,subQ5]});Q37=makeQuery(id+"F0.imprint","IMPRINT",FACE,{"disambiguationData":[TD([[makeQuery(id+"F0.imprint","IMPRINT",EDGE,{"disambiguationData":[TD([[subQ7,-1.0]])],"derivedFrom":subQ6}),-1.0]])]});}
            var Q38;
            {var subQ0=sQuery(id+"F0.wireOp",EDGE,"E14");var subQ1=sQuery(id+"F0.wireOp",EDGE,"E5");var subQ2=makeQuery(id+"F0.imprint","INTERSECT",VERTEX,{"derivedFrom":[subQ1,subQ0]});Q38=makeQuery(id+"F0.imprint","IMPRINT",FACE,{"disambiguationData":[TD([[makeQuery(id+"F0.imprint","IMPRINT",EDGE,{"disambiguationData":[TD([[subQ2,-1.0]])],"derivedFrom":subQ1}),-1.0]])]});}
            var Q39;
            {var subQ0=sQuery(id+"F0.wireOp",EDGE,"E14");var subQ1=sQuery(id+"F0.wireOp",EDGE,"E6");var subQ2=makeQuery(id+"F0.imprint","INTERSECT",VERTEX,{"derivedFrom":[subQ1,subQ0]});Q39=makeQuery(id+"F0.imprint","IMPRINT",FACE,{"disambiguationData":[TD([[makeQuery(id+"F0.imprint","IMPRINT",EDGE,{"disambiguationData":[TD([[subQ2,-1.0]])],"derivedFrom":subQ1}),-1.0]])]});}
            var Q40;
            Q40=makeQuery(id+"F0.imprint","IMPRINT",FACE,{"disambiguationData":[TD([[makeQuery(id+"F0.imprint","IMPRINT",EDGE,{"derivedFrom":sQuery(id+"F0.wireOp",EDGE,"E20")}),-1.0]])]});
            var Q41;
            {var subQ0=sQuery(id+"F0.wireOp",EDGE,"E43");Q41=makeQuery(id+"F0.imprint","IMPRINT",FACE,{"disambiguationData":[TD([[makeQuery(id+"F0.imprint","IMPRINT",EDGE,{"derivedFrom":subQ0}),-1.0]])]});}
            var Q42;
            {var subQ0=sQuery(id+"F0.wireOp",EDGE,"E13");var subQ1=sQuery(id+"F0.wireOp",EDGE,"E6");var subQ2=makeQuery(id+"F0.imprint","INTERSECT",VERTEX,{"derivedFrom":[subQ1,subQ0]});Q42=makeQuery(id+"F0.imprint","IMPRINT",FACE,{"disambiguationData":[TD([[makeQuery(id+"F0.imprint","IMPRINT",EDGE,{"disambiguationData":[TD([[subQ2,-1.0]])],"derivedFrom":subQ1}),-1.0]])]});}
            var Q43;
            {var subQ0=sQuery(id+"F0.wireOp",EDGE,"E13");var subQ1=sQuery(id+"F0.wireOp",EDGE,"E5");var subQ2=makeQuery(id+"F0.imprint","INTERSECT",VERTEX,{"derivedFrom":[subQ1,subQ0]});Q43=makeQuery(id+"F0.imprint","IMPRINT",FACE,{"disambiguationData":[TD([[makeQuery(id+"F0.imprint","IMPRINT",EDGE,{"disambiguationData":[TD([[subQ2,-1.0]])],"derivedFrom":subQ1}),-1.0]])]});}
            var Q44;
            {var subQ0=sQuery(id+"F0.wireOp",EDGE,"E13");var subQ1=sQuery(id+"F0.wireOp",EDGE,"E4");var subQ2=makeQuery(id+"F0.imprint","INTERSECT",VERTEX,{"derivedFrom":[subQ1,subQ0]});Q44=makeQuery(id+"F0.imprint","IMPRINT",FACE,{"disambiguationData":[TD([[makeQuery(id+"F0.imprint","IMPRINT",EDGE,{"disambiguationData":[TD([[subQ2,-1.0]])],"derivedFrom":subQ1}),-1.0]])]});}
            var Q45;
            {var subQ0=sQuery(id+"F0.wireOp",EDGE,"E13");var subQ1=sQuery(id+"F0.wireOp",EDGE,"E3");var subQ2=makeQuery(id+"F0.imprint","INTERSECT",VERTEX,{"derivedFrom":[subQ1,subQ0]});Q45=makeQuery(id+"F0.imprint","IMPRINT",FACE,{"disambiguationData":[TD([[makeQuery(id+"F0.imprint","IMPRINT",EDGE,{"disambiguationData":[TD([[subQ2,-1.0]])],"derivedFrom":subQ1}),-1.0]])]});}
            var Q46;
            {var subQ0=sQuery(id+"F0.wireOp",EDGE,"E13");var subQ1=sQuery(id+"F0.wireOp",EDGE,"E2");var subQ2=makeQuery(id+"F0.imprint","INTERSECT",VERTEX,{"derivedFrom":[subQ1,subQ0]});Q46=makeQuery(id+"F0.imprint","IMPRINT",FACE,{"disambiguationData":[TD([[makeQuery(id+"F0.imprint","IMPRINT",EDGE,{"disambiguationData":[TD([[subQ2,-1.0]])],"derivedFrom":subQ1}),-1.0]])]});}
            var Q47;
            {var subQ0=sQuery(id+"F0.wireOp",EDGE,"E13");var subQ1=sQuery(id+"F0.wireOp",EDGE,"E1");var subQ2=makeQuery(id+"F0.imprint","INTERSECT",VERTEX,{"derivedFrom":[subQ1,subQ0]});Q47=makeQuery(id+"F0.imprint","IMPRINT",FACE,{"disambiguationData":[TD([[makeQuery(id+"F0.imprint","IMPRINT",EDGE,{"disambiguationData":[TD([[subQ2,-1.0]])],"derivedFrom":subQ1}),-1.0]])]});}
            var Q48;
            {var subQ6=sQuery(id+"F0.wireOp",EDGE,"E308");Q48=makeQuery(id+"F0.imprint","IMPRINT",FACE,{"disambiguationData":[TD([[makeQuery(id+"F0.imprint","IMPRINT",EDGE,{"derivedFrom":subQ6}),-1.0]])]});}
            var Q49;
            {var subQ17=sQuery(id+"F0.wireOp",EDGE,"E272");Q49=makeQuery(id+"F0.imprint","IMPRINT",FACE,{"disambiguationData":[TD([[makeQuery(id+"F0.imprint","IMPRINT",EDGE,{"derivedFrom":subQ17}),-1.0]])]});}
            var Q50;
            {var subQ0=sQuery(id+"F0.wireOp",EDGE,"E12");var subQ1=sQuery(id+"F0.wireOp",EDGE,"E2");var subQ2=makeQuery(id+"F0.imprint","INTERSECT",VERTEX,{"derivedFrom":[subQ1,subQ0]});Q50=makeQuery(id+"F0.imprint","IMPRINT",FACE,{"disambiguationData":[TD([[makeQuery(id+"F0.imprint","IMPRINT",EDGE,{"disambiguationData":[TD([[subQ2,-1.0]])],"derivedFrom":subQ1}),-1.0]])]});}
            var Q51;
            {var subQ0=sQuery(id+"F0.wireOp",EDGE,"E12");var subQ1=sQuery(id+"F0.wireOp",EDGE,"E3");var subQ2=makeQuery(id+"F0.imprint","INTERSECT",VERTEX,{"derivedFrom":[subQ1,subQ0]});Q51=makeQuery(id+"F0.imprint","IMPRINT",FACE,{"disambiguationData":[TD([[makeQuery(id+"F0.imprint","IMPRINT",EDGE,{"disambiguationData":[TD([[subQ2,-1.0]])],"derivedFrom":subQ1}),-1.0]])]});}
            var Q52;
            {var subQ17=sQuery(id+"F0.wireOp",EDGE,"E92");Q52=makeQuery(id+"F0.imprint","IMPRINT",FACE,{"disambiguationData":[TD([[makeQuery(id+"F0.imprint","IMPRINT",EDGE,{"derivedFrom":subQ17}),-1.0]])]});}
            var Q53;
            {var subQ0=sQuery(id+"F0.wireOp",EDGE,"E12");var subQ1=sQuery(id+"F0.wireOp",EDGE,"E4");var subQ2=makeQuery(id+"F0.imprint","INTERSECT",VERTEX,{"derivedFrom":[subQ1,subQ0]});Q53=makeQuery(id+"F0.imprint","IMPRINT",FACE,{"disambiguationData":[TD([[makeQuery(id+"F0.imprint","IMPRINT",EDGE,{"disambiguationData":[TD([[subQ2,-1.0]])],"derivedFrom":subQ1}),-1.0]])]});}
            var Q54;
            {var subQ0=sQuery(id+"F0.wireOp",EDGE,"E12");var subQ1=sQuery(id+"F0.wireOp",EDGE,"E5");var subQ2=makeQuery(id+"F0.imprint","INTERSECT",VERTEX,{"derivedFrom":[subQ1,subQ0]});Q54=makeQuery(id+"F0.imprint","IMPRINT",FACE,{"disambiguationData":[TD([[makeQuery(id+"F0.imprint","IMPRINT",EDGE,{"disambiguationData":[TD([[subQ2,-1.0]])],"derivedFrom":subQ1}),-1.0]])]});}
            var Q55;
            {var subQ5=sQuery(id+"F0.wireOp",EDGE,"E128");Q55=makeQuery(id+"F0.imprint","IMPRINT",FACE,{"disambiguationData":[TD([[makeQuery(id+"F0.imprint","IMPRINT",EDGE,{"derivedFrom":subQ5}),-1.0]])]});}
            var Q56;
            {var subQ17=sQuery(id+"F0.wireOp",EDGE,"E164");Q56=makeQuery(id+"F0.imprint","IMPRINT",FACE,{"disambiguationData":[TD([[makeQuery(id+"F0.imprint","IMPRINT",EDGE,{"derivedFrom":subQ17}),-1.0]])]});}
            var Q57;
            {var subQ17=sQuery(id+"F0.wireOp",EDGE,"E194");Q57=makeQuery(id+"F0.imprint","IMPRINT",FACE,{"disambiguationData":[TD([[makeQuery(id+"F0.imprint","IMPRINT",EDGE,{"derivedFrom":subQ17}),-1.0]])]});}
            var Q58;
            {var subQ5=sQuery(id+"F0.wireOp",EDGE,"E224");Q58=makeQuery(id+"F0.imprint","IMPRINT",FACE,{"disambiguationData":[TD([[makeQuery(id+"F0.imprint","IMPRINT",EDGE,{"derivedFrom":subQ5}),-1.0]])]});}
            var Q59;
            {var subQ7=sQuery(id+"F0.wireOp",EDGE,"E294");Q59=makeQuery(id+"F0.imprint","IMPRINT",FACE,{"disambiguationData":[TD([[makeQuery(id+"F0.imprint","IMPRINT",EDGE,{"derivedFrom":subQ7}),-1.0]])]});}
            var Q60;
            {var subQ7=sQuery(id+"F0.wireOp",EDGE,"E254");Q60=makeQuery(id+"F0.imprint","IMPRINT",FACE,{"disambiguationData":[TD([[makeQuery(id+"F0.imprint","IMPRINT",EDGE,{"derivedFrom":subQ7}),-1.0]])]});}
            var Q61;
            {var subQ0=sQuery(id+"F0.wireOp",EDGE,"E188");Q61=makeQuery(id+"F0.imprint","IMPRINT",FACE,{"disambiguationData":[TD([[makeQuery(id+"F0.imprint","IMPRINT",EDGE,{"derivedFrom":subQ0}),-1.0]])]});}
            var Q62;
            {var subQ0=sQuery(id+"F0.wireOp",EDGE,"E206");Q62=makeQuery(id+"F0.imprint","IMPRINT",FACE,{"disambiguationData":[TD([[makeQuery(id+"F0.imprint","IMPRINT",EDGE,{"derivedFrom":subQ0}),-1.0]])]});}
            var Q63;
            {var subQ0=sQuery(id+"F0.wireOp",EDGE,"E191");Q63=makeQuery(id+"F0.imprint","IMPRINT",FACE,{"disambiguationData":[TD([[makeQuery(id+"F0.imprint","IMPRINT",EDGE,{"derivedFrom":subQ0}),-1.0]])]});}
            var Q64;
            {var subQ0=sQuery(id+"F0.wireOp",EDGE,"E172");Q64=makeQuery(id+"F0.imprint","IMPRINT",FACE,{"disambiguationData":[TD([[makeQuery(id+"F0.imprint","IMPRINT",EDGE,{"derivedFrom":subQ0}),-1.0]])]});}
            var Q65;
            {var subQ7=sQuery(id+"F0.wireOp",EDGE,"E114");Q65=makeQuery(id+"F0.imprint","IMPRINT",FACE,{"disambiguationData":[TD([[makeQuery(id+"F0.imprint","IMPRINT",EDGE,{"derivedFrom":subQ7}),-1.0]])]});}
            var Q66;
            {var subQ0=sQuery(id+"F0.wireOp",EDGE,"E131");Q66=makeQuery(id+"F0.imprint","IMPRINT",FACE,{"disambiguationData":[TD([[makeQuery(id+"F0.imprint","IMPRINT",EDGE,{"derivedFrom":subQ0}),-1.0]])]});}
            var Q67;
            {var subQ7=sQuery(id+"F0.wireOp",EDGE,"E74");Q67=makeQuery(id+"F0.imprint","IMPRINT",FACE,{"disambiguationData":[TD([[makeQuery(id+"F0.imprint","IMPRINT",EDGE,{"derivedFrom":subQ7}),-1.0]])]});}
            var Q68;
            {var subQ0=sQuery(id+"F0.wireOp",EDGE,"E15");var subQ1=sQuery(id+"F0.wireOp",EDGE,"E5");var subQ2=makeQuery(id+"F0.imprint","INTERSECT",VERTEX,{"derivedFrom":[subQ1,subQ0]});Q68=makeQuery(id+"F0.imprint","IMPRINT",FACE,{"disambiguationData":[TD([[makeQuery(id+"F0.imprint","IMPRINT",EDGE,{"disambiguationData":[TD([[subQ2,-1.0]])],"derivedFrom":subQ1}),-1.0]])]});}
            var Q69;
            {var subQ0=sQuery(id+"F0.wireOp",EDGE,"E16");var subQ1=sQuery(id+"F0.wireOp",EDGE,"E4");var subQ2=makeQuery(id+"F0.imprint","INTERSECT",VERTEX,{"derivedFrom":[subQ1,subQ0]});Q69=makeQuery(id+"F0.imprint","IMPRINT",FACE,{"disambiguationData":[TD([[makeQuery(id+"F0.imprint","IMPRINT",EDGE,{"disambiguationData":[TD([[subQ2,-1.0]])],"derivedFrom":subQ1}),-1.0]])]});}
            var Q70;
            {var subQ0=sQuery(id+"F0.wireOp",EDGE,"E98");Q70=makeQuery(id+"F0.imprint","IMPRINT",FACE,{"disambiguationData":[TD([[makeQuery(id+"F0.imprint","IMPRINT",EDGE,{"derivedFrom":subQ0}),-1.0]])]});}
            var Q71;
            {var subQ0=sQuery(id+"F0.wireOp",EDGE,"E711");Q71=makeQuery(id+"F0.imprint","IMPRINT",FACE,{"disambiguationData":[TD([[makeQuery(id+"F0.imprint","IMPRINT",EDGE,{"derivedFrom":subQ0}),-1.0]])]});}
            var Q72;
            {var subQ0=sQuery(id+"F0.wireOp",EDGE,"E26");Q72=makeQuery(id+"F0.imprint","IMPRINT",FACE,{"disambiguationData":[TD([[makeQuery(id+"F0.imprint","IMPRINT",EDGE,{"derivedFrom":subQ0}),-1.0]])]});}
            var Q73;
            {var subQ0=sQuery(id+"F0.wireOp",EDGE,"E732");Q73=makeQuery(id+"F0.imprint","IMPRINT",FACE,{"disambiguationData":[TD([[makeQuery(id+"F0.imprint","IMPRINT",EDGE,{"derivedFrom":subQ0}),-1.0]])]});}
            var Q74;
            {var subQ0=sQuery(id+"F0.wireOp",EDGE,"E728");Q74=makeQuery(id+"F0.imprint","IMPRINT",FACE,{"disambiguationData":[TD([[makeQuery(id+"F0.imprint","IMPRINT",EDGE,{"derivedFrom":subQ0}),-1.0]])]});}
            var Q75;
            {var subQ0=sQuery(id+"F0.wireOp",EDGE,"E368");Q75=makeQuery(id+"F0.imprint","IMPRINT",FACE,{"disambiguationData":[TD([[makeQuery(id+"F0.imprint","IMPRINT",EDGE,{"derivedFrom":subQ0}),-1.0]])]});}
            var Q76;
            {var subQ1=sQuery(id+"F0.wireOp",EDGE,"E352");Q76=makeQuery(id+"F0.imprint","IMPRINT",FACE,{"disambiguationData":[TD([[makeQuery(id+"F0.imprint","IMPRINT",EDGE,{"derivedFrom":subQ1}),-1.0]])]});}
            var Q77;
            {var subQ0=sQuery(id+"F0.wireOp",EDGE,"E387");Q77=makeQuery(id+"F0.imprint","IMPRINT",FACE,{"disambiguationData":[TD([[makeQuery(id+"F0.imprint","IMPRINT",EDGE,{"derivedFrom":subQ0}),-1.0]])]});}
            var Q78;
            {var subQ0=sQuery(id+"F0.wireOp",EDGE,"E371");Q78=makeQuery(id+"F0.imprint","IMPRINT",FACE,{"disambiguationData":[TD([[makeQuery(id+"F0.imprint","IMPRINT",EDGE,{"derivedFrom":subQ0}),-1.0]])]});}
            var Q79;
            {var subQ1=sQuery(id+"F0.wireOp",EDGE,"E494");Q79=makeQuery(id+"F0.imprint","IMPRINT",FACE,{"disambiguationData":[TD([[makeQuery(id+"F0.imprint","IMPRINT",EDGE,{"derivedFrom":subQ1}),-1.0]])]});}
            var Q80;
            {var subQ0=sQuery(id+"F0.wireOp",EDGE,"E551");Q80=makeQuery(id+"F0.imprint","IMPRINT",FACE,{"disambiguationData":[TD([[makeQuery(id+"F0.imprint","IMPRINT",EDGE,{"derivedFrom":subQ0}),-1.0]])]});}
            var Q81;
            {var subQ1=sQuery(id+"F0.wireOp",EDGE,"E638");Q81=makeQuery(id+"F0.imprint","IMPRINT",FACE,{"disambiguationData":[TD([[makeQuery(id+"F0.imprint","IMPRINT",EDGE,{"derivedFrom":subQ1}),-1.0]])]});}
            extrude(context, id + "F1", {"entities" : qUnion([Q0, Q1, Q2, Q3, Q4, Q5, Q6, Q7, Q8, Q9, Q10, Q11, Q12, Q13, Q14, Q15, Q16, Q17, Q18, Q19, Q20, Q21, Q22, Q23, Q24, Q25, Q26, Q27, Q28, Q29, Q30, Q31, Q32, Q33, Q34, Q35, Q36, Q37, Q38, Q39, Q40, Q41, Q42, Q43, Q44, Q45, Q46, Q47, Q48, Q49, Q50, Q51, Q52, Q53, Q54, Q55, Q56, Q57, Q58, Q59, Q60, Q61, Q62, Q63, Q64, Q65, Q66, Q67, Q68, Q69, Q70, Q71, Q72, Q73, Q74, Q75, Q76, Q77, Q78, Q79, Q80, Q81]), "depth" : 2.54 * mm, "offsetDistance" : 25.4 * mm});
        }
        {
            var Q0;
            Q0=makeQuery(id+"F1.opExtrude","CAP_FACE",FACE,{"disambiguationData":[OSD([sQuery(id+"F0.wireOp",EDGE,"E12"),sQuery(id+"F0.wireOp",EDGE,"E13"),sQuery(id+"F0.wireOp",EDGE,"E20"),sQuery(id+"F0.wireOp",EDGE,"E21"),sQuery(id+"F0.wireOp",EDGE,"E22"),sQuery(id+"F0.wireOp",EDGE,"E23"),sQuery(id+"F0.wireOp",EDGE,"E24"),sQuery(id+"F0.wireOp",EDGE,"E25"),sQuery(id+"F0.wireOp",EDGE,"E26"),sQuery(id+"F0.wireOp",EDGE,"E27"),sQuery(id+"F0.wireOp",EDGE,"E28"),sQuery(id+"F0.wireOp",EDGE,"E29"),sQuery(id+"F0.wireOp",EDGE,"E30"),sQuery(id+"F0.wireOp",EDGE,"E31"),sQuery(id+"F0.wireOp",EDGE,"E32"),sQuery(id+"F0.wireOp",EDGE,"E33"),sQuery(id+"F0.wireOp",EDGE,"E34"),sQuery(id+"F0.wireOp",EDGE,"E35"),sQuery(id+"F0.wireOp",EDGE,"E36"),sQuery(id+"F0.wireOp",EDGE,"E37"),sQuery(id+"F0.wireOp",EDGE,"E38"),sQuery(id+"F0.wireOp",EDGE,"E39"),sQuery(id+"F0.wireOp",EDGE,"E40"),sQuery(id+"F0.wireOp",EDGE,"E41"),sQuery(id+"F0.wireOp",EDGE,"E42"),sQuery(id+"F0.wireOp",EDGE,"E43"),sQuery(id+"F0.wireOp",EDGE,"E44"),sQuery(id+"F0.wireOp",EDGE,"E45"),sQuery(id+"F0.wireOp",EDGE,"E46"),sQuery(id+"F0.wireOp",EDGE,"E47"),sQuery(id+"F0.wireOp",EDGE,"E48"),sQuery(id+"F0.wireOp",EDGE,"E49"),sQuery(id+"F0.wireOp",EDGE,"E50"),sQuery(id+"F0.wireOp",EDGE,"E51"),sQuery(id+"F0.wireOp",EDGE,"E52"),sQuery(id+"F0.wireOp",EDGE,"E53"),sQuery(id+"F0.wireOp",EDGE,"E54"),sQuery(id+"F0.wireOp",EDGE,"E55"),sQuery(id+"F0.wireOp",EDGE,"E56"),sQuery(id+"F0.wireOp",EDGE,"E57"),sQuery(id+"F0.wireOp",EDGE,"E58"),sQuery(id+"F0.wireOp",EDGE,"E59"),sQuery(id+"F0.wireOp",EDGE,"E60"),sQuery(id+"F0.wireOp",EDGE,"E61"),sQuery(id+"F0.wireOp",EDGE,"E62"),sQuery(id+"F0.wireOp",EDGE,"E63"),sQuery(id+"F0.wireOp",EDGE,"E64"),sQuery(id+"F0.wireOp",EDGE,"E65"),sQuery(id+"F0.wireOp",EDGE,"E66"),sQuery(id+"F0.wireOp",EDGE,"E67"),sQuery(id+"F0.wireOp",EDGE,"E68"),sQuery(id+"F0.wireOp",EDGE,"E69"),sQuery(id+"F0.wireOp",EDGE,"E70"),sQuery(id+"F0.wireOp",EDGE,"E71"),sQuery(id+"F0.wireOp",EDGE,"E72"),sQuery(id+"F0.wireOp",EDGE,"E73"),sQuery(id+"F0.wireOp",EDGE,"E74"),sQuery(id+"F0.wireOp",EDGE,"E75"),sQuery(id+"F0.wireOp",EDGE,"E76"),sQuery(id+"F0.wireOp",EDGE,"E77"),sQuery(id+"F0.wireOp",EDGE,"E78"),sQuery(id+"F0.wireOp",EDGE,"E79"),sQuery(id+"F0.wireOp",EDGE,"E80"),sQuery(id+"F0.wireOp",EDGE,"E81"),sQuery(id+"F0.wireOp",EDGE,"E82"),sQuery(id+"F0.wireOp",EDGE,"E83"),sQuery(id+"F0.wireOp",EDGE,"E84"),sQuery(id+"F0.wireOp",EDGE,"E85"),sQuery(id+"F0.wireOp",EDGE,"E86"),sQuery(id+"F0.wireOp",EDGE,"E87"),sQuery(id+"F0.wireOp",EDGE,"E88"),sQuery(id+"F0.wireOp",EDGE,"E89"),sQuery(id+"F0.wireOp",EDGE,"E90"),sQuery(id+"F0.wireOp",EDGE,"E91"),sQuery(id+"F0.wireOp",EDGE,"E92"),sQuery(id+"F0.wireOp",EDGE,"E93"),sQuery(id+"F0.wireOp",EDGE,"E94"),sQuery(id+"F0.wireOp",EDGE,"E95"),sQuery(id+"F0.wireOp",EDGE,"E96"),sQuery(id+"F0.wireOp",EDGE,"E97"),sQuery(id+"F0.wireOp",EDGE,"E98"),sQuery(id+"F0.wireOp",EDGE,"E99"),sQuery(id+"F0.wireOp",EDGE,"E100"),sQuery(id+"F0.wireOp",EDGE,"E101"),sQuery(id+"F0.wireOp",EDGE,"E102"),sQuery(id+"F0.wireOp",EDGE,"E103"),sQuery(id+"F0.wireOp",EDGE,"E104"),sQuery(id+"F0.wireOp",EDGE,"E105"),sQuery(id+"F0.wireOp",EDGE,"E106"),sQuery(id+"F0.wireOp",EDGE,"E107"),sQuery(id+"F0.wireOp",EDGE,"E108"),sQuery(id+"F0.wireOp",EDGE,"E109"),sQuery(id+"F0.wireOp",EDGE,"E110"),sQuery(id+"F0.wireOp",EDGE,"E111"),sQuery(id+"F0.wireOp",EDGE,"E112"),sQuery(id+"F0.wireOp",EDGE,"E113"),sQuery(id+"F0.wireOp",EDGE,"E114"),sQuery(id+"F0.wireOp",EDGE,"E115"),sQuery(id+"F0.wireOp",EDGE,"E116"),sQuery(id+"F0.wireOp",EDGE,"E117"),sQuery(id+"F0.wireOp",EDGE,"E118"),sQuery(id+"F0.wireOp",EDGE,"E119"),sQuery(id+"F0.wireOp",EDGE,"E120"),sQuery(id+"F0.wireOp",EDGE,"E121"),sQuery(id+"F0.wireOp",EDGE,"E122"),sQuery(id+"F0.wireOp",EDGE,"E123"),sQuery(id+"F0.wireOp",EDGE,"E124"),sQuery(id+"F0.wireOp",EDGE,"E125"),sQuery(id+"F0.wireOp",EDGE,"E126"),sQuery(id+"F0.wireOp",EDGE,"E127"),sQuery(id+"F0.wireOp",EDGE,"E128"),sQuery(id+"F0.wireOp",EDGE,"E129"),sQuery(id+"F0.wireOp",EDGE,"E130"),sQuery(id+"F0.wireOp",EDGE,"E131"),sQuery(id+"F0.wireOp",EDGE,"E132"),sQuery(id+"F0.wireOp",EDGE,"E133"),sQuery(id+"F0.wireOp",EDGE,"E134"),sQuery(id+"F0.wireOp",EDGE,"E135"),sQuery(id+"F0.wireOp",EDGE,"E136"),sQuery(id+"F0.wireOp",EDGE,"E137"),sQuery(id+"F0.wireOp",EDGE,"E138"),sQuery(id+"F0.wireOp",EDGE,"E139"),sQuery(id+"F0.wireOp",EDGE,"E140"),sQuery(id+"F0.wireOp",EDGE,"E141"),sQuery(id+"F0.wireOp",EDGE,"E142"),sQuery(id+"F0.wireOp",EDGE,"E143"),sQuery(id+"F0.wireOp",EDGE,"E144"),sQuery(id+"F0.wireOp",EDGE,"E145"),sQuery(id+"F0.wireOp",EDGE,"E146"),sQuery(id+"F0.wireOp",EDGE,"E147"),sQuery(id+"F0.wireOp",EDGE,"E148"),sQuery(id+"F0.wireOp",EDGE,"E149"),sQuery(id+"F0.wireOp",EDGE,"E150"),sQuery(id+"F0.wireOp",EDGE,"E151"),sQuery(id+"F0.wireOp",EDGE,"E152"),sQuery(id+"F0.wireOp",EDGE,"E153"),sQuery(id+"F0.wireOp",EDGE,"E154"),sQuery(id+"F0.wireOp",EDGE,"E155"),sQuery(id+"F0.wireOp",EDGE,"E156"),sQuery(id+"F0.wireOp",EDGE,"E157"),sQuery(id+"F0.wireOp",EDGE,"E158"),sQuery(id+"F0.wireOp",EDGE,"E159"),sQuery(id+"F0.wireOp",EDGE,"E160"),sQuery(id+"F0.wireOp",EDGE,"E161"),sQuery(id+"F0.wireOp",EDGE,"E162"),sQuery(id+"F0.wireOp",EDGE,"E163"),sQuery(id+"F0.wireOp",EDGE,"E164"),sQuery(id+"F0.wireOp",EDGE,"E165"),sQuery(id+"F0.wireOp",EDGE,"E166"),sQuery(id+"F0.wireOp",EDGE,"E167"),sQuery(id+"F0.wireOp",EDGE,"E168"),sQuery(id+"F0.wireOp",EDGE,"E169"),sQuery(id+"F0.wireOp",EDGE,"E170"),sQuery(id+"F0.wireOp",EDGE,"E171"),sQuery(id+"F0.wireOp",EDGE,"E172"),sQuery(id+"F0.wireOp",EDGE,"E173"),sQuery(id+"F0.wireOp",EDGE,"E174"),sQuery(id+"F0.wireOp",EDGE,"E175"),sQuery(id+"F0.wireOp",EDGE,"E176"),sQuery(id+"F0.wireOp",EDGE,"E177"),sQuery(id+"F0.wireOp",EDGE,"E178"),sQuery(id+"F0.wireOp",EDGE,"E179"),sQuery(id+"F0.wireOp",EDGE,"E180"),sQuery(id+"F0.wireOp",EDGE,"E181"),sQuery(id+"F0.wireOp",EDGE,"E182"),sQuery(id+"F0.wireOp",EDGE,"E183"),sQuery(id+"F0.wireOp",EDGE,"E184"),sQuery(id+"F0.wireOp",EDGE,"E185"),sQuery(id+"F0.wireOp",EDGE,"E186"),sQuery(id+"F0.wireOp",EDGE,"E187"),sQuery(id+"F0.wireOp",EDGE,"E188"),sQuery(id+"F0.wireOp",EDGE,"E189"),sQuery(id+"F0.wireOp",EDGE,"E190"),sQuery(id+"F0.wireOp",EDGE,"E191"),sQuery(id+"F0.wireOp",EDGE,"E192"),sQuery(id+"F0.wireOp",EDGE,"E193"),sQuery(id+"F0.wireOp",EDGE,"E194"),sQuery(id+"F0.wireOp",EDGE,"E195"),sQuery(id+"F0.wireOp",EDGE,"E196"),sQuery(id+"F0.wireOp",EDGE,"E197"),sQuery(id+"F0.wireOp",EDGE,"E198"),sQuery(id+"F0.wireOp",EDGE,"E199"),sQuery(id+"F0.wireOp",EDGE,"E200"),sQuery(id+"F0.wireOp",EDGE,"E201"),sQuery(id+"F0.wireOp",EDGE,"E202"),sQuery(id+"F0.wireOp",EDGE,"E203"),sQuery(id+"F0.wireOp",EDGE,"E204"),sQuery(id+"F0.wireOp",EDGE,"E205"),sQuery(id+"F0.wireOp",EDGE,"E206"),sQuery(id+"F0.wireOp",EDGE,"E207"),sQuery(id+"F0.wireOp",EDGE,"E208"),sQuery(id+"F0.wireOp",EDGE,"E209"),sQuery(id+"F0.wireOp",EDGE,"E210"),sQuery(id+"F0.wireOp",EDGE,"E211"),sQuery(id+"F0.wireOp",EDGE,"E212"),sQuery(id+"F0.wireOp",EDGE,"E213"),sQuery(id+"F0.wireOp",EDGE,"E214"),sQuery(id+"F0.wireOp",EDGE,"E215"),sQuery(id+"F0.wireOp",EDGE,"E216"),sQuery(id+"F0.wireOp",EDGE,"E217"),sQuery(id+"F0.wireOp",EDGE,"E218"),sQuery(id+"F0.wireOp",EDGE,"E219"),sQuery(id+"F0.wireOp",EDGE,"E220"),sQuery(id+"F0.wireOp",EDGE,"E221"),sQuery(id+"F0.wireOp",EDGE,"E222"),sQuery(id+"F0.wireOp",EDGE,"E223"),sQuery(id+"F0.wireOp",EDGE,"E224"),sQuery(id+"F0.wireOp",EDGE,"E225"),sQuery(id+"F0.wireOp",EDGE,"E226"),sQuery(id+"F0.wireOp",EDGE,"E227"),sQuery(id+"F0.wireOp",EDGE,"E228"),sQuery(id+"F0.wireOp",EDGE,"E229"),sQuery(id+"F0.wireOp",EDGE,"E230"),sQuery(id+"F0.wireOp",EDGE,"E231"),sQuery(id+"F0.wireOp",EDGE,"E232"),sQuery(id+"F0.wireOp",EDGE,"E233"),sQuery(id+"F0.wireOp",EDGE,"E234"),sQuery(id+"F0.wireOp",EDGE,"E235"),sQuery(id+"F0.wireOp",EDGE,"E236"),sQuery(id+"F0.wireOp",EDGE,"E237"),sQuery(id+"F0.wireOp",EDGE,"E238"),sQuery(id+"F0.wireOp",EDGE,"E239"),sQuery(id+"F0.wireOp",EDGE,"E240"),sQuery(id+"F0.wireOp",EDGE,"E241"),sQuery(id+"F0.wireOp",EDGE,"E242"),sQuery(id+"F0.wireOp",EDGE,"E243"),sQuery(id+"F0.wireOp",EDGE,"E244"),sQuery(id+"F0.wireOp",EDGE,"E245"),sQuery(id+"F0.wireOp",EDGE,"E246"),sQuery(id+"F0.wireOp",EDGE,"E247"),sQuery(id+"F0.wireOp",EDGE,"E248"),sQuery(id+"F0.wireOp",EDGE,"E249"),sQuery(id+"F0.wireOp",EDGE,"E250"),sQuery(id+"F0.wireOp",EDGE,"E251"),sQuery(id+"F0.wireOp",EDGE,"E252"),sQuery(id+"F0.wireOp",EDGE,"E253"),sQuery(id+"F0.wireOp",EDGE,"E254"),sQuery(id+"F0.wireOp",EDGE,"E255"),sQuery(id+"F0.wireOp",EDGE,"E256"),sQuery(id+"F0.wireOp",EDGE,"E257"),sQuery(id+"F0.wireOp",EDGE,"E258"),sQuery(id+"F0.wireOp",EDGE,"E259"),sQuery(id+"F0.wireOp",EDGE,"E260"),sQuery(id+"F0.wireOp",EDGE,"E261"),sQuery(id+"F0.wireOp",EDGE,"E262"),sQuery(id+"F0.wireOp",EDGE,"E263"),sQuery(id+"F0.wireOp",EDGE,"E264"),sQuery(id+"F0.wireOp",EDGE,"E265"),sQuery(id+"F0.wireOp",EDGE,"E266"),sQuery(id+"F0.wireOp",EDGE,"E267"),sQuery(id+"F0.wireOp",EDGE,"E268"),sQuery(id+"F0.wireOp",EDGE,"E269"),sQuery(id+"F0.wireOp",EDGE,"E270"),sQuery(id+"F0.wireOp",EDGE,"E271"),sQuery(id+"F0.wireOp",EDGE,"E272"),sQuery(id+"F0.wireOp",EDGE,"E273"),sQuery(id+"F0.wireOp",EDGE,"E274"),sQuery(id+"F0.wireOp",EDGE,"E275"),sQuery(id+"F0.wireOp",EDGE,"E276"),sQuery(id+"F0.wireOp",EDGE,"E277"),sQuery(id+"F0.wireOp",EDGE,"E280"),sQuery(id+"F0.wireOp",EDGE,"E281"),sQuery(id+"F0.wireOp",EDGE,"E282"),sQuery(id+"F0.wireOp",EDGE,"E283"),sQuery(id+"F0.wireOp",EDGE,"E284"),sQuery(id+"F0.wireOp",EDGE,"E285"),sQuery(id+"F0.wireOp",EDGE,"E286"),sQuery(id+"F0.wireOp",EDGE,"E287"),sQuery(id+"F0.wireOp",EDGE,"E288"),sQuery(id+"F0.wireOp",EDGE,"E289"),sQuery(id+"F0.wireOp",EDGE,"E290"),sQuery(id+"F0.wireOp",EDGE,"E291"),sQuery(id+"F0.wireOp",EDGE,"E292"),sQuery(id+"F0.wireOp",EDGE,"E293"),sQuery(id+"F0.wireOp",EDGE,"E294"),sQuery(id+"F0.wireOp",EDGE,"E295"),sQuery(id+"F0.wireOp",EDGE,"E296"),sQuery(id+"F0.wireOp",EDGE,"E297"),sQuery(id+"F0.wireOp",EDGE,"E298"),sQuery(id+"F0.wireOp",EDGE,"E299"),sQuery(id+"F0.wireOp",EDGE,"E300"),sQuery(id+"F0.wireOp",EDGE,"E301"),sQuery(id+"F0.wireOp",EDGE,"E302"),sQuery(id+"F0.wireOp",EDGE,"E303"),sQuery(id+"F0.wireOp",EDGE,"E304"),sQuery(id+"F0.wireOp",EDGE,"E305"),sQuery(id+"F0.wireOp",EDGE,"E306"),sQuery(id+"F0.wireOp",EDGE,"E307"),sQuery(id+"F0.wireOp",EDGE,"E308"),sQuery(id+"F0.wireOp",EDGE,"E309"),sQuery(id+"F0.wireOp",EDGE,"E310"),sQuery(id+"F0.wireOp",EDGE,"E311"),sQuery(id+"F0.wireOp",EDGE,"E316"),sQuery(id+"F0.wireOp",EDGE,"E317"),sQuery(id+"F0.wireOp",EDGE,"E318"),sQuery(id+"F0.wireOp",EDGE,"E319"),sQuery(id+"F0.wireOp",EDGE,"E320"),sQuery(id+"F0.wireOp",EDGE,"E321"),sQuery(id+"F0.wireOp",EDGE,"E322"),sQuery(id+"F0.wireOp",EDGE,"E323"),sQuery(id+"F0.wireOp",EDGE,"E324"),sQuery(id+"F0.wireOp",EDGE,"E325"),sQuery(id+"F0.wireOp",EDGE,"E326"),sQuery(id+"F0.wireOp",EDGE,"E327"),sQuery(id+"F0.wireOp",EDGE,"E328"),sQuery(id+"F0.wireOp",EDGE,"E329"),sQuery(id+"F0.wireOp",EDGE,"E330"),sQuery(id+"F0.wireOp",EDGE,"E331"),sQuery(id+"F0.wireOp",EDGE,"E332"),sQuery(id+"F0.wireOp",EDGE,"E333"),sQuery(id+"F0.wireOp",EDGE,"E334"),sQuery(id+"F0.wireOp",EDGE,"E335"),sQuery(id+"F0.wireOp",EDGE,"E336"),sQuery(id+"F0.wireOp",EDGE,"E337"),sQuery(id+"F0.wireOp",EDGE,"E338"),sQuery(id+"F0.wireOp",EDGE,"E339"),sQuery(id+"F0.wireOp",EDGE,"E340"),sQuery(id+"F0.wireOp",EDGE,"E341"),sQuery(id+"F0.wireOp",EDGE,"E342"),sQuery(id+"F0.wireOp",EDGE,"E343"),sQuery(id+"F0.wireOp",EDGE,"E344"),sQuery(id+"F0.wireOp",EDGE,"E345"),sQuery(id+"F0.wireOp",EDGE,"E346"),sQuery(id+"F0.wireOp",EDGE,"E347"),sQuery(id+"F0.wireOp",EDGE,"E348"),sQuery(id+"F0.wireOp",EDGE,"E349"),sQuery(id+"F0.wireOp",EDGE,"E350"),sQuery(id+"F0.wireOp",EDGE,"E351"),sQuery(id+"F0.wireOp",EDGE,"E352"),sQuery(id+"F0.wireOp",EDGE,"E353"),sQuery(id+"F0.wireOp",EDGE,"E354"),sQuery(id+"F0.wireOp",EDGE,"E355"),sQuery(id+"F0.wireOp",EDGE,"E356"),sQuery(id+"F0.wireOp",EDGE,"E357"),sQuery(id+"F0.wireOp",EDGE,"E358"),sQuery(id+"F0.wireOp",EDGE,"E359"),sQuery(id+"F0.wireOp",EDGE,"E360"),sQuery(id+"F0.wireOp",EDGE,"E361"),sQuery(id+"F0.wireOp",EDGE,"E362"),sQuery(id+"F0.wireOp",EDGE,"E363"),sQuery(id+"F0.wireOp",EDGE,"E364"),sQuery(id+"F0.wireOp",EDGE,"E365"),sQuery(id+"F0.wireOp",EDGE,"E366"),sQuery(id+"F0.wireOp",EDGE,"E367"),sQuery(id+"F0.wireOp",EDGE,"E368"),sQuery(id+"F0.wireOp",EDGE,"E369"),sQuery(id+"F0.wireOp",EDGE,"E370"),sQuery(id+"F0.wireOp",EDGE,"E371"),sQuery(id+"F0.wireOp",EDGE,"E372"),sQuery(id+"F0.wireOp",EDGE,"E373"),sQuery(id+"F0.wireOp",EDGE,"E374"),sQuery(id+"F0.wireOp",EDGE,"E375"),sQuery(id+"F0.wireOp",EDGE,"E376"),sQuery(id+"F0.wireOp",EDGE,"E377"),sQuery(id+"F0.wireOp",EDGE,"E378"),sQuery(id+"F0.wireOp",EDGE,"E379"),sQuery(id+"F0.wireOp",EDGE,"E380"),sQuery(id+"F0.wireOp",EDGE,"E381"),sQuery(id+"F0.wireOp",EDGE,"E382"),sQuery(id+"F0.wireOp",EDGE,"E383"),sQuery(id+"F0.wireOp",EDGE,"E384"),sQuery(id+"F0.wireOp",EDGE,"E385"),sQuery(id+"F0.wireOp",EDGE,"E386"),sQuery(id+"F0.wireOp",EDGE,"E387"),sQuery(id+"F0.wireOp",EDGE,"E388"),sQuery(id+"F0.wireOp",EDGE,"E389"),sQuery(id+"F0.wireOp",EDGE,"E390"),sQuery(id+"F0.wireOp",EDGE,"E391"),sQuery(id+"F0.wireOp",EDGE,"E392"),sQuery(id+"F0.wireOp",EDGE,"E393"),sQuery(id+"F0.wireOp",EDGE,"E394"),sQuery(id+"F0.wireOp",EDGE,"E395"),sQuery(id+"F0.wireOp",EDGE,"E396"),sQuery(id+"F0.wireOp",EDGE,"E397"),sQuery(id+"F0.wireOp",EDGE,"E398"),sQuery(id+"F0.wireOp",EDGE,"E399"),sQuery(id+"F0.wireOp",EDGE,"E400"),sQuery(id+"F0.wireOp",EDGE,"E401"),sQuery(id+"F0.wireOp",EDGE,"E402"),sQuery(id+"F0.wireOp",EDGE,"E403"),sQuery(id+"F0.wireOp",EDGE,"E404"),sQuery(id+"F0.wireOp",EDGE,"E405"),sQuery(id+"F0.wireOp",EDGE,"E406"),sQuery(id+"F0.wireOp",EDGE,"E407"),sQuery(id+"F0.wireOp",EDGE,"E408"),sQuery(id+"F0.wireOp",EDGE,"E409"),sQuery(id+"F0.wireOp",EDGE,"E410"),sQuery(id+"F0.wireOp",EDGE,"E411"),sQuery(id+"F0.wireOp",EDGE,"E412"),sQuery(id+"F0.wireOp",EDGE,"E413"),sQuery(id+"F0.wireOp",EDGE,"E414"),sQuery(id+"F0.wireOp",EDGE,"E415"),sQuery(id+"F0.wireOp",EDGE,"E416"),sQuery(id+"F0.wireOp",EDGE,"E417"),sQuery(id+"F0.wireOp",EDGE,"E418"),sQuery(id+"F0.wireOp",EDGE,"E419"),sQuery(id+"F0.wireOp",EDGE,"E420"),sQuery(id+"F0.wireOp",EDGE,"E421"),sQuery(id+"F0.wireOp",EDGE,"E422"),sQuery(id+"F0.wireOp",EDGE,"E423"),sQuery(id+"F0.wireOp",EDGE,"E424"),sQuery(id+"F0.wireOp",EDGE,"E425"),sQuery(id+"F0.wireOp",EDGE,"E426"),sQuery(id+"F0.wireOp",EDGE,"E427"),sQuery(id+"F0.wireOp",EDGE,"E428"),sQuery(id+"F0.wireOp",EDGE,"E429"),sQuery(id+"F0.wireOp",EDGE,"E430"),sQuery(id+"F0.wireOp",EDGE,"E431"),sQuery(id+"F0.wireOp",EDGE,"E432"),sQuery(id+"F0.wireOp",EDGE,"E433"),sQuery(id+"F0.wireOp",EDGE,"E434"),sQuery(id+"F0.wireOp",EDGE,"E435"),sQuery(id+"F0.wireOp",EDGE,"E436"),sQuery(id+"F0.wireOp",EDGE,"E437"),sQuery(id+"F0.wireOp",EDGE,"E438"),sQuery(id+"F0.wireOp",EDGE,"E439"),sQuery(id+"F0.wireOp",EDGE,"E440"),sQuery(id+"F0.wireOp",EDGE,"E441"),sQuery(id+"F0.wireOp",EDGE,"E442"),sQuery(id+"F0.wireOp",EDGE,"E443"),sQuery(id+"F0.wireOp",EDGE,"E444"),sQuery(id+"F0.wireOp",EDGE,"E445"),sQuery(id+"F0.wireOp",EDGE,"E446"),sQuery(id+"F0.wireOp",EDGE,"E447"),sQuery(id+"F0.wireOp",EDGE,"E448"),sQuery(id+"F0.wireOp",EDGE,"E449"),sQuery(id+"F0.wireOp",EDGE,"E450"),sQuery(id+"F0.wireOp",EDGE,"E451"),sQuery(id+"F0.wireOp",EDGE,"E452"),sQuery(id+"F0.wireOp",EDGE,"E453"),sQuery(id+"F0.wireOp",EDGE,"E454"),sQuery(id+"F0.wireOp",EDGE,"E455"),sQuery(id+"F0.wireOp",EDGE,"E456"),sQuery(id+"F0.wireOp",EDGE,"E457"),sQuery(id+"F0.wireOp",EDGE,"E458"),sQuery(id+"F0.wireOp",EDGE,"E459"),sQuery(id+"F0.wireOp",EDGE,"E460"),sQuery(id+"F0.wireOp",EDGE,"E461"),sQuery(id+"F0.wireOp",EDGE,"E462"),sQuery(id+"F0.wireOp",EDGE,"E463"),sQuery(id+"F0.wireOp",EDGE,"E464"),sQuery(id+"F0.wireOp",EDGE,"E465"),sQuery(id+"F0.wireOp",EDGE,"E466"),sQuery(id+"F0.wireOp",EDGE,"E467"),sQuery(id+"F0.wireOp",EDGE,"E468"),sQuery(id+"F0.wireOp",EDGE,"E469"),sQuery(id+"F0.wireOp",EDGE,"E470"),sQuery(id+"F0.wireOp",EDGE,"E471"),sQuery(id+"F0.wireOp",EDGE,"E472"),sQuery(id+"F0.wireOp",EDGE,"E473"),sQuery(id+"F0.wireOp",EDGE,"E474"),sQuery(id+"F0.wireOp",EDGE,"E475"),sQuery(id+"F0.wireOp",EDGE,"E476"),sQuery(id+"F0.wireOp",EDGE,"E477"),sQuery(id+"F0.wireOp",EDGE,"E478"),sQuery(id+"F0.wireOp",EDGE,"E479"),sQuery(id+"F0.wireOp",EDGE,"E480"),sQuery(id+"F0.wireOp",EDGE,"E481"),sQuery(id+"F0.wireOp",EDGE,"E482"),sQuery(id+"F0.wireOp",EDGE,"E483"),sQuery(id+"F0.wireOp",EDGE,"E484"),sQuery(id+"F0.wireOp",EDGE,"E485"),sQuery(id+"F0.wireOp",EDGE,"E486"),sQuery(id+"F0.wireOp",EDGE,"E487"),sQuery(id+"F0.wireOp",EDGE,"E488"),sQuery(id+"F0.wireOp",EDGE,"E489"),sQuery(id+"F0.wireOp",EDGE,"E490"),sQuery(id+"F0.wireOp",EDGE,"E491"),sQuery(id+"F0.wireOp",EDGE,"E492"),sQuery(id+"F0.wireOp",EDGE,"E493"),sQuery(id+"F0.wireOp",EDGE,"E494"),sQuery(id+"F0.wireOp",EDGE,"E495"),sQuery(id+"F0.wireOp",EDGE,"E496"),sQuery(id+"F0.wireOp",EDGE,"E497"),sQuery(id+"F0.wireOp",EDGE,"E498"),sQuery(id+"F0.wireOp",EDGE,"E499"),sQuery(id+"F0.wireOp",EDGE,"E500"),sQuery(id+"F0.wireOp",EDGE,"E501"),sQuery(id+"F0.wireOp",EDGE,"E502"),sQuery(id+"F0.wireOp",EDGE,"E503"),sQuery(id+"F0.wireOp",EDGE,"E504"),sQuery(id+"F0.wireOp",EDGE,"E505"),sQuery(id+"F0.wireOp",EDGE,"E506"),sQuery(id+"F0.wireOp",EDGE,"E507"),sQuery(id+"F0.wireOp",EDGE,"E508"),sQuery(id+"F0.wireOp",EDGE,"E509"),sQuery(id+"F0.wireOp",EDGE,"E510"),sQuery(id+"F0.wireOp",EDGE,"E511"),sQuery(id+"F0.wireOp",EDGE,"E512"),sQuery(id+"F0.wireOp",EDGE,"E513"),sQuery(id+"F0.wireOp",EDGE,"E514"),sQuery(id+"F0.wireOp",EDGE,"E515"),sQuery(id+"F0.wireOp",EDGE,"E516"),sQuery(id+"F0.wireOp",EDGE,"E517"),sQuery(id+"F0.wireOp",EDGE,"E518"),sQuery(id+"F0.wireOp",EDGE,"E519"),sQuery(id+"F0.wireOp",EDGE,"E520"),sQuery(id+"F0.wireOp",EDGE,"E521"),sQuery(id+"F0.wireOp",EDGE,"E522"),sQuery(id+"F0.wireOp",EDGE,"E523"),sQuery(id+"F0.wireOp",EDGE,"E524"),sQuery(id+"F0.wireOp",EDGE,"E525"),sQuery(id+"F0.wireOp",EDGE,"E526"),sQuery(id+"F0.wireOp",EDGE,"E527"),sQuery(id+"F0.wireOp",EDGE,"E528"),sQuery(id+"F0.wireOp",EDGE,"E529"),sQuery(id+"F0.wireOp",EDGE,"E530"),sQuery(id+"F0.wireOp",EDGE,"E531"),sQuery(id+"F0.wireOp",EDGE,"E532"),sQuery(id+"F0.wireOp",EDGE,"E533"),sQuery(id+"F0.wireOp",EDGE,"E534"),sQuery(id+"F0.wireOp",EDGE,"E535"),sQuery(id+"F0.wireOp",EDGE,"E536"),sQuery(id+"F0.wireOp",EDGE,"E537"),sQuery(id+"F0.wireOp",EDGE,"E538"),sQuery(id+"F0.wireOp",EDGE,"E539"),sQuery(id+"F0.wireOp",EDGE,"E540"),sQuery(id+"F0.wireOp",EDGE,"E541"),sQuery(id+"F0.wireOp",EDGE,"E542"),sQuery(id+"F0.wireOp",EDGE,"E543"),sQuery(id+"F0.wireOp",EDGE,"E544"),sQuery(id+"F0.wireOp",EDGE,"E545"),sQuery(id+"F0.wireOp",EDGE,"E546"),sQuery(id+"F0.wireOp",EDGE,"E547"),sQuery(id+"F0.wireOp",EDGE,"E548"),sQuery(id+"F0.wireOp",EDGE,"E549"),sQuery(id+"F0.wireOp",EDGE,"E550"),sQuery(id+"F0.wireOp",EDGE,"E551"),sQuery(id+"F0.wireOp",EDGE,"E552"),sQuery(id+"F0.wireOp",EDGE,"E553"),sQuery(id+"F0.wireOp",EDGE,"E554"),sQuery(id+"F0.wireOp",EDGE,"E555"),sQuery(id+"F0.wireOp",EDGE,"E556"),sQuery(id+"F0.wireOp",EDGE,"E557"),sQuery(id+"F0.wireOp",EDGE,"E558"),sQuery(id+"F0.wireOp",EDGE,"E559"),sQuery(id+"F0.wireOp",EDGE,"E560"),sQuery(id+"F0.wireOp",EDGE,"E561"),sQuery(id+"F0.wireOp",EDGE,"E562"),sQuery(id+"F0.wireOp",EDGE,"E563"),sQuery(id+"F0.wireOp",EDGE,"E564"),sQuery(id+"F0.wireOp",EDGE,"E565"),sQuery(id+"F0.wireOp",EDGE,"E566"),sQuery(id+"F0.wireOp",EDGE,"E567"),sQuery(id+"F0.wireOp",EDGE,"E568"),sQuery(id+"F0.wireOp",EDGE,"E569"),sQuery(id+"F0.wireOp",EDGE,"E570"),sQuery(id+"F0.wireOp",EDGE,"E571"),sQuery(id+"F0.wireOp",EDGE,"E572"),sQuery(id+"F0.wireOp",EDGE,"E573"),sQuery(id+"F0.wireOp",EDGE,"E574"),sQuery(id+"F0.wireOp",EDGE,"E575"),sQuery(id+"F0.wireOp",EDGE,"E576"),sQuery(id+"F0.wireOp",EDGE,"E577"),sQuery(id+"F0.wireOp",EDGE,"E578"),sQuery(id+"F0.wireOp",EDGE,"E579"),sQuery(id+"F0.wireOp",EDGE,"E580"),sQuery(id+"F0.wireOp",EDGE,"E581"),sQuery(id+"F0.wireOp",EDGE,"E582"),sQuery(id+"F0.wireOp",EDGE,"E583"),sQuery(id+"F0.wireOp",EDGE,"E584"),sQuery(id+"F0.wireOp",EDGE,"E585"),sQuery(id+"F0.wireOp",EDGE,"E586"),sQuery(id+"F0.wireOp",EDGE,"E587"),sQuery(id+"F0.wireOp",EDGE,"E588"),sQuery(id+"F0.wireOp",EDGE,"E589"),sQuery(id+"F0.wireOp",EDGE,"E590"),sQuery(id+"F0.wireOp",EDGE,"E591"),sQuery(id+"F0.wireOp",EDGE,"E592"),sQuery(id+"F0.wireOp",EDGE,"E593"),sQuery(id+"F0.wireOp",EDGE,"E594"),sQuery(id+"F0.wireOp",EDGE,"E595"),sQuery(id+"F0.wireOp",EDGE,"E596"),sQuery(id+"F0.wireOp",EDGE,"E597"),sQuery(id+"F0.wireOp",EDGE,"E598"),sQuery(id+"F0.wireOp",EDGE,"E599"),sQuery(id+"F0.wireOp",EDGE,"E600"),sQuery(id+"F0.wireOp",EDGE,"E601"),sQuery(id+"F0.wireOp",EDGE,"E602"),sQuery(id+"F0.wireOp",EDGE,"E603"),sQuery(id+"F0.wireOp",EDGE,"E604"),sQuery(id+"F0.wireOp",EDGE,"E605"),sQuery(id+"F0.wireOp",EDGE,"E606"),sQuery(id+"F0.wireOp",EDGE,"E607"),sQuery(id+"F0.wireOp",EDGE,"E608"),sQuery(id+"F0.wireOp",EDGE,"E609"),sQuery(id+"F0.wireOp",EDGE,"E610"),sQuery(id+"F0.wireOp",EDGE,"E611"),sQuery(id+"F0.wireOp",EDGE,"E612"),sQuery(id+"F0.wireOp",EDGE,"E613"),sQuery(id+"F0.wireOp",EDGE,"E614"),sQuery(id+"F0.wireOp",EDGE,"E615"),sQuery(id+"F0.wireOp",EDGE,"E616"),sQuery(id+"F0.wireOp",EDGE,"E617"),sQuery(id+"F0.wireOp",EDGE,"E618"),sQuery(id+"F0.wireOp",EDGE,"E619"),sQuery(id+"F0.wireOp",EDGE,"E620"),sQuery(id+"F0.wireOp",EDGE,"E621"),sQuery(id+"F0.wireOp",EDGE,"E622"),sQuery(id+"F0.wireOp",EDGE,"E623"),sQuery(id+"F0.wireOp",EDGE,"E624"),sQuery(id+"F0.wireOp",EDGE,"E625"),sQuery(id+"F0.wireOp",EDGE,"E626"),sQuery(id+"F0.wireOp",EDGE,"E627"),sQuery(id+"F0.wireOp",EDGE,"E628"),sQuery(id+"F0.wireOp",EDGE,"E629"),sQuery(id+"F0.wireOp",EDGE,"E630"),sQuery(id+"F0.wireOp",EDGE,"E631"),sQuery(id+"F0.wireOp",EDGE,"E632"),sQuery(id+"F0.wireOp",EDGE,"E633"),sQuery(id+"F0.wireOp",EDGE,"E634"),sQuery(id+"F0.wireOp",EDGE,"E635"),sQuery(id+"F0.wireOp",EDGE,"E636"),sQuery(id+"F0.wireOp",EDGE,"E637"),sQuery(id+"F0.wireOp",EDGE,"E638"),sQuery(id+"F0.wireOp",EDGE,"E639"),sQuery(id+"F0.wireOp",EDGE,"E640"),sQuery(id+"F0.wireOp",EDGE,"E641"),sQuery(id+"F0.wireOp",EDGE,"E642"),sQuery(id+"F0.wireOp",EDGE,"E643"),sQuery(id+"F0.wireOp",EDGE,"E644"),sQuery(id+"F0.wireOp",EDGE,"E645"),sQuery(id+"F0.wireOp",EDGE,"E646"),sQuery(id+"F0.wireOp",EDGE,"E647"),sQuery(id+"F0.wireOp",EDGE,"E648"),sQuery(id+"F0.wireOp",EDGE,"E649"),sQuery(id+"F0.wireOp",EDGE,"E650"),sQuery(id+"F0.wireOp",EDGE,"E651"),sQuery(id+"F0.wireOp",EDGE,"E652"),sQuery(id+"F0.wireOp",EDGE,"E653"),sQuery(id+"F0.wireOp",EDGE,"E654"),sQuery(id+"F0.wireOp",EDGE,"E655"),sQuery(id+"F0.wireOp",EDGE,"E656"),sQuery(id+"F0.wireOp",EDGE,"E657"),sQuery(id+"F0.wireOp",EDGE,"E658"),sQuery(id+"F0.wireOp",EDGE,"E659"),sQuery(id+"F0.wireOp",EDGE,"E660"),sQuery(id+"F0.wireOp",EDGE,"E661"),sQuery(id+"F0.wireOp",EDGE,"E662"),sQuery(id+"F0.wireOp",EDGE,"E663"),sQuery(id+"F0.wireOp",EDGE,"E664"),sQuery(id+"F0.wireOp",EDGE,"E665"),sQuery(id+"F0.wireOp",EDGE,"E666"),sQuery(id+"F0.wireOp",EDGE,"E667"),sQuery(id+"F0.wireOp",EDGE,"E668"),sQuery(id+"F0.wireOp",EDGE,"E669"),sQuery(id+"F0.wireOp",EDGE,"E670"),sQuery(id+"F0.wireOp",EDGE,"E671"),sQuery(id+"F0.wireOp",EDGE,"E672"),sQuery(id+"F0.wireOp",EDGE,"E673"),sQuery(id+"F0.wireOp",EDGE,"E674"),sQuery(id+"F0.wireOp",EDGE,"E675"),sQuery(id+"F0.wireOp",EDGE,"E676"),sQuery(id+"F0.wireOp",EDGE,"E677"),sQuery(id+"F0.wireOp",EDGE,"E678"),sQuery(id+"F0.wireOp",EDGE,"E679"),sQuery(id+"F0.wireOp",EDGE,"E680"),sQuery(id+"F0.wireOp",EDGE,"E681"),sQuery(id+"F0.wireOp",EDGE,"E682"),sQuery(id+"F0.wireOp",EDGE,"E683"),sQuery(id+"F0.wireOp",EDGE,"E684"),sQuery(id+"F0.wireOp",EDGE,"E685"),sQuery(id+"F0.wireOp",EDGE,"E686"),sQuery(id+"F0.wireOp",EDGE,"E687"),sQuery(id+"F0.wireOp",EDGE,"E688"),sQuery(id+"F0.wireOp",EDGE,"E689"),sQuery(id+"F0.wireOp",EDGE,"E690"),sQuery(id+"F0.wireOp",EDGE,"E691"),sQuery(id+"F0.wireOp",EDGE,"E692"),sQuery(id+"F0.wireOp",EDGE,"E693"),sQuery(id+"F0.wireOp",EDGE,"E694"),sQuery(id+"F0.wireOp",EDGE,"E695"),sQuery(id+"F0.wireOp",EDGE,"E696"),sQuery(id+"F0.wireOp",EDGE,"E697"),sQuery(id+"F0.wireOp",EDGE,"E698"),sQuery(id+"F0.wireOp",EDGE,"E699"),sQuery(id+"F0.wireOp",EDGE,"E700"),sQuery(id+"F0.wireOp",EDGE,"E701"),sQuery(id+"F0.wireOp",EDGE,"E702"),sQuery(id+"F0.wireOp",EDGE,"E703"),sQuery(id+"F0.wireOp",EDGE,"E704"),sQuery(id+"F0.wireOp",EDGE,"E705"),sQuery(id+"F0.wireOp",EDGE,"E706"),sQuery(id+"F0.wireOp",EDGE,"E707"),sQuery(id+"F0.wireOp",EDGE,"E708"),sQuery(id+"F0.wireOp",EDGE,"E709"),sQuery(id+"F0.wireOp",EDGE,"E710"),sQuery(id+"F0.wireOp",EDGE,"E711"),sQuery(id+"F0.wireOp",EDGE,"E712"),sQuery(id+"F0.wireOp",EDGE,"E713"),sQuery(id+"F0.wireOp",EDGE,"E714"),sQuery(id+"F0.wireOp",EDGE,"E715"),sQuery(id+"F0.wireOp",EDGE,"E716"),sQuery(id+"F0.wireOp",EDGE,"E717"),sQuery(id+"F0.wireOp",EDGE,"E718"),sQuery(id+"F0.wireOp",EDGE,"E719"),sQuery(id+"F0.wireOp",EDGE,"E720"),sQuery(id+"F0.wireOp",EDGE,"E721"),sQuery(id+"F0.wireOp",EDGE,"E722"),sQuery(id+"F0.wireOp",EDGE,"E723"),sQuery(id+"F0.wireOp",EDGE,"E724"),sQuery(id+"F0.wireOp",EDGE,"E725"),sQuery(id+"F0.wireOp",EDGE,"E726"),sQuery(id+"F0.wireOp",EDGE,"E727"),sQuery(id+"F0.wireOp",EDGE,"E728"),sQuery(id+"F0.wireOp",EDGE,"E729"),sQuery(id+"F0.wireOp",EDGE,"E730"),sQuery(id+"F0.wireOp",EDGE,"E731"),sQuery(id+"F0.wireOp",EDGE,"E732"),sQuery(id+"F0.wireOp",EDGE,"E733"),sQuery(id+"F0.wireOp",EDGE,"E734"),sQuery(id+"F0.wireOp",EDGE,"E735"),sQuery(id+"F0.wireOp",EDGE,"E736"),sQuery(id+"F0.wireOp",EDGE,"E737"),sQuery(id+"F0.wireOp",EDGE,"E738"),sQuery(id+"F0.wireOp",EDGE,"E739"),sQuery(id+"F0.wireOp",EDGE,"E740"),sQuery(id+"F0.wireOp",EDGE,"E783"),sQuery(id+"F0.wireOp",EDGE,"E789")])],"isStart":false});
            var sketch = newSketch(context, id + "F2", { "sketchPlane" : qUnion([Q0])});
            skCircle(sketch, "E1282.0", {"center": v(-20.14, 2.96) * mm, "radius": 6.35 * mm});
            skLineSegment(sketch, "E1283", {"start": v(-20.14, 2.96) * mm, "end": v(-20.14, 47.41) * mm, "construction": true});
            skCircle(sketch, "E1284", {"center": v(-20.14, 2.96) * mm, "radius": 44.45 * mm});
            skCircle(sketch, "E1285", {"center": v(-20.14, 2.96) * mm, "radius": 19.05 * mm});
            skLineSegment(sketch, "E1286", {"start": v(-23.03, 47.32) * mm, "end": v(-23.03, 21.8) * mm});
            skLineSegment(sketch, "E1287.MirrorCS", {"start": v(-17.24, 47.32) * mm, "end": v(-17.24, 21.8) * mm});
            skLineSegment(sketch, "E1288.1.0", {"start": v(-64.5, 0.07) * mm, "end": v(-38.96, 0.07) * mm});
            skLineSegment(sketch, "E1288.1.1", {"start": v(-64.5, 5.86) * mm, "end": v(-38.96, 5.86) * mm});
            skLineSegment(sketch, "E1288.2.0", {"start": v(-17.24, -41.4) * mm, "end": v(-17.24, -15.87) * mm});
            skLineSegment(sketch, "E1288.2.1", {"start": v(-23.03, -41.4) * mm, "end": v(-23.03, -15.87) * mm});
            skLineSegment(sketch, "E1288.3.0", {"start": v(24.22, 5.86) * mm, "end": v(-1.3, 5.86) * mm});
            skLineSegment(sketch, "E1288.3.1", {"start": v(24.22, 0.07) * mm, "end": v(-1.3, 0.07) * mm});
            skSolve(sketch);
        }
        {
            var Q0;
            {var subQ0=sQuery(id+"F2.wireOp",EDGE,"E1286");Q0=makeQuery(id+"F2.imprint","IMPRINT",FACE,{"disambiguationData":[TD([[makeQuery(id+"F2.imprint","IMPRINT",EDGE,{"derivedFrom":subQ0}),-1.0]])]});}
            var Q1;
            {var subQ0=sQuery(id+"F2.wireOp",EDGE,"E1287.MirrorCS");Q1=makeQuery(id+"F2.imprint","IMPRINT",FACE,{"disambiguationData":[TD([[makeQuery(id+"F2.imprint","IMPRINT",EDGE,{"derivedFrom":subQ0}),1.0]])]});}
            var Q2;
            {var subQ0=sQuery(id+"F2.wireOp",EDGE,"E1288.2.0");Q2=makeQuery(id+"F2.imprint","IMPRINT",FACE,{"disambiguationData":[TD([[makeQuery(id+"F2.imprint","IMPRINT",EDGE,{"derivedFrom":subQ0}),-1.0]])]});}
            var Q3;
            {var subQ0=sQuery(id+"F2.wireOp",EDGE,"E1288.1.0");Q3=makeQuery(id+"F2.imprint","IMPRINT",FACE,{"disambiguationData":[TD([[makeQuery(id+"F2.imprint","IMPRINT",EDGE,{"derivedFrom":subQ0}),-1.0]])]});}
            extrude(context, id + "F3", {"entities" : qUnion([Q0, Q1, Q2, Q3]), "operationType" : NewBodyOperationType.REMOVE, "oppositeDirection" : true, "depth" : 25.4 * mm, "offsetDistance" : 25.4 * mm});
        }
    });
